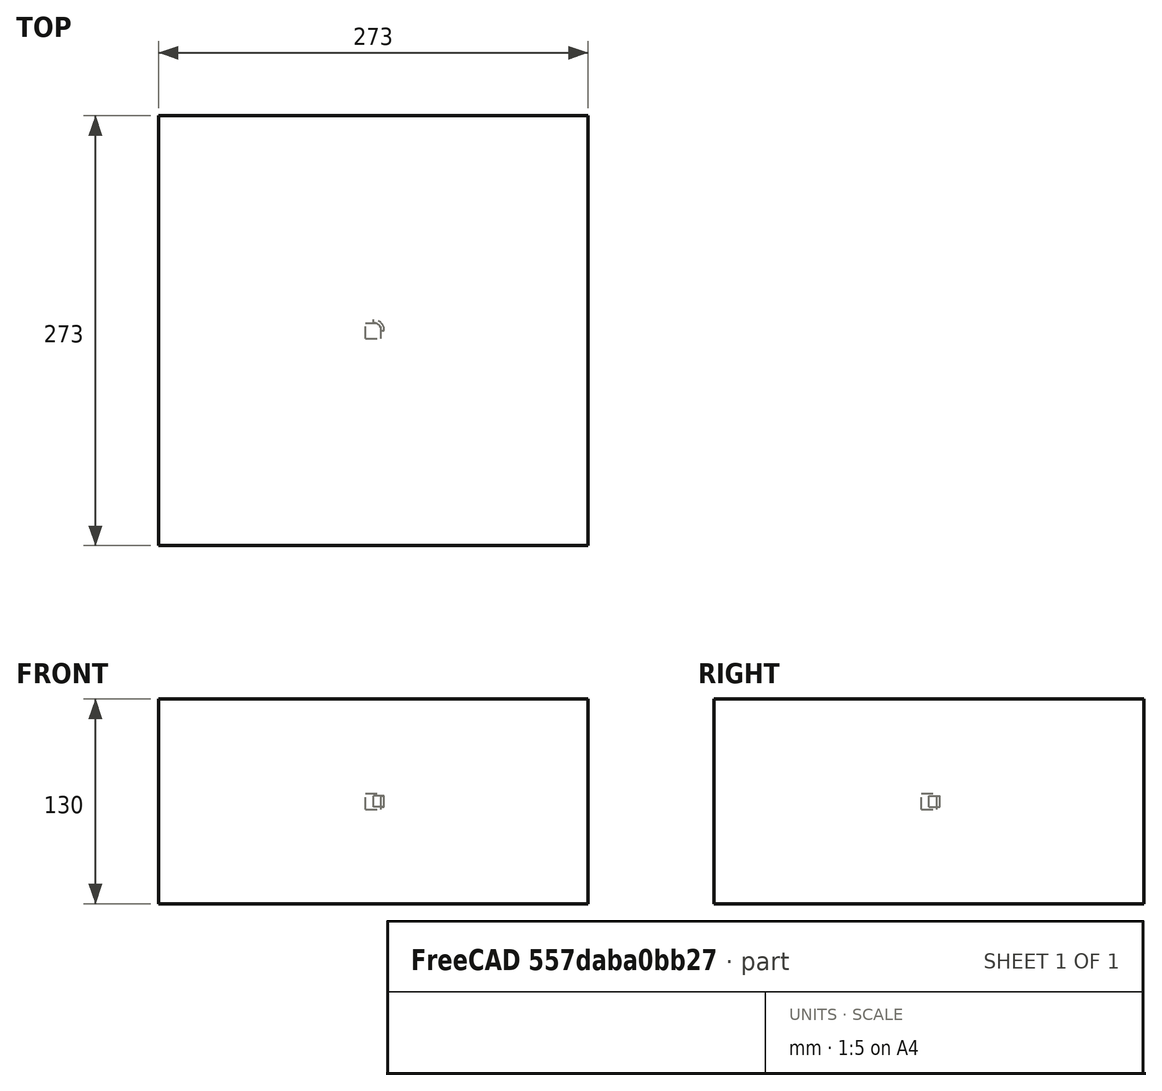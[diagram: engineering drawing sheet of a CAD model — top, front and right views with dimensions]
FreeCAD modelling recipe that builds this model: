
FCSTD DOCUMENT  (FreeCAD 0.20RUnknown)
Label: polarArray-container-b
License: All rights reserved
LicenseURL: http://en.wikipedia.org/wiki/All_rights_reserved
objects: App::DocumentObjectGroupPython×1251, Part::FeaturePython×4, App::Part×4
note: 3 computed .brp shape members not serialized (recipe doc carries the construction recipe); baked Part::Feature solids carry a one-line shape summary decoded from their .brp

FEATURE [App::DocumentObjectGroupPython] HALFPI  # scripted group (container) (typed FeaturePython)
  name = HALFPI
  value = pi/2.
FEATURE [App::DocumentObjectGroupPython] PI  # scripted group (container) (typed FeaturePython)
  name = PI
  value = 1.*pi
FEATURE [App::DocumentObjectGroupPython] TWOPI  # scripted group (container) (typed FeaturePython)
  name = TWOPI
  value = 2.*pi
FEATURE [App::DocumentObjectGroupPython] Constants  # scripted group (container) (typed FeaturePython)
  Group = -> [HALFPI,PI,TWOPI]
FEATURE [App::DocumentObjectGroupPython] Variables  # scripted group (container) (typed FeaturePython)
FEATURE [App::DocumentObjectGroupPython] Quantities  # scripted group (container) (typed FeaturePython)
FEATURE [App::DocumentObjectGroupPython] Isotopes  # scripted group (container) (typed FeaturePython)
FEATURE [App::DocumentObjectGroupPython] Elements  # scripted group (container) (typed FeaturePython)
FEATURE [App::DocumentObjectGroupPython] Matrix  # scripted group (container) (typed FeaturePython)
FEATURE [App::DocumentObjectGroupPython] Surfaces  # scripted group (container) (typed FeaturePython)
FEATURE [App::DocumentObjectGroupPython] Opticals  # scripted group (container) (typed FeaturePython)
  Group = -> [Matrix,Surfaces]
FEATURE [App::DocumentObjectGroupPython] G4Isotopes  # scripted group (container) (typed FeaturePython)
FEATURE [App::DocumentObjectGroupPython] H_element  # scripted group (container) (typed FeaturePython)
  Z = 1
  atom_value = 1.008
  formula = H
  name = H_element
FEATURE [App::DocumentObjectGroupPython] He_element  # scripted group (container) (typed FeaturePython)
  Z = 2
  atom_value = 4.0026
  formula = He
  name = He_element
FEATURE [App::DocumentObjectGroupPython] Li_element  # scripted group (container) (typed FeaturePython)
  Z = 3
  atom_value = 6.94
  formula = Li
  name = Li_element
FEATURE [App::DocumentObjectGroupPython] Be_element  # scripted group (container) (typed FeaturePython)
  Z = 4
  atom_value = 9.01218
  formula = Be
  name = Be_element
FEATURE [App::DocumentObjectGroupPython] B_element  # scripted group (container) (typed FeaturePython)
  Z = 5
  atom_value = 10.81
  formula = B
  name = B_element
FEATURE [App::DocumentObjectGroupPython] C_element  # scripted group (container) (typed FeaturePython)
  Z = 6
  atom_value = 12.011
  formula = C
  name = C_element
FEATURE [App::DocumentObjectGroupPython] N_element  # scripted group (container) (typed FeaturePython)
  Z = 7
  atom_value = 14.007
  formula = N
  name = N_element
FEATURE [App::DocumentObjectGroupPython] O_element  # scripted group (container) (typed FeaturePython)
  Z = 8
  atom_value = 15.999
  formula = O
  name = O_element
FEATURE [App::DocumentObjectGroupPython] F_element  # scripted group (container) (typed FeaturePython)
  Z = 9
  atom_value = 18.9984
  formula = F
  name = F_element
FEATURE [App::DocumentObjectGroupPython] Ne_element  # scripted group (container) (typed FeaturePython)
  Z = 10
  atom_value = 20.1797
  formula = Ne
  name = Ne_element
FEATURE [App::DocumentObjectGroupPython] Na_element  # scripted group (container) (typed FeaturePython)
  Z = 11
  atom_value = 22.9898
  formula = Na
  name = Na_element
FEATURE [App::DocumentObjectGroupPython] Mg_element  # scripted group (container) (typed FeaturePython)
  Z = 12
  atom_value = 24.305
  formula = Mg
  name = Mg_element
FEATURE [App::DocumentObjectGroupPython] Al_element  # scripted group (container) (typed FeaturePython)
  Z = 13
  atom_value = 26.9815
  formula = Al
  name = Al_element
FEATURE [App::DocumentObjectGroupPython] Si_element  # scripted group (container) (typed FeaturePython)
  Z = 14
  atom_value = 28.085
  formula = Si
  name = Si_element
FEATURE [App::DocumentObjectGroupPython] P_element  # scripted group (container) (typed FeaturePython)
  Z = 15
  atom_value = 30.9738
  formula = P
  name = P_element
FEATURE [App::DocumentObjectGroupPython] S_element  # scripted group (container) (typed FeaturePython)
  Z = 16
  atom_value = 32.06
  formula = S
  name = S_element
FEATURE [App::DocumentObjectGroupPython] Cl_element  # scripted group (container) (typed FeaturePython)
  Z = 17
  atom_value = 35.45
  formula = Cl
  name = Cl_element
FEATURE [App::DocumentObjectGroupPython] Ar_element  # scripted group (container) (typed FeaturePython)
  Z = 18
  atom_value = 39.95
  formula = Ar
  name = Ar_element
FEATURE [App::DocumentObjectGroupPython] K_element  # scripted group (container) (typed FeaturePython)
  Z = 19
  atom_value = 39.0983
  formula = K
  name = K_element
FEATURE [App::DocumentObjectGroupPython] Ca_element  # scripted group (container) (typed FeaturePython)
  Z = 20
  atom_value = 40.078
  formula = Ca
  name = Ca_element
FEATURE [App::DocumentObjectGroupPython] Sc_element  # scripted group (container) (typed FeaturePython)
  Z = 21
  atom_value = 44.9559
  formula = Sc
  name = Sc_element
FEATURE [App::DocumentObjectGroupPython] Ti_element  # scripted group (container) (typed FeaturePython)
  Z = 22
  atom_value = 47.867
  formula = Ti
  name = Ti_element
FEATURE [App::DocumentObjectGroupPython] V_element  # scripted group (container) (typed FeaturePython)
  Z = 23
  atom_value = 50.9415
  formula = V
  name = V_element
FEATURE [App::DocumentObjectGroupPython] Cr_element  # scripted group (container) (typed FeaturePython)
  Z = 24
  atom_value = 51.9961
  formula = Cr
  name = Cr_element
FEATURE [App::DocumentObjectGroupPython] Mn_element  # scripted group (container) (typed FeaturePython)
  Z = 25
  atom_value = 54.938
  formula = Mn
  name = Mn_element
FEATURE [App::DocumentObjectGroupPython] Fe_element  # scripted group (container) (typed FeaturePython)
  Z = 26
  atom_value = 55.845
  formula = Fe
  name = Fe_element
FEATURE [App::DocumentObjectGroupPython] Co_element  # scripted group (container) (typed FeaturePython)
  Z = 27
  atom_value = 58.9332
  formula = Co
  name = Co_element
FEATURE [App::DocumentObjectGroupPython] Ni_element  # scripted group (container) (typed FeaturePython)
  Z = 28
  atom_value = 58.6934
  formula = Ni
  name = Ni_element
FEATURE [App::DocumentObjectGroupPython] Cu_element  # scripted group (container) (typed FeaturePython)
  Z = 29
  atom_value = 63.546
  formula = Cu
  name = Cu_element
FEATURE [App::DocumentObjectGroupPython] Zn_element  # scripted group (container) (typed FeaturePython)
  Z = 30
  atom_value = 65.38
  formula = Zn
  name = Zn_element
FEATURE [App::DocumentObjectGroupPython] Ga_element  # scripted group (container) (typed FeaturePython)
  Z = 31
  atom_value = 69.723
  formula = Ga
  name = Ga_element
FEATURE [App::DocumentObjectGroupPython] Ge_element  # scripted group (container) (typed FeaturePython)
  Z = 32
  atom_value = 72.63
  formula = Ge
  name = Ge_element
FEATURE [App::DocumentObjectGroupPython] As_element  # scripted group (container) (typed FeaturePython)
  Z = 33
  atom_value = 74.9216
  formula = As
  name = As_element
FEATURE [App::DocumentObjectGroupPython] Se_element  # scripted group (container) (typed FeaturePython)
  Z = 34
  atom_value = 78.971
  formula = Se
  name = Se_element
FEATURE [App::DocumentObjectGroupPython] Br_element  # scripted group (container) (typed FeaturePython)
  Z = 35
  atom_value = 79.904
  formula = Br
  name = Br_element
FEATURE [App::DocumentObjectGroupPython] Kr_element  # scripted group (container) (typed FeaturePython)
  Z = 36
  atom_value = 83.798
  formula = Kr
  name = Kr_element
FEATURE [App::DocumentObjectGroupPython] Rb_element  # scripted group (container) (typed FeaturePython)
  Z = 37
  atom_value = 85.4678
  formula = Rb
  name = Rb_element
FEATURE [App::DocumentObjectGroupPython] Sr_element  # scripted group (container) (typed FeaturePython)
  Z = 38
  atom_value = 87.62
  formula = Sr
  name = Sr_element
FEATURE [App::DocumentObjectGroupPython] Y_element  # scripted group (container) (typed FeaturePython)
  Z = 39
  atom_value = 88.9058
  formula = Y
  name = Y_element
FEATURE [App::DocumentObjectGroupPython] Zr_element  # scripted group (container) (typed FeaturePython)
  Z = 40
  atom_value = 91.224
  formula = Zr
  name = Zr_element
FEATURE [App::DocumentObjectGroupPython] Nb_element  # scripted group (container) (typed FeaturePython)
  Z = 41
  atom_value = 92.9064
  formula = Nb
  name = Nb_element
FEATURE [App::DocumentObjectGroupPython] Mo_element  # scripted group (container) (typed FeaturePython)
  Z = 42
  atom_value = 95.95
  formula = Mo
  name = Mo_element
FEATURE [App::DocumentObjectGroupPython] Tc_element  # scripted group (container) (typed FeaturePython)
  Z = 43
  atom_value = 97
  formula = Tc
  name = Tc_element
FEATURE [App::DocumentObjectGroupPython] Ru_element  # scripted group (container) (typed FeaturePython)
  Z = 44
  atom_value = 101.07
  formula = Ru
  name = Ru_element
FEATURE [App::DocumentObjectGroupPython] Rh_element  # scripted group (container) (typed FeaturePython)
  Z = 45
  atom_value = 102.905
  formula = Rh
  name = Rh_element
FEATURE [App::DocumentObjectGroupPython] Pd_element  # scripted group (container) (typed FeaturePython)
  Z = 46
  atom_value = 106.42
  formula = Pd
  name = Pd_element
FEATURE [App::DocumentObjectGroupPython] Ag_element  # scripted group (container) (typed FeaturePython)
  Z = 47
  atom_value = 107.868
  formula = Ag
  name = Ag_element
FEATURE [App::DocumentObjectGroupPython] Cd_element  # scripted group (container) (typed FeaturePython)
  Z = 48
  atom_value = 112.414
  formula = Cd
  name = Cd_element
FEATURE [App::DocumentObjectGroupPython] In_element  # scripted group (container) (typed FeaturePython)
  Z = 49
  atom_value = 114.818
  formula = In
  name = In_element
FEATURE [App::DocumentObjectGroupPython] Sn_element  # scripted group (container) (typed FeaturePython)
  Z = 50
  atom_value = 118.71
  formula = Sn
  name = Sn_element
FEATURE [App::DocumentObjectGroupPython] Sb_element  # scripted group (container) (typed FeaturePython)
  Z = 51
  atom_value = 121.76
  formula = Sb
  name = Sb_element
FEATURE [App::DocumentObjectGroupPython] Te_element  # scripted group (container) (typed FeaturePython)
  Z = 52
  atom_value = 127.6
  formula = Te
  name = Te_element
FEATURE [App::DocumentObjectGroupPython] I_element  # scripted group (container) (typed FeaturePython)
  Z = 53
  atom_value = 126.904
  formula = I
  name = I_element
FEATURE [App::DocumentObjectGroupPython] Xe_element  # scripted group (container) (typed FeaturePython)
  Z = 54
  atom_value = 131.293
  formula = Xe
  name = Xe_element
FEATURE [App::DocumentObjectGroupPython] Cs_element  # scripted group (container) (typed FeaturePython)
  Z = 55
  atom_value = 132.905
  formula = Cs
  name = Cs_element
FEATURE [App::DocumentObjectGroupPython] Ba_element  # scripted group (container) (typed FeaturePython)
  Z = 56
  atom_value = 137.327
  formula = Ba
  name = Ba_element
FEATURE [App::DocumentObjectGroupPython] La_element  # scripted group (container) (typed FeaturePython)
  Z = 57
  atom_value = 138.905
  formula = La
  name = La_element
FEATURE [App::DocumentObjectGroupPython] Ce_element  # scripted group (container) (typed FeaturePython)
  Z = 58
  atom_value = 140.116
  formula = Ce
  name = Ce_element
FEATURE [App::DocumentObjectGroupPython] Pr_element  # scripted group (container) (typed FeaturePython)
  Z = 59
  atom_value = 140.908
  formula = Pr
  name = Pr_element
FEATURE [App::DocumentObjectGroupPython] Nd_element  # scripted group (container) (typed FeaturePython)
  Z = 60
  atom_value = 144.242
  formula = Nd
  name = Nd_element
FEATURE [App::DocumentObjectGroupPython] Pm_element  # scripted group (container) (typed FeaturePython)
  Z = 61
  atom_value = 145
  formula = Pm
  name = Pm_element
FEATURE [App::DocumentObjectGroupPython] Sm_element  # scripted group (container) (typed FeaturePython)
  Z = 62
  atom_value = 150.36
  formula = Sm
  name = Sm_element
FEATURE [App::DocumentObjectGroupPython] Eu_element  # scripted group (container) (typed FeaturePython)
  Z = 63
  atom_value = 151.964
  formula = Eu
  name = Eu_element
FEATURE [App::DocumentObjectGroupPython] Gd_element  # scripted group (container) (typed FeaturePython)
  Z = 64
  atom_value = 157.25
  formula = Gd
  name = Gd_element
FEATURE [App::DocumentObjectGroupPython] Tb_element  # scripted group (container) (typed FeaturePython)
  Z = 65
  atom_value = 158.925
  formula = Tb
  name = Tb_element
FEATURE [App::DocumentObjectGroupPython] Dy_element  # scripted group (container) (typed FeaturePython)
  Z = 66
  atom_value = 162.5
  formula = Dy
  name = Dy_element
FEATURE [App::DocumentObjectGroupPython] Ho_element  # scripted group (container) (typed FeaturePython)
  Z = 67
  atom_value = 164.93
  formula = Ho
  name = Ho_element
FEATURE [App::DocumentObjectGroupPython] Er_element  # scripted group (container) (typed FeaturePython)
  Z = 68
  atom_value = 167.259
  formula = Er
  name = Er_element
FEATURE [App::DocumentObjectGroupPython] Tm_element  # scripted group (container) (typed FeaturePython)
  Z = 69
  atom_value = 168.934
  formula = Tm
  name = Tm_element
FEATURE [App::DocumentObjectGroupPython] Yb_element  # scripted group (container) (typed FeaturePython)
  Z = 70
  atom_value = 173.045
  formula = Yb
  name = Yb_element
FEATURE [App::DocumentObjectGroupPython] Lu_element  # scripted group (container) (typed FeaturePython)
  Z = 71
  atom_value = 174.967
  formula = Lu
  name = Lu_element
FEATURE [App::DocumentObjectGroupPython] Hf_element  # scripted group (container) (typed FeaturePython)
  Z = 72
  atom_value = 178.49
  formula = Hf
  name = Hf_element
FEATURE [App::DocumentObjectGroupPython] Ta_element  # scripted group (container) (typed FeaturePython)
  Z = 73
  atom_value = 180.948
  formula = Ta
  name = Ta_element
FEATURE [App::DocumentObjectGroupPython] W_element  # scripted group (container) (typed FeaturePython)
  Z = 74
  atom_value = 183.84
  formula = W
  name = W_element
FEATURE [App::DocumentObjectGroupPython] Re_element  # scripted group (container) (typed FeaturePython)
  Z = 75
  atom_value = 186.207
  formula = Re
  name = Re_element
FEATURE [App::DocumentObjectGroupPython] Os_element  # scripted group (container) (typed FeaturePython)
  Z = 76
  atom_value = 190.23
  formula = Os
  name = Os_element
FEATURE [App::DocumentObjectGroupPython] Ir_element  # scripted group (container) (typed FeaturePython)
  Z = 77
  atom_value = 192.217
  formula = Ir
  name = Ir_element
FEATURE [App::DocumentObjectGroupPython] Pt_element  # scripted group (container) (typed FeaturePython)
  Z = 78
  atom_value = 195.084
  formula = Pt
  name = Pt_element
FEATURE [App::DocumentObjectGroupPython] Au_element  # scripted group (container) (typed FeaturePython)
  Z = 79
  atom_value = 196.967
  formula = Au
  name = Au_element
FEATURE [App::DocumentObjectGroupPython] Hg_element  # scripted group (container) (typed FeaturePython)
  Z = 80
  atom_value = 200.592
  formula = Hg
  name = Hg_element
FEATURE [App::DocumentObjectGroupPython] Tl_element  # scripted group (container) (typed FeaturePython)
  Z = 81
  atom_value = 204.38
  formula = Tl
  name = Tl_element
FEATURE [App::DocumentObjectGroupPython] Pb_element  # scripted group (container) (typed FeaturePython)
  Z = 82
  atom_value = 207.2
  formula = Pb
  name = Pb_element
FEATURE [App::DocumentObjectGroupPython] Bi_element  # scripted group (container) (typed FeaturePython)
  Z = 83
  atom_value = 208.98
  formula = Bi
  name = Bi_element
FEATURE [App::DocumentObjectGroupPython] Po_element  # scripted group (container) (typed FeaturePython)
  Z = 84
  atom_value = 209
  formula = Po
  name = Po_element
FEATURE [App::DocumentObjectGroupPython] At_element  # scripted group (container) (typed FeaturePython)
  Z = 85
  atom_value = 210
  formula = At
  name = At_element
FEATURE [App::DocumentObjectGroupPython] Rn_element  # scripted group (container) (typed FeaturePython)
  Z = 86
  atom_value = 222
  formula = Rn
  name = Rn_element
FEATURE [App::DocumentObjectGroupPython] Fr_element  # scripted group (container) (typed FeaturePython)
  Z = 87
  atom_value = 223
  formula = Fr
  name = Fr_element
FEATURE [App::DocumentObjectGroupPython] Ra_element  # scripted group (container) (typed FeaturePython)
  Z = 88
  atom_value = 226
  formula = Ra
  name = Ra_element
FEATURE [App::DocumentObjectGroupPython] Ac_element  # scripted group (container) (typed FeaturePython)
  Z = 89
  atom_value = 227
  formula = Ac
  name = Ac_element
FEATURE [App::DocumentObjectGroupPython] Th_element  # scripted group (container) (typed FeaturePython)
  Z = 90
  atom_value = 232.038
  formula = Th
  name = Th_element
FEATURE [App::DocumentObjectGroupPython] Pa_element  # scripted group (container) (typed FeaturePython)
  Z = 91
  atom_value = 231.036
  formula = Pa
  name = Pa_element
FEATURE [App::DocumentObjectGroupPython] U_element  # scripted group (container) (typed FeaturePython)
  Z = 92
  atom_value = 238.029
  formula = U
  name = U_element
FEATURE [App::DocumentObjectGroupPython] Np_element  # scripted group (container) (typed FeaturePython)
  Z = 93
  atom_value = 237
  formula = Np
  name = Np_element
FEATURE [App::DocumentObjectGroupPython] Pu_element  # scripted group (container) (typed FeaturePython)
  Z = 94
  atom_value = 244
  formula = Pu
  name = Pu_element
FEATURE [App::DocumentObjectGroupPython] Am_element  # scripted group (container) (typed FeaturePython)
  Z = 95
  atom_value = 243
  formula = Am
  name = Am_element
FEATURE [App::DocumentObjectGroupPython] Cm_element  # scripted group (container) (typed FeaturePython)
  Z = 96
  atom_value = 247
  formula = Cm
  name = Cm_element
FEATURE [App::DocumentObjectGroupPython] Bk_element  # scripted group (container) (typed FeaturePython)
  Z = 97
  atom_value = 247
  formula = Bk
  name = Bk_element
FEATURE [App::DocumentObjectGroupPython] Cf_element  # scripted group (container) (typed FeaturePython)
  Z = 98
  atom_value = 251
  formula = Cf
  name = Cf_element
FEATURE [App::DocumentObjectGroupPython] G4Elements  # scripted group (container) (typed FeaturePython)
  Group = -> [H_element,He_element,Li_element,Be_element,B_element,C_element,N_element,O_element,F_element,Ne_element,Na_element,Mg_element,Al_element,Si_element,P_element,S_element,Cl_element,Ar_element,K_element,Ca_element,Sc_element,Ti_element,V_element,Cr_element,Mn_element,Fe_element,Co_element,Ni_element,Cu_element,Zn_element,Ga_element,Ge_element,As_element,Se_element,Br_element,Kr_element,Rb_element,+61 more]
FEATURE [App::DocumentObjectGroupPython] H_element001  label="H_element : 0.101"  # scripted group (container) (typed FeaturePython)
  n = 0.101327
FEATURE [App::DocumentObjectGroupPython] C_element001  label="C_element : 0.775"  # scripted group (container) (typed FeaturePython)
  n = 0.7755
FEATURE [App::DocumentObjectGroupPython] N_element001  label="N_element : 0.035"  # scripted group (container) (typed FeaturePython)
  n = 0.035057
FEATURE [App::DocumentObjectGroupPython] O_element001  label="O_element : 0.052"  # scripted group (container) (typed FeaturePython)
  n = 0.0523159
FEATURE [App::DocumentObjectGroupPython] F_element001  label="F_element : 0.017"  # scripted group (container) (typed FeaturePython)
  n = 0.017422
FEATURE [App::DocumentObjectGroupPython] Ca_element001  label="Ca_element : 0.018"  # scripted group (container) (typed FeaturePython)
  n = 0.018378
FEATURE [App::DocumentObjectGroupPython] G4_A_150_TISSUE  label="G4_A-150_TISSUE"  # scripted group (container) (typed FeaturePython)
  Dunit = g/cm3
  Dvalue = 1.127
  Group = -> [H_element001,C_element001,N_element001,O_element001,F_element001,Ca_element001]
  conduct = 2
  density = 1
  expand = 3
  formula = G4_A-150_TISSUE
  name = G4_A-150_TISSUE
  specific = 4
FEATURE [App::DocumentObjectGroupPython] C_element002  label="C_element : 3"  # scripted group (container) (typed FeaturePython)
  n = 3
  ref = C_element
FEATURE [App::DocumentObjectGroupPython] H_element002  label="H_element : 6"  # scripted group (container) (typed FeaturePython)
  n = 6
  ref = H_element
FEATURE [App::DocumentObjectGroupPython] O_element002  label="O_element : 1"  # scripted group (container) (typed FeaturePython)
  n = 1
  ref = O_element
FEATURE [App::DocumentObjectGroupPython] G4_ACETONE  # scripted group (container) (typed FeaturePython)
  Dunit = g/cm3
  Dvalue = 0.7899
  Group = -> [C_element002,H_element002,O_element002]
  conduct = 2
  density = 1
  expand = 3
  formula = G4_ACETONE
  name = G4_ACETONE
  specific = 4
FEATURE [App::DocumentObjectGroupPython] C_element003  label="C_element : 2"  # scripted group (container) (typed FeaturePython)
  n = 2
  ref = C_element
FEATURE [App::DocumentObjectGroupPython] H_element003  label="H_element : 2"  # scripted group (container) (typed FeaturePython)
  n = 2
  ref = H_element
FEATURE [App::DocumentObjectGroupPython] G4_ACETYLENE  # scripted group (container) (typed FeaturePython)
  Dunit = g/cm3
  Dvalue = 0.0010967
  Group = -> [C_element003,H_element003]
  conduct = 2
  density = 1
  expand = 3
  formula = G4_ACETYLENE
  name = G4_ACETYLENE
  specific = 4
FEATURE [App::DocumentObjectGroupPython] C_element004  label="C_element : 5"  # scripted group (container) (typed FeaturePython)
  n = 5
  ref = C_element
FEATURE [App::DocumentObjectGroupPython] H_element004  label="H_element : 5"  # scripted group (container) (typed FeaturePython)
  n = 5
  ref = H_element
FEATURE [App::DocumentObjectGroupPython] N_element002  label="N_element : 5"  # scripted group (container) (typed FeaturePython)
  n = 5
  ref = N_element
FEATURE [App::DocumentObjectGroupPython] G4_ADENINE  # scripted group (container) (typed FeaturePython)
  Dunit = g/cm3
  Dvalue = 1.6
  Group = -> [C_element004,H_element004,N_element002]
  conduct = 2
  density = 1
  expand = 3
  formula = G4_ADENINE
  name = G4_ADENINE
  specific = 4
FEATURE [App::DocumentObjectGroupPython] H_element005  label="H_element : 0.114"  # scripted group (container) (typed FeaturePython)
  n = 0.114
FEATURE [App::DocumentObjectGroupPython] C_element005  label="C_element : 0.598"  # scripted group (container) (typed FeaturePython)
  n = 0.598
FEATURE [App::DocumentObjectGroupPython] N_element003  label="N_element : 0.007"  # scripted group (container) (typed FeaturePython)
  n = 0.007
FEATURE [App::DocumentObjectGroupPython] O_element003  label="O_element : 0.278"  # scripted group (container) (typed FeaturePython)
  n = 0.278
FEATURE [App::DocumentObjectGroupPython] Na_element001  label="Na_element : 0.001"  # scripted group (container) (typed FeaturePython)
  n = 0.001
FEATURE [App::DocumentObjectGroupPython] S_element001  label="S_element : 0.001"  # scripted group (container) (typed FeaturePython)
  n = 0.001
FEATURE [App::DocumentObjectGroupPython] Cl_element001  label="Cl_element : 0.001"  # scripted group (container) (typed FeaturePython)
  n = 0.001
FEATURE [App::DocumentObjectGroupPython] G4_ADIPOSE_TISSUE_ICRP  # scripted group (container) (typed FeaturePython)
  Dunit = g/cm3
  Dvalue = 0.95
  Group = -> [H_element005,C_element005,N_element003,O_element003,Na_element001,S_element001,Cl_element001]
  conduct = 2
  density = 1
  expand = 3
  formula = G4_ADIPOSE_TISSUE_ICRP
  name = G4_ADIPOSE_TISSUE_ICRP
  specific = 4
FEATURE [App::DocumentObjectGroupPython] C_element006  label="C_element : 0.000"  # scripted group (container) (typed FeaturePython)
  n = 0.000124
FEATURE [App::DocumentObjectGroupPython] N_element004  label="N_element : 0.755"  # scripted group (container) (typed FeaturePython)
  n = 0.755268
FEATURE [App::DocumentObjectGroupPython] O_element004  label="O_element : 0.232"  # scripted group (container) (typed FeaturePython)
  n = 0.231781
FEATURE [App::DocumentObjectGroupPython] Ar_element001  label="Ar_element : 0.013"  # scripted group (container) (typed FeaturePython)
  n = 0.012827
FEATURE [App::DocumentObjectGroupPython] G4_AIR  # scripted group (container) (typed FeaturePython)
  Dunit = g/cm3
  Dvalue = 0.00120479
  Group = -> [C_element006,N_element004,O_element004,Ar_element001]
  conduct = 2
  density = 1
  expand = 3
  formula = G4_AIR
  name = G4_AIR
  specific = 4
FEATURE [App::DocumentObjectGroupPython] C_element007  label="C_element : 006"  # scripted group (container) (typed FeaturePython)
  n = 3
  ref = C_element
FEATURE [App::DocumentObjectGroupPython] H_element006  label="H_element : 7"  # scripted group (container) (typed FeaturePython)
  n = 7
  ref = H_element
FEATURE [App::DocumentObjectGroupPython] N_element005  label="N_element : 1"  # scripted group (container) (typed FeaturePython)
  n = 1
  ref = N_element
FEATURE [App::DocumentObjectGroupPython] O_element005  label="O_element : 2"  # scripted group (container) (typed FeaturePython)
  n = 2
  ref = O_element
FEATURE [App::DocumentObjectGroupPython] G4_ALANINE  # scripted group (container) (typed FeaturePython)
  Dunit = g/cm3
  Dvalue = 1.42
  Group = -> [C_element007,H_element006,N_element005,O_element005]
  conduct = 2
  density = 1
  expand = 3
  formula = G4_ALANINE
  name = G4_ALANINE
  specific = 4
FEATURE [App::DocumentObjectGroupPython] Al_element001  label="Al_element : 2"  # scripted group (container) (typed FeaturePython)
  n = 2
  ref = Al_element
FEATURE [App::DocumentObjectGroupPython] O_element006  label="O_element : 3"  # scripted group (container) (typed FeaturePython)
  n = 3
  ref = O_element
FEATURE [App::DocumentObjectGroupPython] G4_ALUMINUM_OXIDE  # scripted group (container) (typed FeaturePython)
  Dunit = g/cm3
  Dvalue = 3.97
  Group = -> [Al_element001,O_element006]
  conduct = 2
  density = 1
  expand = 3
  formula = G4_ALUMINUM_OXIDE
  name = G4_ALUMINUM_OXIDE
  specific = 4
FEATURE [App::DocumentObjectGroupPython] H_element007  label="H_element : 0.106"  # scripted group (container) (typed FeaturePython)
  n = 0.10593
FEATURE [App::DocumentObjectGroupPython] C_element008  label="C_element : 0.789"  # scripted group (container) (typed FeaturePython)
  n = 0.788974
FEATURE [App::DocumentObjectGroupPython] O_element007  label="O_element : 0.105"  # scripted group (container) (typed FeaturePython)
  n = 0.105096
FEATURE [App::DocumentObjectGroupPython] G4_AMBER  # scripted group (container) (typed FeaturePython)
  Dunit = g/cm3
  Dvalue = 1.1
  Group = -> [H_element007,C_element008,O_element007]
  conduct = 2
  density = 1
  expand = 3
  formula = G4_AMBER
  name = G4_AMBER
  specific = 4
FEATURE [App::DocumentObjectGroupPython] N_element006  label="N_element : 006"  # scripted group (container) (typed FeaturePython)
  n = 1
  ref = N_element
FEATURE [App::DocumentObjectGroupPython] H_element008  label="H_element : 3"  # scripted group (container) (typed FeaturePython)
  n = 3
  ref = H_element
FEATURE [App::DocumentObjectGroupPython] G4_AMMONIA  # scripted group (container) (typed FeaturePython)
  Dunit = g/cm3
  Dvalue = 0.000826019
  Group = -> [N_element006,H_element008]
  conduct = 2
  density = 1
  expand = 3
  formula = G4_AMMONIA
  name = G4_AMMONIA
  specific = 4
FEATURE [App::DocumentObjectGroupPython] C_element009  label="C_element : 6"  # scripted group (container) (typed FeaturePython)
  n = 6
  ref = C_element
FEATURE [App::DocumentObjectGroupPython] H_element009  label="H_element : 008"  # scripted group (container) (typed FeaturePython)
  n = 7
  ref = H_element
FEATURE [App::DocumentObjectGroupPython] N_element007  label="N_element : 007"  # scripted group (container) (typed FeaturePython)
  n = 1
  ref = N_element
FEATURE [App::DocumentObjectGroupPython] G4_ANILINE  # scripted group (container) (typed FeaturePython)
  Dunit = g/cm3
  Dvalue = 1.0235
  Group = -> [C_element009,H_element009,N_element007]
  conduct = 2
  density = 1
  expand = 3
  formula = G4_ANILINE
  name = G4_ANILINE
  specific = 4
FEATURE [App::DocumentObjectGroupPython] C_element010  label="C_element : 14"  # scripted group (container) (typed FeaturePython)
  n = 14
  ref = C_element
FEATURE [App::DocumentObjectGroupPython] H_element010  label="H_element : 10"  # scripted group (container) (typed FeaturePython)
  n = 10
  ref = H_element
FEATURE [App::DocumentObjectGroupPython] G4_ANTHRACENE  # scripted group (container) (typed FeaturePython)
  Dunit = g/cm3
  Dvalue = 1.283
  Group = -> [C_element010,H_element010]
  conduct = 2
  density = 1
  expand = 3
  formula = G4_ANTHRACENE
  name = G4_ANTHRACENE
  specific = 4
FEATURE [App::DocumentObjectGroupPython] H_element011  label="H_element : 0.065"  # scripted group (container) (typed FeaturePython)
  n = 0.0654709
FEATURE [App::DocumentObjectGroupPython] C_element011  label="C_element : 0.537"  # scripted group (container) (typed FeaturePython)
  n = 0.536944
FEATURE [App::DocumentObjectGroupPython] N_element008  label="N_element : 0.021"  # scripted group (container) (typed FeaturePython)
  n = 0.0215
FEATURE [App::DocumentObjectGroupPython] O_element008  label="O_element : 0.032"  # scripted group (container) (typed FeaturePython)
  n = 0.032085
FEATURE [App::DocumentObjectGroupPython] F_element002  label="F_element : 0.167"  # scripted group (container) (typed FeaturePython)
  n = 0.167411
FEATURE [App::DocumentObjectGroupPython] Ca_element002  label="Ca_element : 0.177"  # scripted group (container) (typed FeaturePython)
  n = 0.176589
FEATURE [App::DocumentObjectGroupPython] G4_B_100_BONE  label="G4_B-100_BONE"  # scripted group (container) (typed FeaturePython)
  Dunit = g/cm3
  Dvalue = 1.45
  Group = -> [H_element011,C_element011,N_element008,O_element008,F_element002,Ca_element002]
  conduct = 2
  density = 1
  expand = 3
  formula = G4_B-100_BONE
  name = G4_B-100_BONE
  specific = 4
FEATURE [App::DocumentObjectGroupPython] H_element012  label="H_element : 0.057"  # scripted group (container) (typed FeaturePython)
  n = 0.057441
FEATURE [App::DocumentObjectGroupPython] C_element012  label="C_element : 0.790"  # scripted group (container) (typed FeaturePython)
  n = 0.774591
FEATURE [App::DocumentObjectGroupPython] O_element009  label="O_element : 0.168"  # scripted group (container) (typed FeaturePython)
  n = 0.167968
FEATURE [App::DocumentObjectGroupPython] G4_BAKELITE  # scripted group (container) (typed FeaturePython)
  Dunit = g/cm3
  Dvalue = 1.25
  Group = -> [H_element012,C_element012,O_element009]
  conduct = 2
  density = 1
  expand = 3
  formula = G4_BAKELITE
  name = G4_BAKELITE
  specific = 4
FEATURE [App::DocumentObjectGroupPython] Ba_element001  label="Ba_element : 1"  # scripted group (container) (typed FeaturePython)
  n = 1
  ref = Ba_element
FEATURE [App::DocumentObjectGroupPython] F_element003  label="F_element : 2"  # scripted group (container) (typed FeaturePython)
  n = 2
  ref = F_element
FEATURE [App::DocumentObjectGroupPython] G4_BARIUM_FLUORIDE  # scripted group (container) (typed FeaturePython)
  Dunit = g/cm3
  Dvalue = 4.89
  Group = -> [Ba_element001,F_element003]
  conduct = 2
  density = 1
  expand = 3
  formula = G4_BARIUM_FLUORIDE
  name = G4_BARIUM_FLUORIDE
  specific = 4
FEATURE [App::DocumentObjectGroupPython] Ba_element002  label="Ba_element : 002"  # scripted group (container) (typed FeaturePython)
  n = 1
  ref = Ba_element
FEATURE [App::DocumentObjectGroupPython] S_element002  label="S_element : 1"  # scripted group (container) (typed FeaturePython)
  n = 1
  ref = S_element
FEATURE [App::DocumentObjectGroupPython] O_element010  label="O_element : 4"  # scripted group (container) (typed FeaturePython)
  n = 4
  ref = O_element
FEATURE [App::DocumentObjectGroupPython] G4_BARIUM_SULFATE  # scripted group (container) (typed FeaturePython)
  Dunit = g/cm3
  Dvalue = 4.5
  Group = -> [Ba_element002,S_element002,O_element010]
  conduct = 2
  density = 1
  expand = 3
  formula = G4_BARIUM_SULFATE
  name = G4_BARIUM_SULFATE
  specific = 4
FEATURE [App::DocumentObjectGroupPython] C_element013  label="C_element : 007"  # scripted group (container) (typed FeaturePython)
  n = 6
  ref = C_element
FEATURE [App::DocumentObjectGroupPython] H_element013  label="H_element : 009"  # scripted group (container) (typed FeaturePython)
  n = 6
  ref = H_element
FEATURE [App::DocumentObjectGroupPython] G4_BENZENE  # scripted group (container) (typed FeaturePython)
  Dunit = g/cm3
  Dvalue = 0.87865
  Group = -> [C_element013,H_element013]
  conduct = 2
  density = 1
  expand = 3
  formula = G4_BENZENE
  name = G4_BENZENE
  specific = 4
FEATURE [App::DocumentObjectGroupPython] Be_element001  label="Be_element : 1"  # scripted group (container) (typed FeaturePython)
  n = 1
  ref = Be_element
FEATURE [App::DocumentObjectGroupPython] O_element011  label="O_element : 005"  # scripted group (container) (typed FeaturePython)
  n = 1
  ref = O_element
FEATURE [App::DocumentObjectGroupPython] G4_BERYLLIUM_OXIDE  # scripted group (container) (typed FeaturePython)
  Dunit = g/cm3
  Dvalue = 3.01
  Group = -> [Be_element001,O_element011]
  conduct = 2
  density = 1
  expand = 3
  formula = G4_BERYLLIUM_OXIDE
  name = G4_BERYLLIUM_OXIDE
  specific = 4
FEATURE [App::DocumentObjectGroupPython] Bi_element001  label="Bi_element : 4"  # scripted group (container) (typed FeaturePython)
  n = 4
  ref = Bi_element
FEATURE [App::DocumentObjectGroupPython] Ge_element001  label="Ge_element : 3"  # scripted group (container) (typed FeaturePython)
  n = 3
  ref = Ge_element
FEATURE [App::DocumentObjectGroupPython] O_element012  label="O_element : 12"  # scripted group (container) (typed FeaturePython)
  n = 12
  ref = O_element
FEATURE [App::DocumentObjectGroupPython] G4_BGO  # scripted group (container) (typed FeaturePython)
  Dunit = g/cm3
  Dvalue = 7.13
  Group = -> [Bi_element001,Ge_element001,O_element012]
  conduct = 2
  density = 1
  expand = 3
  formula = G4_BGO
  name = G4_BGO
  specific = 4
FEATURE [App::DocumentObjectGroupPython] H_element014  label="H_element : 0.102"  # scripted group (container) (typed FeaturePython)
  n = 0.102
FEATURE [App::DocumentObjectGroupPython] C_element014  label="C_element : 0.110"  # scripted group (container) (typed FeaturePython)
  n = 0.11
FEATURE [App::DocumentObjectGroupPython] N_element009  label="N_element : 0.033"  # scripted group (container) (typed FeaturePython)
  n = 0.033
FEATURE [App::DocumentObjectGroupPython] O_element013  label="O_element : 0.745"  # scripted group (container) (typed FeaturePython)
  n = 0.745
FEATURE [App::DocumentObjectGroupPython] Na_element002  label="Na_element : 0.002"  # scripted group (container) (typed FeaturePython)
  n = 0.001
FEATURE [App::DocumentObjectGroupPython] P_element001  label="P_element : 0.001"  # scripted group (container) (typed FeaturePython)
  n = 0.001
FEATURE [App::DocumentObjectGroupPython] S_element003  label="S_element : 0.002"  # scripted group (container) (typed FeaturePython)
  n = 0.002
FEATURE [App::DocumentObjectGroupPython] Cl_element002  label="Cl_element : 0.003"  # scripted group (container) (typed FeaturePython)
  n = 0.003
FEATURE [App::DocumentObjectGroupPython] K_element001  label="K_element : 0.002"  # scripted group (container) (typed FeaturePython)
  n = 0.002
FEATURE [App::DocumentObjectGroupPython] Fe_element001  label="Fe_element : 0.001"  # scripted group (container) (typed FeaturePython)
  n = 0.001
FEATURE [App::DocumentObjectGroupPython] G4_BLOOD_ICRP  # scripted group (container) (typed FeaturePython)
  Dunit = g/cm3
  Dvalue = 1.06
  Group = -> [H_element014,C_element014,N_element009,O_element013,Na_element002,P_element001,S_element003,Cl_element002,K_element001,Fe_element001]
  conduct = 2
  density = 1
  expand = 3
  formula = G4_BLOOD_ICRP
  name = G4_BLOOD_ICRP
  specific = 4
FEATURE [App::DocumentObjectGroupPython] H_element015  label="H_element : 0.064"  # scripted group (container) (typed FeaturePython)
  n = 0.064
FEATURE [App::DocumentObjectGroupPython] C_element015  label="C_element : 0.278"  # scripted group (container) (typed FeaturePython)
  n = 0.278
FEATURE [App::DocumentObjectGroupPython] N_element010  label="N_element : 0.027"  # scripted group (container) (typed FeaturePython)
  n = 0.027
FEATURE [App::DocumentObjectGroupPython] O_element014  label="O_element : 0.410"  # scripted group (container) (typed FeaturePython)
  n = 0.41
FEATURE [App::DocumentObjectGroupPython] Mg_element001  label="Mg_element : 0.002"  # scripted group (container) (typed FeaturePython)
  n = 0.002
FEATURE [App::DocumentObjectGroupPython] P_element002  label="P_element : 0.070"  # scripted group (container) (typed FeaturePython)
  n = 0.07
FEATURE [App::DocumentObjectGroupPython] S_element004  label="S_element : 0.003"  # scripted group (container) (typed FeaturePython)
  n = 0.002
FEATURE [App::DocumentObjectGroupPython] Ca_element003  label="Ca_element : 0.147"  # scripted group (container) (typed FeaturePython)
  n = 0.147
FEATURE [App::DocumentObjectGroupPython] G4_BONE_COMPACT_ICRU  # scripted group (container) (typed FeaturePython)
  Dunit = g/cm3
  Dvalue = 1.85
  Group = -> [H_element015,C_element015,N_element010,O_element014,Mg_element001,P_element002,S_element004,Ca_element003]
  conduct = 2
  density = 1
  expand = 3
  formula = G4_BONE_COMPACT_ICRU
  name = G4_BONE_COMPACT_ICRU
  specific = 4
FEATURE [App::DocumentObjectGroupPython] H_element016  label="H_element : 0.034"  # scripted group (container) (typed FeaturePython)
  n = 0.034
FEATURE [App::DocumentObjectGroupPython] C_element016  label="C_element : 0.155"  # scripted group (container) (typed FeaturePython)
  n = 0.155
FEATURE [App::DocumentObjectGroupPython] N_element011  label="N_element : 0.042"  # scripted group (container) (typed FeaturePython)
  n = 0.042
FEATURE [App::DocumentObjectGroupPython] O_element015  label="O_element : 0.435"  # scripted group (container) (typed FeaturePython)
  n = 0.435
FEATURE [App::DocumentObjectGroupPython] Na_element003  label="Na_element : 0.003"  # scripted group (container) (typed FeaturePython)
  n = 0.001
FEATURE [App::DocumentObjectGroupPython] Mg_element002  label="Mg_element : 0.003"  # scripted group (container) (typed FeaturePython)
  n = 0.002
FEATURE [App::DocumentObjectGroupPython] P_element003  label="P_element : 0.103"  # scripted group (container) (typed FeaturePython)
  n = 0.103
FEATURE [App::DocumentObjectGroupPython] S_element005  label="S_element : 0.004"  # scripted group (container) (typed FeaturePython)
  n = 0.003
FEATURE [App::DocumentObjectGroupPython] Ca_element004  label="Ca_element : 0.225"  # scripted group (container) (typed FeaturePython)
  n = 0.225
FEATURE [App::DocumentObjectGroupPython] G4_BONE_CORTICAL_ICRP  # scripted group (container) (typed FeaturePython)
  Dunit = g/cm3
  Dvalue = 1.92
  Group = -> [H_element016,C_element016,N_element011,O_element015,Na_element003,Mg_element002,P_element003,S_element005,Ca_element004]
  conduct = 2
  density = 1
  expand = 3
  formula = G4_BONE_CORTICAL_ICRP
  name = G4_BONE_CORTICAL_ICRP
  specific = 4
FEATURE [App::DocumentObjectGroupPython] B_element001  label="B_element : 4"  # scripted group (container) (typed FeaturePython)
  n = 4
  ref = B_element
FEATURE [App::DocumentObjectGroupPython] C_element017  label="C_element : 1"  # scripted group (container) (typed FeaturePython)
  n = 1
  ref = C_element
FEATURE [App::DocumentObjectGroupPython] G4_BORON_CARBIDE  # scripted group (container) (typed FeaturePython)
  Dunit = g/cm3
  Dvalue = 2.52
  Group = -> [B_element001,C_element017]
  conduct = 2
  density = 1
  expand = 3
  formula = G4_BORON_CARBIDE
  name = G4_BORON_CARBIDE
  specific = 4
FEATURE [App::DocumentObjectGroupPython] B_element002  label="B_element : 2"  # scripted group (container) (typed FeaturePython)
  n = 2
  ref = B_element
FEATURE [App::DocumentObjectGroupPython] O_element016  label="O_element : 006"  # scripted group (container) (typed FeaturePython)
  n = 3
  ref = O_element
FEATURE [App::DocumentObjectGroupPython] G4_BORON_OXIDE  # scripted group (container) (typed FeaturePython)
  Dunit = g/cm3
  Dvalue = 1.812
  Group = -> [B_element002,O_element016]
  conduct = 2
  density = 1
  expand = 3
  formula = G4_BORON_OXIDE
  name = G4_BORON_OXIDE
  specific = 4
FEATURE [App::DocumentObjectGroupPython] H_element017  label="H_element : 0.107"  # scripted group (container) (typed FeaturePython)
  n = 0.107
FEATURE [App::DocumentObjectGroupPython] C_element018  label="C_element : 0.145"  # scripted group (container) (typed FeaturePython)
  n = 0.145
FEATURE [App::DocumentObjectGroupPython] N_element012  label="N_element : 0.022"  # scripted group (container) (typed FeaturePython)
  n = 0.022
FEATURE [App::DocumentObjectGroupPython] O_element017  label="O_element : 0.712"  # scripted group (container) (typed FeaturePython)
  n = 0.712
FEATURE [App::DocumentObjectGroupPython] Na_element004  label="Na_element : 0.004"  # scripted group (container) (typed FeaturePython)
  n = 0.002
FEATURE [App::DocumentObjectGroupPython] P_element004  label="P_element : 0.004"  # scripted group (container) (typed FeaturePython)
  n = 0.004
FEATURE [App::DocumentObjectGroupPython] S_element006  label="S_element : 0.005"  # scripted group (container) (typed FeaturePython)
  n = 0.002
FEATURE [App::DocumentObjectGroupPython] Cl_element003  label="Cl_element : 0.004"  # scripted group (container) (typed FeaturePython)
  n = 0.003
FEATURE [App::DocumentObjectGroupPython] K_element002  label="K_element : 0.003"  # scripted group (container) (typed FeaturePython)
  n = 0.003
FEATURE [App::DocumentObjectGroupPython] G4_BRAIN_ICRP  # scripted group (container) (typed FeaturePython)
  Dunit = g/cm3
  Dvalue = 1.04
  Group = -> [H_element017,C_element018,N_element012,O_element017,Na_element004,P_element004,S_element006,Cl_element003,K_element002]
  conduct = 2
  density = 1
  expand = 3
  formula = G4_BRAIN_ICRP
  name = G4_BRAIN_ICRP
  specific = 4
FEATURE [App::DocumentObjectGroupPython] C_element019  label="C_element : 4"  # scripted group (container) (typed FeaturePython)
  n = 4
  ref = C_element
FEATURE [App::DocumentObjectGroupPython] H_element018  label="H_element : 010"  # scripted group (container) (typed FeaturePython)
  n = 10
  ref = H_element
FEATURE [App::DocumentObjectGroupPython] G4_BUTANE  # scripted group (container) (typed FeaturePython)
  Dunit = g/cm3
  Dvalue = 0.00249343
  Group = -> [C_element019,H_element018]
  conduct = 2
  density = 1
  expand = 3
  formula = G4_BUTANE
  name = G4_BUTANE
  specific = 4
FEATURE [App::DocumentObjectGroupPython] C_element020  label="C_element : 008"  # scripted group (container) (typed FeaturePython)
  n = 4
  ref = C_element
FEATURE [App::DocumentObjectGroupPython] H_element019  label="H_element : 011"  # scripted group (container) (typed FeaturePython)
  n = 10
  ref = H_element
FEATURE [App::DocumentObjectGroupPython] O_element018  label="O_element : 007"  # scripted group (container) (typed FeaturePython)
  n = 1
  ref = O_element
FEATURE [App::DocumentObjectGroupPython] G4_N_BUTYL_ALCOHOL  label="G4_N-BUTYL_ALCOHOL"  # scripted group (container) (typed FeaturePython)
  Dunit = g/cm3
  Dvalue = 0.8098
  Group = -> [C_element020,H_element019,O_element018]
  conduct = 2
  density = 1
  expand = 3
  formula = G4_N-BUTYL_ALCOHOL
  name = G4_N-BUTYL_ALCOHOL
  specific = 4
FEATURE [App::DocumentObjectGroupPython] H_element020  label="H_element : 0.025"  # scripted group (container) (typed FeaturePython)
  n = 0.02468
FEATURE [App::DocumentObjectGroupPython] C_element021  label="C_element : 0.502"  # scripted group (container) (typed FeaturePython)
  n = 0.501611
FEATURE [App::DocumentObjectGroupPython] O_element019  label="O_element : 0.005"  # scripted group (container) (typed FeaturePython)
  n = 0.004527
FEATURE [App::DocumentObjectGroupPython] F_element004  label="F_element : 0.465"  # scripted group (container) (typed FeaturePython)
  n = 0.465209
FEATURE [App::DocumentObjectGroupPython] Si_element001  label="Si_element : 0.004"  # scripted group (container) (typed FeaturePython)
  n = 0.003973
FEATURE [App::DocumentObjectGroupPython] G4_C_552  label="G4_C-552"  # scripted group (container) (typed FeaturePython)
  Dunit = g/cm3
  Dvalue = 1.76
  Group = -> [H_element020,C_element021,O_element019,F_element004,Si_element001]
  conduct = 2
  density = 1
  expand = 3
  formula = G4_C-552
  name = G4_C-552
  specific = 4
FEATURE [App::DocumentObjectGroupPython] Cd_element001  label="Cd_element : 1"  # scripted group (container) (typed FeaturePython)
  n = 1
  ref = Cd_element
FEATURE [App::DocumentObjectGroupPython] Te_element001  label="Te_element : 1"  # scripted group (container) (typed FeaturePython)
  n = 1
  ref = Te_element
FEATURE [App::DocumentObjectGroupPython] G4_CADMIUM_TELLURIDE  # scripted group (container) (typed FeaturePython)
  Dunit = g/cm3
  Dvalue = 6.2
  Group = -> [Cd_element001,Te_element001]
  conduct = 2
  density = 1
  expand = 3
  formula = G4_CADMIUM_TELLURIDE
  name = G4_CADMIUM_TELLURIDE
  specific = 4
FEATURE [App::DocumentObjectGroupPython] Cd_element002  label="Cd_element : 002"  # scripted group (container) (typed FeaturePython)
  n = 1
  ref = Cd_element
FEATURE [App::DocumentObjectGroupPython] W_element001  label="W_element : 1"  # scripted group (container) (typed FeaturePython)
  n = 1
  ref = W_element
FEATURE [App::DocumentObjectGroupPython] O_element020  label="O_element : 008"  # scripted group (container) (typed FeaturePython)
  n = 4
  ref = O_element
FEATURE [App::DocumentObjectGroupPython] G4_CADMIUM_TUNGSTATE  # scripted group (container) (typed FeaturePython)
  Dunit = g/cm3
  Dvalue = 7.9
  Group = -> [Cd_element002,W_element001,O_element020]
  conduct = 2
  density = 1
  expand = 3
  formula = G4_CADMIUM_TUNGSTATE
  name = G4_CADMIUM_TUNGSTATE
  specific = 4
FEATURE [App::DocumentObjectGroupPython] Ca_element005  label="Ca_element : 1"  # scripted group (container) (typed FeaturePython)
  n = 1
  ref = Ca_element
FEATURE [App::DocumentObjectGroupPython] C_element022  label="C_element : 009"  # scripted group (container) (typed FeaturePython)
  n = 1
  ref = C_element
FEATURE [App::DocumentObjectGroupPython] O_element021  label="O_element : 009"  # scripted group (container) (typed FeaturePython)
  n = 3
  ref = O_element
FEATURE [App::DocumentObjectGroupPython] G4_CALCIUM_CARBONATE  # scripted group (container) (typed FeaturePython)
  Dunit = g/cm3
  Dvalue = 2.8
  Group = -> [Ca_element005,C_element022,O_element021]
  conduct = 2
  density = 1
  expand = 3
  formula = G4_CALCIUM_CARBONATE
  name = G4_CALCIUM_CARBONATE
  specific = 4
FEATURE [App::DocumentObjectGroupPython] Ca_element006  label="Ca_element : 002"  # scripted group (container) (typed FeaturePython)
  n = 1
  ref = Ca_element
FEATURE [App::DocumentObjectGroupPython] F_element005  label="F_element : 003"  # scripted group (container) (typed FeaturePython)
  n = 2
  ref = F_element
FEATURE [App::DocumentObjectGroupPython] G4_CALCIUM_FLUORIDE  # scripted group (container) (typed FeaturePython)
  Dunit = g/cm3
  Dvalue = 3.18
  Group = -> [Ca_element006,F_element005]
  conduct = 2
  density = 1
  expand = 3
  formula = G4_CALCIUM_FLUORIDE
  name = G4_CALCIUM_FLUORIDE
  specific = 4
FEATURE [App::DocumentObjectGroupPython] Ca_element007  label="Ca_element : 003"  # scripted group (container) (typed FeaturePython)
  n = 1
  ref = Ca_element
FEATURE [App::DocumentObjectGroupPython] O_element022  label="O_element : 010"  # scripted group (container) (typed FeaturePython)
  n = 1
  ref = O_element
FEATURE [App::DocumentObjectGroupPython] G4_CALCIUM_OXIDE  # scripted group (container) (typed FeaturePython)
  Dunit = g/cm3
  Dvalue = 3.3
  Group = -> [Ca_element007,O_element022]
  conduct = 2
  density = 1
  expand = 3
  formula = G4_CALCIUM_OXIDE
  name = G4_CALCIUM_OXIDE
  specific = 4
FEATURE [App::DocumentObjectGroupPython] Ca_element008  label="Ca_element : 004"  # scripted group (container) (typed FeaturePython)
  n = 1
  ref = Ca_element
FEATURE [App::DocumentObjectGroupPython] S_element007  label="S_element : 002"  # scripted group (container) (typed FeaturePython)
  n = 1
  ref = S_element
FEATURE [App::DocumentObjectGroupPython] O_element023  label="O_element : 011"  # scripted group (container) (typed FeaturePython)
  n = 4
  ref = O_element
FEATURE [App::DocumentObjectGroupPython] G4_CALCIUM_SULFATE  # scripted group (container) (typed FeaturePython)
  Dunit = g/cm3
  Dvalue = 2.96
  Group = -> [Ca_element008,S_element007,O_element023]
  conduct = 2
  density = 1
  expand = 3
  formula = G4_CALCIUM_SULFATE
  name = G4_CALCIUM_SULFATE
  specific = 4
FEATURE [App::DocumentObjectGroupPython] Ca_element009  label="Ca_element : 005"  # scripted group (container) (typed FeaturePython)
  n = 1
  ref = Ca_element
FEATURE [App::DocumentObjectGroupPython] W_element002  label="W_element : 002"  # scripted group (container) (typed FeaturePython)
  n = 1
  ref = W_element
FEATURE [App::DocumentObjectGroupPython] O_element024  label="O_element : 012"  # scripted group (container) (typed FeaturePython)
  n = 4
  ref = O_element
FEATURE [App::DocumentObjectGroupPython] G4_CALCIUM_TUNGSTATE  # scripted group (container) (typed FeaturePython)
  Dunit = g/cm3
  Dvalue = 6.062
  Group = -> [Ca_element009,W_element002,O_element024]
  conduct = 2
  density = 1
  expand = 3
  formula = G4_CALCIUM_TUNGSTATE
  name = G4_CALCIUM_TUNGSTATE
  specific = 4
FEATURE [App::DocumentObjectGroupPython] C_element023  label="C_element : 010"  # scripted group (container) (typed FeaturePython)
  n = 1
  ref = C_element
FEATURE [App::DocumentObjectGroupPython] O_element025  label="O_element : 013"  # scripted group (container) (typed FeaturePython)
  n = 2
  ref = O_element
FEATURE [App::DocumentObjectGroupPython] G4_CARBON_DIOXIDE  # scripted group (container) (typed FeaturePython)
  Dunit = g/cm3
  Dvalue = 0.00184212
  Group = -> [C_element023,O_element025]
  conduct = 2
  density = 1
  expand = 3
  formula = G4_CARBON_DIOXIDE
  name = G4_CARBON_DIOXIDE
  specific = 4
FEATURE [App::DocumentObjectGroupPython] C_element024  label="C_element : 011"  # scripted group (container) (typed FeaturePython)
  n = 1
  ref = C_element
FEATURE [App::DocumentObjectGroupPython] Cl_element004  label="Cl_element : 4"  # scripted group (container) (typed FeaturePython)
  n = 4
  ref = Cl_element
FEATURE [App::DocumentObjectGroupPython] G4_CARBON_TETRACHLORIDE  # scripted group (container) (typed FeaturePython)
  Dunit = g/cm3
  Dvalue = 1.594
  Group = -> [C_element024,Cl_element004]
  conduct = 2
  density = 1
  expand = 3
  formula = G4_CARBON_TETRACHLORIDE
  name = G4_CARBON_TETRACHLORIDE
  specific = 4
FEATURE [App::DocumentObjectGroupPython] C_element025  label="C_element : 012"  # scripted group (container) (typed FeaturePython)
  n = 6
  ref = C_element
FEATURE [App::DocumentObjectGroupPython] H_element021  label="H_element : 012"  # scripted group (container) (typed FeaturePython)
  n = 10
  ref = H_element
FEATURE [App::DocumentObjectGroupPython] O_element026  label="O_element : 5"  # scripted group (container) (typed FeaturePython)
  n = 5
  ref = O_element
FEATURE [App::DocumentObjectGroupPython] G4_CELLULOSE_CELLOPHANE  # scripted group (container) (typed FeaturePython)
  Dunit = g/cm3
  Dvalue = 1.42
  Group = -> [C_element025,H_element021,O_element026]
  conduct = 2
  density = 1
  expand = 3
  formula = G4_CELLULOSE_CELLOPHANE
  name = G4_CELLULOSE_CELLOPHANE
  specific = 4
FEATURE [App::DocumentObjectGroupPython] H_element022  label="H_element : 0.067"  # scripted group (container) (typed FeaturePython)
  n = 0.067125
FEATURE [App::DocumentObjectGroupPython] C_element026  label="C_element : 0.545"  # scripted group (container) (typed FeaturePython)
  n = 0.545403
FEATURE [App::DocumentObjectGroupPython] O_element027  label="O_element : 0.387"  # scripted group (container) (typed FeaturePython)
  n = 0.387472
FEATURE [App::DocumentObjectGroupPython] G4_CELLULOSE_BUTYRATE  # scripted group (container) (typed FeaturePython)
  Dunit = g/cm3
  Dvalue = 1.2
  Group = -> [H_element022,C_element026,O_element027]
  conduct = 2
  density = 1
  expand = 3
  formula = G4_CELLULOSE_BUTYRATE
  name = G4_CELLULOSE_BUTYRATE
  specific = 4
FEATURE [App::DocumentObjectGroupPython] H_element023  label="H_element : 0.029"  # scripted group (container) (typed FeaturePython)
  n = 0.029216
FEATURE [App::DocumentObjectGroupPython] C_element027  label="C_element : 0.271"  # scripted group (container) (typed FeaturePython)
  n = 0.271296
FEATURE [App::DocumentObjectGroupPython] N_element013  label="N_element : 0.121"  # scripted group (container) (typed FeaturePython)
  n = 0.121276
FEATURE [App::DocumentObjectGroupPython] O_element028  label="O_element : 0.578"  # scripted group (container) (typed FeaturePython)
  n = 0.578212
FEATURE [App::DocumentObjectGroupPython] G4_CELLULOSE_NITRATE  # scripted group (container) (typed FeaturePython)
  Dunit = g/cm3
  Dvalue = 1.49
  Group = -> [H_element023,C_element027,N_element013,O_element028]
  conduct = 2
  density = 1
  expand = 3
  formula = G4_CELLULOSE_NITRATE
  name = G4_CELLULOSE_NITRATE
  specific = 4
FEATURE [App::DocumentObjectGroupPython] H_element024  label="H_element : 0.108"  # scripted group (container) (typed FeaturePython)
  n = 0.107596
FEATURE [App::DocumentObjectGroupPython] N_element014  label="N_element : 0.001"  # scripted group (container) (typed FeaturePython)
  n = 0.0008
FEATURE [App::DocumentObjectGroupPython] O_element029  label="O_element : 0.875"  # scripted group (container) (typed FeaturePython)
  n = 0.874976
FEATURE [App::DocumentObjectGroupPython] S_element008  label="S_element : 0.015"  # scripted group (container) (typed FeaturePython)
  n = 0.014627
FEATURE [App::DocumentObjectGroupPython] Ce_element001  label="Ce_element : 0.002"  # scripted group (container) (typed FeaturePython)
  n = 0.002001
FEATURE [App::DocumentObjectGroupPython] G4_CERIC_SULFATE  # scripted group (container) (typed FeaturePython)
  Dunit = g/cm3
  Dvalue = 1.03
  Group = -> [H_element024,N_element014,O_element029,S_element008,Ce_element001]
  conduct = 2
  density = 1
  expand = 3
  formula = G4_CERIC_SULFATE
  name = G4_CERIC_SULFATE
  specific = 4
FEATURE [App::DocumentObjectGroupPython] Cs_element001  label="Cs_element : 1"  # scripted group (container) (typed FeaturePython)
  n = 1
  ref = Cs_element
FEATURE [App::DocumentObjectGroupPython] F_element006  label="F_element : 1"  # scripted group (container) (typed FeaturePython)
  n = 1
  ref = F_element
FEATURE [App::DocumentObjectGroupPython] G4_CESIUM_FLUORIDE  # scripted group (container) (typed FeaturePython)
  Dunit = g/cm3
  Dvalue = 4.115
  Group = -> [Cs_element001,F_element006]
  conduct = 2
  density = 1
  expand = 3
  formula = G4_CESIUM_FLUORIDE
  name = G4_CESIUM_FLUORIDE
  specific = 4
FEATURE [App::DocumentObjectGroupPython] Cs_element002  label="Cs_element : 002"  # scripted group (container) (typed FeaturePython)
  n = 1
  ref = Cs_element
FEATURE [App::DocumentObjectGroupPython] I_element001  label="I_element : 1"  # scripted group (container) (typed FeaturePython)
  n = 1
  ref = I_element
FEATURE [App::DocumentObjectGroupPython] G4_CESIUM_IODIDE  # scripted group (container) (typed FeaturePython)
  Dunit = g/cm3
  Dvalue = 4.51
  Group = -> [Cs_element002,I_element001]
  conduct = 2
  density = 1
  expand = 3
  formula = G4_CESIUM_IODIDE
  name = G4_CESIUM_IODIDE
  specific = 4
FEATURE [App::DocumentObjectGroupPython] C_element028  label="C_element : 013"  # scripted group (container) (typed FeaturePython)
  n = 6
  ref = C_element
FEATURE [App::DocumentObjectGroupPython] H_element025  label="H_element : 013"  # scripted group (container) (typed FeaturePython)
  n = 5
  ref = H_element
FEATURE [App::DocumentObjectGroupPython] Cl_element005  label="Cl_element : 1"  # scripted group (container) (typed FeaturePython)
  n = 1
  ref = Cl_element
FEATURE [App::DocumentObjectGroupPython] G4_CHLOROBENZENE  # scripted group (container) (typed FeaturePython)
  Dunit = g/cm3
  Dvalue = 1.1058
  Group = -> [C_element028,H_element025,Cl_element005]
  conduct = 2
  density = 1
  expand = 3
  formula = G4_CHLOROBENZENE
  name = G4_CHLOROBENZENE
  specific = 4
FEATURE [App::DocumentObjectGroupPython] C_element029  label="C_element : 014"  # scripted group (container) (typed FeaturePython)
  n = 1
  ref = C_element
FEATURE [App::DocumentObjectGroupPython] H_element026  label="H_element : 1"  # scripted group (container) (typed FeaturePython)
  n = 1
  ref = H_element
FEATURE [App::DocumentObjectGroupPython] Cl_element006  label="Cl_element : 3"  # scripted group (container) (typed FeaturePython)
  n = 3
  ref = Cl_element
FEATURE [App::DocumentObjectGroupPython] G4_CHLOROFORM  # scripted group (container) (typed FeaturePython)
  Dunit = g/cm3
  Dvalue = 1.4832
  Group = -> [C_element029,H_element026,Cl_element006]
  conduct = 2
  density = 1
  expand = 3
  formula = G4_CHLOROFORM
  name = G4_CHLOROFORM
  specific = 4
FEATURE [App::DocumentObjectGroupPython] H_element027  label="H_element : 0.010"  # scripted group (container) (typed FeaturePython)
  n = 0.01
FEATURE [App::DocumentObjectGroupPython] C_element030  label="C_element : 0.001"  # scripted group (container) (typed FeaturePython)
  n = 0.001
FEATURE [App::DocumentObjectGroupPython] O_element030  label="O_element : 0.529"  # scripted group (container) (typed FeaturePython)
  n = 0.529107
FEATURE [App::DocumentObjectGroupPython] Na_element005  label="Na_element : 0.016"  # scripted group (container) (typed FeaturePython)
  n = 0.016
FEATURE [App::DocumentObjectGroupPython] Mg_element003  label="Mg_element : 0.004"  # scripted group (container) (typed FeaturePython)
  n = 0.002
FEATURE [App::DocumentObjectGroupPython] Al_element002  label="Al_element : 0.034"  # scripted group (container) (typed FeaturePython)
  n = 0.033872
FEATURE [App::DocumentObjectGroupPython] Si_element002  label="Si_element : 0.337"  # scripted group (container) (typed FeaturePython)
  n = 0.337021
FEATURE [App::DocumentObjectGroupPython] K_element003  label="K_element : 0.013"  # scripted group (container) (typed FeaturePython)
  n = 0.013
FEATURE [App::DocumentObjectGroupPython] Ca_element010  label="Ca_element : 0.044"  # scripted group (container) (typed FeaturePython)
  n = 0.044
FEATURE [App::DocumentObjectGroupPython] Fe_element002  label="Fe_element : 0.014"  # scripted group (container) (typed FeaturePython)
  n = 0.014
FEATURE [App::DocumentObjectGroupPython] G4_CONCRETE  # scripted group (container) (typed FeaturePython)
  Dunit = g/cm3
  Dvalue = 2.3
  Group = -> [H_element027,C_element030,O_element030,Na_element005,Mg_element003,Al_element002,Si_element002,K_element003,Ca_element010,Fe_element002]
  conduct = 2
  density = 1
  expand = 3
  formula = G4_CONCRETE
  name = G4_CONCRETE
  specific = 4
FEATURE [App::DocumentObjectGroupPython] C_element031  label="C_element : 015"  # scripted group (container) (typed FeaturePython)
  n = 6
  ref = C_element
FEATURE [App::DocumentObjectGroupPython] H_element028  label="H_element : 12"  # scripted group (container) (typed FeaturePython)
  n = 12
  ref = H_element
FEATURE [App::DocumentObjectGroupPython] G4_CYCLOHEXANE  # scripted group (container) (typed FeaturePython)
  Dunit = g/cm3
  Dvalue = 0.779
  Group = -> [C_element031,H_element028]
  conduct = 2
  density = 1
  expand = 3
  formula = G4_CYCLOHEXANE
  name = G4_CYCLOHEXANE
  specific = 4
FEATURE [App::DocumentObjectGroupPython] C_element032  label="C_element : 016"  # scripted group (container) (typed FeaturePython)
  n = 6
  ref = C_element
FEATURE [App::DocumentObjectGroupPython] H_element029  label="H_element : 4"  # scripted group (container) (typed FeaturePython)
  n = 4
  ref = H_element
FEATURE [App::DocumentObjectGroupPython] Cl_element007  label="Cl_element : 2"  # scripted group (container) (typed FeaturePython)
  n = 2
  ref = Cl_element
FEATURE [App::DocumentObjectGroupPython] G4_1_2_DICHLOROBENZENE  label="G4_1.2-DICHLOROBENZENE"  # scripted group (container) (typed FeaturePython)
  Dunit = g/cm3
  Dvalue = 1.3048
  Group = -> [C_element032,H_element029,Cl_element007]
  conduct = 2
  density = 1
  expand = 3
  formula = G4_1.2-DICHLOROBENZENE
  name = G4_1.2-DICHLOROBENZENE
  specific = 4
FEATURE [App::DocumentObjectGroupPython] C_element033  label="C_element : 017"  # scripted group (container) (typed FeaturePython)
  n = 4
  ref = C_element
FEATURE [App::DocumentObjectGroupPython] H_element030  label="H_element : 8"  # scripted group (container) (typed FeaturePython)
  n = 8
  ref = H_element
FEATURE [App::DocumentObjectGroupPython] O_element031  label="O_element : 014"  # scripted group (container) (typed FeaturePython)
  n = 1
  ref = O_element
FEATURE [App::DocumentObjectGroupPython] Cl_element008  label="Cl_element : 005"  # scripted group (container) (typed FeaturePython)
  n = 2
  ref = Cl_element
FEATURE [App::DocumentObjectGroupPython] G4_DICHLORODIETHYL_ETHER  # scripted group (container) (typed FeaturePython)
  Dunit = g/cm3
  Dvalue = 1.2199
  Group = -> [C_element033,H_element030,O_element031,Cl_element008]
  conduct = 2
  density = 1
  expand = 3
  formula = G4_DICHLORODIETHYL_ETHER
  name = G4_DICHLORODIETHYL_ETHER
  specific = 4
FEATURE [App::DocumentObjectGroupPython] C_element034  label="C_element : 018"  # scripted group (container) (typed FeaturePython)
  n = 2
  ref = C_element
FEATURE [App::DocumentObjectGroupPython] H_element031  label="H_element : 014"  # scripted group (container) (typed FeaturePython)
  n = 4
  ref = H_element
FEATURE [App::DocumentObjectGroupPython] Cl_element009  label="Cl_element : 006"  # scripted group (container) (typed FeaturePython)
  n = 2
  ref = Cl_element
FEATURE [App::DocumentObjectGroupPython] G4_1_2_DICHLOROETHANE  label="G4_1.2-DICHLOROETHANE"  # scripted group (container) (typed FeaturePython)
  Dunit = g/cm3
  Dvalue = 1.2351
  Group = -> [C_element034,H_element031,Cl_element009]
  conduct = 2
  density = 1
  expand = 3
  formula = G4_1.2-DICHLOROETHANE
  name = G4_1.2-DICHLOROETHANE
  specific = 4
FEATURE [App::DocumentObjectGroupPython] C_element035  label="C_element : 019"  # scripted group (container) (typed FeaturePython)
  n = 4
  ref = C_element
FEATURE [App::DocumentObjectGroupPython] H_element032  label="H_element : 015"  # scripted group (container) (typed FeaturePython)
  n = 10
  ref = H_element
FEATURE [App::DocumentObjectGroupPython] O_element032  label="O_element : 015"  # scripted group (container) (typed FeaturePython)
  n = 1
  ref = O_element
FEATURE [App::DocumentObjectGroupPython] G4_DIETHYL_ETHER  # scripted group (container) (typed FeaturePython)
  Dunit = g/cm3
  Dvalue = 0.71378
  Group = -> [C_element035,H_element032,O_element032]
  conduct = 2
  density = 1
  expand = 3
  formula = G4_DIETHYL_ETHER
  name = G4_DIETHYL_ETHER
  specific = 4
FEATURE [App::DocumentObjectGroupPython] C_element036  label="C_element : 020"  # scripted group (container) (typed FeaturePython)
  n = 3
  ref = C_element
FEATURE [App::DocumentObjectGroupPython] H_element033  label="H_element : 016"  # scripted group (container) (typed FeaturePython)
  n = 7
  ref = H_element
FEATURE [App::DocumentObjectGroupPython] N_element015  label="N_element : 008"  # scripted group (container) (typed FeaturePython)
  n = 1
  ref = N_element
FEATURE [App::DocumentObjectGroupPython] O_element033  label="O_element : 016"  # scripted group (container) (typed FeaturePython)
  n = 1
  ref = O_element
FEATURE [App::DocumentObjectGroupPython] G4_N_N_DIMETHYL_FORMAMIDE  label="G4_N.N-DIMETHYL_FORMAMIDE"  # scripted group (container) (typed FeaturePython)
  Dunit = g/cm3
  Dvalue = 0.9487
  Group = -> [C_element036,H_element033,N_element015,O_element033]
  conduct = 2
  density = 1
  expand = 3
  formula = G4_N.N-DIMETHYL_FORMAMIDE
  name = G4_N.N-DIMETHYL_FORMAMIDE
  specific = 4
FEATURE [App::DocumentObjectGroupPython] C_element037  label="C_element : 021"  # scripted group (container) (typed FeaturePython)
  n = 2
  ref = C_element
FEATURE [App::DocumentObjectGroupPython] H_element034  label="H_element : 017"  # scripted group (container) (typed FeaturePython)
  n = 6
  ref = H_element
FEATURE [App::DocumentObjectGroupPython] O_element034  label="O_element : 017"  # scripted group (container) (typed FeaturePython)
  n = 1
  ref = O_element
FEATURE [App::DocumentObjectGroupPython] S_element009  label="S_element : 003"  # scripted group (container) (typed FeaturePython)
  n = 1
  ref = S_element
FEATURE [App::DocumentObjectGroupPython] G4_DIMETHYL_SULFOXIDE  # scripted group (container) (typed FeaturePython)
  Dunit = g/cm3
  Dvalue = 1.1014
  Group = -> [C_element037,H_element034,O_element034,S_element009]
  conduct = 2
  density = 1
  expand = 3
  formula = G4_DIMETHYL_SULFOXIDE
  name = G4_DIMETHYL_SULFOXIDE
  specific = 4
FEATURE [App::DocumentObjectGroupPython] C_element038  label="C_element : 022"  # scripted group (container) (typed FeaturePython)
  n = 2
  ref = C_element
FEATURE [App::DocumentObjectGroupPython] H_element035  label="H_element : 018"  # scripted group (container) (typed FeaturePython)
  n = 6
  ref = H_element
FEATURE [App::DocumentObjectGroupPython] G4_ETHANE  # scripted group (container) (typed FeaturePython)
  Dunit = g/cm3
  Dvalue = 0.00125324
  Group = -> [C_element038,H_element035]
  conduct = 2
  density = 1
  expand = 3
  formula = G4_ETHANE
  name = G4_ETHANE
  specific = 4
FEATURE [App::DocumentObjectGroupPython] C_element039  label="C_element : 023"  # scripted group (container) (typed FeaturePython)
  n = 2
  ref = C_element
FEATURE [App::DocumentObjectGroupPython] H_element036  label="H_element : 019"  # scripted group (container) (typed FeaturePython)
  n = 6
  ref = H_element
FEATURE [App::DocumentObjectGroupPython] O_element035  label="O_element : 018"  # scripted group (container) (typed FeaturePython)
  n = 1
  ref = O_element
FEATURE [App::DocumentObjectGroupPython] G4_ETHYL_ALCOHOL  # scripted group (container) (typed FeaturePython)
  Dunit = g/cm3
  Dvalue = 0.7893
  Group = -> [C_element039,H_element036,O_element035]
  conduct = 2
  density = 1
  expand = 3
  formula = G4_ETHYL_ALCOHOL
  name = G4_ETHYL_ALCOHOL
  specific = 4
FEATURE [App::DocumentObjectGroupPython] H_element037  label="H_element : 0.090"  # scripted group (container) (typed FeaturePython)
  n = 0.090027
FEATURE [App::DocumentObjectGroupPython] C_element040  label="C_element : 0.585"  # scripted group (container) (typed FeaturePython)
  n = 0.585182
FEATURE [App::DocumentObjectGroupPython] O_element036  label="O_element : 0.325"  # scripted group (container) (typed FeaturePython)
  n = 0.324791
FEATURE [App::DocumentObjectGroupPython] G4_ETHYL_CELLULOSE  # scripted group (container) (typed FeaturePython)
  Dunit = g/cm3
  Dvalue = 1.13
  Group = -> [H_element037,C_element040,O_element036]
  conduct = 2
  density = 1
  expand = 3
  formula = G4_ETHYL_CELLULOSE
  name = G4_ETHYL_CELLULOSE
  specific = 4
FEATURE [App::DocumentObjectGroupPython] C_element041  label="C_element : 024"  # scripted group (container) (typed FeaturePython)
  n = 2
  ref = C_element
FEATURE [App::DocumentObjectGroupPython] H_element038  label="H_element : 020"  # scripted group (container) (typed FeaturePython)
  n = 4
  ref = H_element
FEATURE [App::DocumentObjectGroupPython] G4_ETHYLENE  # scripted group (container) (typed FeaturePython)
  Dunit = g/cm3
  Dvalue = 0.00117497
  Group = -> [C_element041,H_element038]
  conduct = 2
  density = 1
  expand = 3
  formula = G4_ETHYLENE
  name = G4_ETHYLENE
  specific = 4
FEATURE [App::DocumentObjectGroupPython] H_element039  label="H_element : 0.096"  # scripted group (container) (typed FeaturePython)
  n = 0.096
FEATURE [App::DocumentObjectGroupPython] C_element042  label="C_element : 0.195"  # scripted group (container) (typed FeaturePython)
  n = 0.195
FEATURE [App::DocumentObjectGroupPython] N_element016  label="N_element : 0.057"  # scripted group (container) (typed FeaturePython)
  n = 0.057
FEATURE [App::DocumentObjectGroupPython] O_element037  label="O_element : 0.646"  # scripted group (container) (typed FeaturePython)
  n = 0.646
FEATURE [App::DocumentObjectGroupPython] Na_element006  label="Na_element : 0.017"  # scripted group (container) (typed FeaturePython)
  n = 0.001
FEATURE [App::DocumentObjectGroupPython] P_element005  label="P_element : 0.104"  # scripted group (container) (typed FeaturePython)
  n = 0.001
FEATURE [App::DocumentObjectGroupPython] S_element010  label="S_element : 0.016"  # scripted group (container) (typed FeaturePython)
  n = 0.003
FEATURE [App::DocumentObjectGroupPython] Cl_element010  label="Cl_element : 0.005"  # scripted group (container) (typed FeaturePython)
  n = 0.001
FEATURE [App::DocumentObjectGroupPython] G4_EYE_LENS_ICRP  # scripted group (container) (typed FeaturePython)
  Dunit = g/cm3
  Dvalue = 1.07
  Group = -> [H_element039,C_element042,N_element016,O_element037,Na_element006,P_element005,S_element010,Cl_element010]
  conduct = 2
  density = 1
  expand = 3
  formula = G4_EYE_LENS_ICRP
  name = G4_EYE_LENS_ICRP
  specific = 4
FEATURE [App::DocumentObjectGroupPython] Fe_element003  label="Fe_element : 2"  # scripted group (container) (typed FeaturePython)
  n = 2
  ref = Fe_element
FEATURE [App::DocumentObjectGroupPython] O_element038  label="O_element : 019"  # scripted group (container) (typed FeaturePython)
  n = 3
  ref = O_element
FEATURE [App::DocumentObjectGroupPython] G4_FERRIC_OXIDE  # scripted group (container) (typed FeaturePython)
  Dunit = g/cm3
  Dvalue = 5.2
  Group = -> [Fe_element003,O_element038]
  conduct = 2
  density = 1
  expand = 3
  formula = G4_FERRIC_OXIDE
  name = G4_FERRIC_OXIDE
  specific = 4
FEATURE [App::DocumentObjectGroupPython] Fe_element004  label="Fe_element : 1"  # scripted group (container) (typed FeaturePython)
  n = 1
  ref = Fe_element
FEATURE [App::DocumentObjectGroupPython] B_element003  label="B_element : 1"  # scripted group (container) (typed FeaturePython)
  n = 1
  ref = B_element
FEATURE [App::DocumentObjectGroupPython] G4_FERROBORIDE  # scripted group (container) (typed FeaturePython)
  Dunit = g/cm3
  Dvalue = 7.15
  Group = -> [Fe_element004,B_element003]
  conduct = 2
  density = 1
  expand = 3
  formula = G4_FERROBORIDE
  name = G4_FERROBORIDE
  specific = 4
FEATURE [App::DocumentObjectGroupPython] Fe_element005  label="Fe_element : 003"  # scripted group (container) (typed FeaturePython)
  n = 1
  ref = Fe_element
FEATURE [App::DocumentObjectGroupPython] O_element039  label="O_element : 020"  # scripted group (container) (typed FeaturePython)
  n = 1
  ref = O_element
FEATURE [App::DocumentObjectGroupPython] G4_FERROUS_OXIDE  # scripted group (container) (typed FeaturePython)
  Dunit = g/cm3
  Dvalue = 5.7
  Group = -> [Fe_element005,O_element039]
  conduct = 2
  density = 1
  expand = 3
  formula = G4_FERROUS_OXIDE
  name = G4_FERROUS_OXIDE
  specific = 4
FEATURE [App::DocumentObjectGroupPython] H_element040  label="H_element : 0.115"  # scripted group (container) (typed FeaturePython)
  n = 0.108259
FEATURE [App::DocumentObjectGroupPython] N_element017  label="N_element : 0.000"  # scripted group (container) (typed FeaturePython)
  n = 2.7e-05
FEATURE [App::DocumentObjectGroupPython] O_element040  label="O_element : 0.879"  # scripted group (container) (typed FeaturePython)
  n = 0.878636
FEATURE [App::DocumentObjectGroupPython] Na_element007  label="Na_element : 0.000"  # scripted group (container) (typed FeaturePython)
  n = 2.2e-05
FEATURE [App::DocumentObjectGroupPython] S_element011  label="S_element : 0.013"  # scripted group (container) (typed FeaturePython)
  n = 0.012968
FEATURE [App::DocumentObjectGroupPython] Cl_element011  label="Cl_element : 0.000"  # scripted group (container) (typed FeaturePython)
  n = 3.4e-05
FEATURE [App::DocumentObjectGroupPython] Fe_element006  label="Fe_element : 0.000"  # scripted group (container) (typed FeaturePython)
  n = 5.4e-05
FEATURE [App::DocumentObjectGroupPython] G4_FERROUS_SULFATE  # scripted group (container) (typed FeaturePython)
  Dunit = g/cm3
  Dvalue = 1.024
  Group = -> [H_element040,N_element017,O_element040,Na_element007,S_element011,Cl_element011,Fe_element006]
  conduct = 2
  density = 1
  expand = 3
  formula = G4_FERROUS_SULFATE
  name = G4_FERROUS_SULFATE
  specific = 4
FEATURE [App::DocumentObjectGroupPython] C_element043  label="C_element : 0.099"  # scripted group (container) (typed FeaturePython)
  n = 0.099335
FEATURE [App::DocumentObjectGroupPython] F_element007  label="F_element : 0.314"  # scripted group (container) (typed FeaturePython)
  n = 0.314247
FEATURE [App::DocumentObjectGroupPython] Cl_element012  label="Cl_element : 0.586"  # scripted group (container) (typed FeaturePython)
  n = 0.586418
FEATURE [App::DocumentObjectGroupPython] G4_FREON_12  label="G4_FREON-12"  # scripted group (container) (typed FeaturePython)
  Dunit = g/cm3
  Dvalue = 1.12
  Group = -> [C_element043,F_element007,Cl_element012]
  conduct = 2
  density = 1
  expand = 3
  formula = G4_FREON-12
  name = G4_FREON-12
  specific = 4
FEATURE [App::DocumentObjectGroupPython] C_element044  label="C_element : 0.057"  # scripted group (container) (typed FeaturePython)
  n = 0.057245
FEATURE [App::DocumentObjectGroupPython] F_element008  label="F_element : 0.181"  # scripted group (container) (typed FeaturePython)
  n = 0.181096
FEATURE [App::DocumentObjectGroupPython] Br_element001  label="Br_element : 0.762"  # scripted group (container) (typed FeaturePython)
  n = 0.761659
FEATURE [App::DocumentObjectGroupPython] G4_FREON_12B2  label="G4_FREON-12B2"  # scripted group (container) (typed FeaturePython)
  Dunit = g/cm3
  Dvalue = 1.8
  Group = -> [C_element044,F_element008,Br_element001]
  conduct = 2
  density = 1
  expand = 3
  formula = G4_FREON-12B2
  name = G4_FREON-12B2
  specific = 4
FEATURE [App::DocumentObjectGroupPython] C_element045  label="C_element : 0.115"  # scripted group (container) (typed FeaturePython)
  n = 0.114983
FEATURE [App::DocumentObjectGroupPython] F_element009  label="F_element : 0.546"  # scripted group (container) (typed FeaturePython)
  n = 0.545621
FEATURE [App::DocumentObjectGroupPython] Cl_element013  label="Cl_element : 0.339"  # scripted group (container) (typed FeaturePython)
  n = 0.339396
FEATURE [App::DocumentObjectGroupPython] G4_FREON_13  label="G4_FREON-13"  # scripted group (container) (typed FeaturePython)
  Dunit = g/cm3
  Dvalue = 0.95
  Group = -> [C_element045,F_element009,Cl_element013]
  conduct = 2
  density = 1
  expand = 3
  formula = G4_FREON-13
  name = G4_FREON-13
  specific = 4
FEATURE [App::DocumentObjectGroupPython] C_element046  label="C_element : 025"  # scripted group (container) (typed FeaturePython)
  n = 1
  ref = C_element
FEATURE [App::DocumentObjectGroupPython] F_element010  label="F_element : 3"  # scripted group (container) (typed FeaturePython)
  n = 3
  ref = F_element
FEATURE [App::DocumentObjectGroupPython] Br_element002  label="Br_element : 1"  # scripted group (container) (typed FeaturePython)
  n = 1
  ref = Br_element
FEATURE [App::DocumentObjectGroupPython] G4_FREON_13B1  label="G4_FREON-13B1"  # scripted group (container) (typed FeaturePython)
  Dunit = g/cm3
  Dvalue = 1.5
  Group = -> [C_element046,F_element010,Br_element002]
  conduct = 2
  density = 1
  expand = 3
  formula = G4_FREON-13B1
  name = G4_FREON-13B1
  specific = 4
FEATURE [App::DocumentObjectGroupPython] C_element047  label="C_element : 0.061"  # scripted group (container) (typed FeaturePython)
  n = 0.061309
FEATURE [App::DocumentObjectGroupPython] F_element011  label="F_element : 0.291"  # scripted group (container) (typed FeaturePython)
  n = 0.290924
FEATURE [App::DocumentObjectGroupPython] I_element002  label="I_element : 0.648"  # scripted group (container) (typed FeaturePython)
  n = 0.647767
FEATURE [App::DocumentObjectGroupPython] G4_FREON_13I1  label="G4_FREON-13I1"  # scripted group (container) (typed FeaturePython)
  Dunit = g/cm3
  Dvalue = 1.8
  Group = -> [C_element047,F_element011,I_element002]
  conduct = 2
  density = 1
  expand = 3
  formula = G4_FREON-13I1
  name = G4_FREON-13I1
  specific = 4
FEATURE [App::DocumentObjectGroupPython] Gd_element001  label="Gd_element : 2"  # scripted group (container) (typed FeaturePython)
  n = 2
  ref = Gd_element
FEATURE [App::DocumentObjectGroupPython] O_element041  label="O_element : 021"  # scripted group (container) (typed FeaturePython)
  n = 2
  ref = O_element
FEATURE [App::DocumentObjectGroupPython] S_element012  label="S_element : 004"  # scripted group (container) (typed FeaturePython)
  n = 1
  ref = S_element
FEATURE [App::DocumentObjectGroupPython] G4_GADOLINIUM_OXYSULFIDE  # scripted group (container) (typed FeaturePython)
  Dunit = g/cm3
  Dvalue = 7.44
  Group = -> [Gd_element001,O_element041,S_element012]
  conduct = 2
  density = 1
  expand = 3
  formula = G4_GADOLINIUM_OXYSULFIDE
  name = G4_GADOLINIUM_OXYSULFIDE
  specific = 4
FEATURE [App::DocumentObjectGroupPython] Ga_element001  label="Ga_element : 1"  # scripted group (container) (typed FeaturePython)
  n = 1
  ref = Ga_element
FEATURE [App::DocumentObjectGroupPython] As_element001  label="As_element : 1"  # scripted group (container) (typed FeaturePython)
  n = 1
  ref = As_element
FEATURE [App::DocumentObjectGroupPython] G4_GALLIUM_ARSENIDE  # scripted group (container) (typed FeaturePython)
  Dunit = g/cm3
  Dvalue = 5.31
  Group = -> [Ga_element001,As_element001]
  conduct = 2
  density = 1
  expand = 3
  formula = G4_GALLIUM_ARSENIDE
  name = G4_GALLIUM_ARSENIDE
  specific = 4
FEATURE [App::DocumentObjectGroupPython] H_element041  label="H_element : 0.081"  # scripted group (container) (typed FeaturePython)
  n = 0.08118
FEATURE [App::DocumentObjectGroupPython] C_element048  label="C_element : 0.416"  # scripted group (container) (typed FeaturePython)
  n = 0.41606
FEATURE [App::DocumentObjectGroupPython] N_element018  label="N_element : 0.111"  # scripted group (container) (typed FeaturePython)
  n = 0.11124
FEATURE [App::DocumentObjectGroupPython] O_element042  label="O_element : 0.381"  # scripted group (container) (typed FeaturePython)
  n = 0.38064
FEATURE [App::DocumentObjectGroupPython] S_element013  label="S_element : 0.011"  # scripted group (container) (typed FeaturePython)
  n = 0.01088
FEATURE [App::DocumentObjectGroupPython] G4_GEL_PHOTO_EMULSION  # scripted group (container) (typed FeaturePython)
  Dunit = g/cm3
  Dvalue = 1.2914
  Group = -> [H_element041,C_element048,N_element018,O_element042,S_element013]
  conduct = 2
  density = 1
  expand = 3
  formula = G4_GEL_PHOTO_EMULSION
  name = G4_GEL_PHOTO_EMULSION
  specific = 4
FEATURE [App::DocumentObjectGroupPython] B_element004  label="B_element : 0.040"  # scripted group (container) (typed FeaturePython)
  n = 0.0400639
FEATURE [App::DocumentObjectGroupPython] O_element043  label="O_element : 0.540"  # scripted group (container) (typed FeaturePython)
  n = 0.539561
FEATURE [App::DocumentObjectGroupPython] Na_element008  label="Na_element : 0.028"  # scripted group (container) (typed FeaturePython)
  n = 0.0281909
FEATURE [App::DocumentObjectGroupPython] Al_element003  label="Al_element : 0.012"  # scripted group (container) (typed FeaturePython)
  n = 0.011644
FEATURE [App::DocumentObjectGroupPython] Si_element003  label="Si_element : 0.377"  # scripted group (container) (typed FeaturePython)
  n = 0.377219
FEATURE [App::DocumentObjectGroupPython] K_element004  label="K_element : 0.014"  # scripted group (container) (typed FeaturePython)
  n = 0.00332099
FEATURE [App::DocumentObjectGroupPython] G4_Pyrex_Glass  # scripted group (container) (typed FeaturePython)
  Dunit = g/cm3
  Dvalue = 2.23
  Group = -> [B_element004,O_element043,Na_element008,Al_element003,Si_element003,K_element004]
  conduct = 2
  density = 1
  expand = 3
  formula = G4_Pyrex_Glass
  name = G4_Pyrex_Glass
  specific = 4
FEATURE [App::DocumentObjectGroupPython] O_element044  label="O_element : 0.156"  # scripted group (container) (typed FeaturePython)
  n = 0.156453
FEATURE [App::DocumentObjectGroupPython] Si_element004  label="Si_element : 0.081"  # scripted group (container) (typed FeaturePython)
  n = 0.080866
FEATURE [App::DocumentObjectGroupPython] Ti_element001  label="Ti_element : 0.008"  # scripted group (container) (typed FeaturePython)
  n = 0.008092
FEATURE [App::DocumentObjectGroupPython] As_element002  label="As_element : 0.003"  # scripted group (container) (typed FeaturePython)
  n = 0.002651
FEATURE [App::DocumentObjectGroupPython] Pb_element001  label="Pb_element : 0.752"  # scripted group (container) (typed FeaturePython)
  n = 0.751938
FEATURE [App::DocumentObjectGroupPython] G4_GLASS_LEAD  # scripted group (container) (typed FeaturePython)
  Dunit = g/cm3
  Dvalue = 6.22
  Group = -> [O_element044,Si_element004,Ti_element001,As_element002,Pb_element001]
  conduct = 2
  density = 1
  expand = 3
  formula = G4_GLASS_LEAD
  name = G4_GLASS_LEAD
  specific = 4
FEATURE [App::DocumentObjectGroupPython] O_element045  label="O_element : 0.460"  # scripted group (container) (typed FeaturePython)
  n = 0.4598
FEATURE [App::DocumentObjectGroupPython] Na_element009  label="Na_element : 0.096"  # scripted group (container) (typed FeaturePython)
  n = 0.0964411
FEATURE [App::DocumentObjectGroupPython] Si_element005  label="Si_element : 0.378"  # scripted group (container) (typed FeaturePython)
  n = 0.336553
FEATURE [App::DocumentObjectGroupPython] Ca_element011  label="Ca_element : 0.107"  # scripted group (container) (typed FeaturePython)
  n = 0.107205
FEATURE [App::DocumentObjectGroupPython] G4_GLASS_PLATE  # scripted group (container) (typed FeaturePython)
  Dunit = g/cm3
  Dvalue = 2.4
  Group = -> [O_element045,Na_element009,Si_element005,Ca_element011]
  conduct = 2
  density = 1
  expand = 3
  formula = G4_GLASS_PLATE
  name = G4_GLASS_PLATE
  specific = 4
FEATURE [App::DocumentObjectGroupPython] C_element049  label="C_element : 026"  # scripted group (container) (typed FeaturePython)
  n = 5
  ref = C_element
FEATURE [App::DocumentObjectGroupPython] H_element042  label="H_element : 021"  # scripted group (container) (typed FeaturePython)
  n = 10
  ref = H_element
FEATURE [App::DocumentObjectGroupPython] N_element019  label="N_element : 2"  # scripted group (container) (typed FeaturePython)
  n = 2
  ref = N_element
FEATURE [App::DocumentObjectGroupPython] O_element046  label="O_element : 022"  # scripted group (container) (typed FeaturePython)
  n = 3
  ref = O_element
FEATURE [App::DocumentObjectGroupPython] G4_GLUTAMINE  # scripted group (container) (typed FeaturePython)
  Dunit = g/cm3
  Dvalue = 1.46
  Group = -> [C_element049,H_element042,N_element019,O_element046]
  conduct = 2
  density = 1
  expand = 3
  formula = G4_GLUTAMINE
  name = G4_GLUTAMINE
  specific = 4
FEATURE [App::DocumentObjectGroupPython] C_element050  label="C_element : 027"  # scripted group (container) (typed FeaturePython)
  n = 3
  ref = C_element
FEATURE [App::DocumentObjectGroupPython] H_element043  label="H_element : 022"  # scripted group (container) (typed FeaturePython)
  n = 8
  ref = H_element
FEATURE [App::DocumentObjectGroupPython] O_element047  label="O_element : 023"  # scripted group (container) (typed FeaturePython)
  n = 3
  ref = O_element
FEATURE [App::DocumentObjectGroupPython] G4_GLYCEROL  # scripted group (container) (typed FeaturePython)
  Dunit = g/cm3
  Dvalue = 1.2613
  Group = -> [C_element050,H_element043,O_element047]
  conduct = 2
  density = 1
  expand = 3
  formula = G4_GLYCEROL
  name = G4_GLYCEROL
  specific = 4
FEATURE [App::DocumentObjectGroupPython] C_element051  label="C_element : 028"  # scripted group (container) (typed FeaturePython)
  n = 5
  ref = C_element
FEATURE [App::DocumentObjectGroupPython] H_element044  label="H_element : 023"  # scripted group (container) (typed FeaturePython)
  n = 5
  ref = H_element
FEATURE [App::DocumentObjectGroupPython] N_element020  label="N_element : 009"  # scripted group (container) (typed FeaturePython)
  n = 5
  ref = N_element
FEATURE [App::DocumentObjectGroupPython] O_element048  label="O_element : 024"  # scripted group (container) (typed FeaturePython)
  n = 1
  ref = O_element
FEATURE [App::DocumentObjectGroupPython] G4_GUANINE  # scripted group (container) (typed FeaturePython)
  Dunit = g/cm3
  Dvalue = 2.2
  Group = -> [C_element051,H_element044,N_element020,O_element048]
  conduct = 2
  density = 1
  expand = 3
  formula = G4_GUANINE
  name = G4_GUANINE
  specific = 4
FEATURE [App::DocumentObjectGroupPython] Ca_element012  label="Ca_element : 006"  # scripted group (container) (typed FeaturePython)
  n = 1
  ref = Ca_element
FEATURE [App::DocumentObjectGroupPython] S_element014  label="S_element : 005"  # scripted group (container) (typed FeaturePython)
  n = 1
  ref = S_element
FEATURE [App::DocumentObjectGroupPython] O_element049  label="O_element : 6"  # scripted group (container) (typed FeaturePython)
  n = 6
  ref = O_element
FEATURE [App::DocumentObjectGroupPython] H_element045  label="H_element : 024"  # scripted group (container) (typed FeaturePython)
  n = 4
  ref = H_element
FEATURE [App::DocumentObjectGroupPython] G4_GYPSUM  # scripted group (container) (typed FeaturePython)
  Dunit = g/cm3
  Dvalue = 2.32
  Group = -> [Ca_element012,S_element014,O_element049,H_element045]
  conduct = 2
  density = 1
  expand = 3
  formula = G4_GYPSUM
  name = G4_GYPSUM
  specific = 4
FEATURE [App::DocumentObjectGroupPython] C_element052  label="C_element : 7"  # scripted group (container) (typed FeaturePython)
  n = 7
  ref = C_element
FEATURE [App::DocumentObjectGroupPython] H_element046  label="H_element : 16"  # scripted group (container) (typed FeaturePython)
  n = 16
  ref = H_element
FEATURE [App::DocumentObjectGroupPython] G4_N_HEPTANE  label="G4_N-HEPTANE"  # scripted group (container) (typed FeaturePython)
  Dunit = g/cm3
  Dvalue = 0.68376
  Group = -> [C_element052,H_element046]
  conduct = 2
  density = 1
  expand = 3
  formula = G4_N-HEPTANE
  name = G4_N-HEPTANE
  specific = 4
FEATURE [App::DocumentObjectGroupPython] C_element053  label="C_element : 029"  # scripted group (container) (typed FeaturePython)
  n = 6
  ref = C_element
FEATURE [App::DocumentObjectGroupPython] H_element047  label="H_element : 14"  # scripted group (container) (typed FeaturePython)
  n = 14
  ref = H_element
FEATURE [App::DocumentObjectGroupPython] G4_N_HEXANE  label="G4_N-HEXANE"  # scripted group (container) (typed FeaturePython)
  Dunit = g/cm3
  Dvalue = 0.6603
  Group = -> [C_element053,H_element047]
  conduct = 2
  density = 1
  expand = 3
  formula = G4_N-HEXANE
  name = G4_N-HEXANE
  specific = 4
FEATURE [App::DocumentObjectGroupPython] C_element054  label="C_element : 22"  # scripted group (container) (typed FeaturePython)
  n = 22
  ref = C_element
FEATURE [App::DocumentObjectGroupPython] H_element048  label="H_element : 025"  # scripted group (container) (typed FeaturePython)
  n = 10
  ref = H_element
FEATURE [App::DocumentObjectGroupPython] N_element021  label="N_element : 010"  # scripted group (container) (typed FeaturePython)
  n = 2
  ref = N_element
FEATURE [App::DocumentObjectGroupPython] O_element050  label="O_element : 025"  # scripted group (container) (typed FeaturePython)
  n = 5
  ref = O_element
FEATURE [App::DocumentObjectGroupPython] G4_KAPTON  # scripted group (container) (typed FeaturePython)
  Dunit = g/cm3
  Dvalue = 1.42
  Group = -> [C_element054,H_element048,N_element021,O_element050]
  conduct = 2
  density = 1
  expand = 3
  formula = G4_KAPTON
  name = G4_KAPTON
  specific = 4
FEATURE [App::DocumentObjectGroupPython] La_element001  label="La_element : 1"  # scripted group (container) (typed FeaturePython)
  n = 1
  ref = La_element
FEATURE [App::DocumentObjectGroupPython] Br_element003  label="Br_element : 002"  # scripted group (container) (typed FeaturePython)
  n = 1
  ref = Br_element
FEATURE [App::DocumentObjectGroupPython] O_element051  label="O_element : 026"  # scripted group (container) (typed FeaturePython)
  n = 1
  ref = O_element
FEATURE [App::DocumentObjectGroupPython] G4_LANTHANUM_OXYBROMIDE  # scripted group (container) (typed FeaturePython)
  Dunit = g/cm3
  Dvalue = 6.28
  Group = -> [La_element001,Br_element003,O_element051]
  conduct = 2
  density = 1
  expand = 3
  formula = G4_LANTHANUM_OXYBROMIDE
  name = G4_LANTHANUM_OXYBROMIDE
  specific = 4
FEATURE [App::DocumentObjectGroupPython] La_element002  label="La_element : 2"  # scripted group (container) (typed FeaturePython)
  n = 2
  ref = La_element
FEATURE [App::DocumentObjectGroupPython] O_element052  label="O_element : 027"  # scripted group (container) (typed FeaturePython)
  n = 2
  ref = O_element
FEATURE [App::DocumentObjectGroupPython] S_element015  label="S_element : 006"  # scripted group (container) (typed FeaturePython)
  n = 1
  ref = S_element
FEATURE [App::DocumentObjectGroupPython] G4_LANTHANUM_OXYSULFIDE  # scripted group (container) (typed FeaturePython)
  Dunit = g/cm3
  Dvalue = 5.86
  Group = -> [La_element002,O_element052,S_element015]
  conduct = 2
  density = 1
  expand = 3
  formula = G4_LANTHANUM_OXYSULFIDE
  name = G4_LANTHANUM_OXYSULFIDE
  specific = 4
FEATURE [App::DocumentObjectGroupPython] O_element053  label="O_element : 0.072"  # scripted group (container) (typed FeaturePython)
  n = 0.071682
FEATURE [App::DocumentObjectGroupPython] Pb_element002  label="Pb_element : 0.928"  # scripted group (container) (typed FeaturePython)
  n = 0.928318
FEATURE [App::DocumentObjectGroupPython] G4_LEAD_OXIDE  # scripted group (container) (typed FeaturePython)
  Dunit = g/cm3
  Dvalue = 9.53
  Group = -> [O_element053,Pb_element002]
  conduct = 2
  density = 1
  expand = 3
  formula = G4_LEAD_OXIDE
  name = G4_LEAD_OXIDE
  specific = 4
FEATURE [App::DocumentObjectGroupPython] Li_element001  label="Li_element : 1"  # scripted group (container) (typed FeaturePython)
  n = 1
  ref = Li_element
FEATURE [App::DocumentObjectGroupPython] N_element022  label="N_element : 011"  # scripted group (container) (typed FeaturePython)
  n = 1
  ref = N_element
FEATURE [App::DocumentObjectGroupPython] H_element049  label="H_element : 026"  # scripted group (container) (typed FeaturePython)
  n = 2
  ref = H_element
FEATURE [App::DocumentObjectGroupPython] G4_LITHIUM_AMIDE  # scripted group (container) (typed FeaturePython)
  Dunit = g/cm3
  Dvalue = 1.178
  Group = -> [Li_element001,N_element022,H_element049]
  conduct = 2
  density = 1
  expand = 3
  formula = G4_LITHIUM_AMIDE
  name = G4_LITHIUM_AMIDE
  specific = 4
FEATURE [App::DocumentObjectGroupPython] Li_element002  label="Li_element : 2"  # scripted group (container) (typed FeaturePython)
  n = 2
  ref = Li_element
FEATURE [App::DocumentObjectGroupPython] C_element055  label="C_element : 030"  # scripted group (container) (typed FeaturePython)
  n = 1
  ref = C_element
FEATURE [App::DocumentObjectGroupPython] O_element054  label="O_element : 028"  # scripted group (container) (typed FeaturePython)
  n = 3
  ref = O_element
FEATURE [App::DocumentObjectGroupPython] G4_LITHIUM_CARBONATE  # scripted group (container) (typed FeaturePython)
  Dunit = g/cm3
  Dvalue = 2.11
  Group = -> [Li_element002,C_element055,O_element054]
  conduct = 2
  density = 1
  expand = 3
  formula = G4_LITHIUM_CARBONATE
  name = G4_LITHIUM_CARBONATE
  specific = 4
FEATURE [App::DocumentObjectGroupPython] Li_element003  label="Li_element : 003"  # scripted group (container) (typed FeaturePython)
  n = 1
  ref = Li_element
FEATURE [App::DocumentObjectGroupPython] F_element012  label="F_element : 004"  # scripted group (container) (typed FeaturePython)
  n = 1
  ref = F_element
FEATURE [App::DocumentObjectGroupPython] G4_LITHIUM_FLUORIDE  # scripted group (container) (typed FeaturePython)
  Dunit = g/cm3
  Dvalue = 2.635
  Group = -> [Li_element003,F_element012]
  conduct = 2
  density = 1
  expand = 3
  formula = G4_LITHIUM_FLUORIDE
  name = G4_LITHIUM_FLUORIDE
  specific = 4
FEATURE [App::DocumentObjectGroupPython] Li_element004  label="Li_element : 004"  # scripted group (container) (typed FeaturePython)
  n = 1
  ref = Li_element
FEATURE [App::DocumentObjectGroupPython] H_element050  label="H_element : 027"  # scripted group (container) (typed FeaturePython)
  n = 1
  ref = H_element
FEATURE [App::DocumentObjectGroupPython] G4_LITHIUM_HYDRIDE  # scripted group (container) (typed FeaturePython)
  Dunit = g/cm3
  Dvalue = 0.82
  Group = -> [Li_element004,H_element050]
  conduct = 2
  density = 1
  expand = 3
  formula = G4_LITHIUM_HYDRIDE
  name = G4_LITHIUM_HYDRIDE
  specific = 4
FEATURE [App::DocumentObjectGroupPython] Li_element005  label="Li_element : 005"  # scripted group (container) (typed FeaturePython)
  n = 1
  ref = Li_element
FEATURE [App::DocumentObjectGroupPython] I_element003  label="I_element : 002"  # scripted group (container) (typed FeaturePython)
  n = 1
  ref = I_element
FEATURE [App::DocumentObjectGroupPython] G4_LITHIUM_IODIDE  # scripted group (container) (typed FeaturePython)
  Dunit = g/cm3
  Dvalue = 3.494
  Group = -> [Li_element005,I_element003]
  conduct = 2
  density = 1
  expand = 3
  formula = G4_LITHIUM_IODIDE
  name = G4_LITHIUM_IODIDE
  specific = 4
FEATURE [App::DocumentObjectGroupPython] Li_element006  label="Li_element : 006"  # scripted group (container) (typed FeaturePython)
  n = 2
  ref = Li_element
FEATURE [App::DocumentObjectGroupPython] O_element055  label="O_element : 029"  # scripted group (container) (typed FeaturePython)
  n = 1
  ref = O_element
FEATURE [App::DocumentObjectGroupPython] G4_LITHIUM_OXIDE  # scripted group (container) (typed FeaturePython)
  Dunit = g/cm3
  Dvalue = 2.013
  Group = -> [Li_element006,O_element055]
  conduct = 2
  density = 1
  expand = 3
  formula = G4_LITHIUM_OXIDE
  name = G4_LITHIUM_OXIDE
  specific = 4
FEATURE [App::DocumentObjectGroupPython] Li_element007  label="Li_element : 007"  # scripted group (container) (typed FeaturePython)
  n = 2
  ref = Li_element
FEATURE [App::DocumentObjectGroupPython] B_element005  label="B_element : 005"  # scripted group (container) (typed FeaturePython)
  n = 4
  ref = B_element
FEATURE [App::DocumentObjectGroupPython] O_element056  label="O_element : 7"  # scripted group (container) (typed FeaturePython)
  n = 7
  ref = O_element
FEATURE [App::DocumentObjectGroupPython] G4_LITHIUM_TETRABORATE  # scripted group (container) (typed FeaturePython)
  Dunit = g/cm3
  Dvalue = 2.44
  Group = -> [Li_element007,B_element005,O_element056]
  conduct = 2
  density = 1
  expand = 3
  formula = G4_LITHIUM_TETRABORATE
  name = G4_LITHIUM_TETRABORATE
  specific = 4
FEATURE [App::DocumentObjectGroupPython] H_element051  label="H_element : 0.105"  # scripted group (container) (typed FeaturePython)
  n = 0.105
FEATURE [App::DocumentObjectGroupPython] C_element056  label="C_element : 0.083"  # scripted group (container) (typed FeaturePython)
  n = 0.083
FEATURE [App::DocumentObjectGroupPython] N_element023  label="N_element : 0.023"  # scripted group (container) (typed FeaturePython)
  n = 0.023
FEATURE [App::DocumentObjectGroupPython] O_element057  label="O_element : 0.779"  # scripted group (container) (typed FeaturePython)
  n = 0.779
FEATURE [App::DocumentObjectGroupPython] Na_element010  label="Na_element : 0.097"  # scripted group (container) (typed FeaturePython)
  n = 0.002
FEATURE [App::DocumentObjectGroupPython] P_element006  label="P_element : 0.105"  # scripted group (container) (typed FeaturePython)
  n = 0.001
FEATURE [App::DocumentObjectGroupPython] S_element016  label="S_element : 0.017"  # scripted group (container) (typed FeaturePython)
  n = 0.002
FEATURE [App::DocumentObjectGroupPython] Cl_element014  label="Cl_element : 0.587"  # scripted group (container) (typed FeaturePython)
  n = 0.003
FEATURE [App::DocumentObjectGroupPython] K_element005  label="K_element : 0.015"  # scripted group (container) (typed FeaturePython)
  n = 0.002
FEATURE [App::DocumentObjectGroupPython] G4_LUNG_ICRP  # scripted group (container) (typed FeaturePython)
  Dunit = g/cm3
  Dvalue = 1.04
  Group = -> [H_element051,C_element056,N_element023,O_element057,Na_element010,P_element006,S_element016,Cl_element014,K_element005]
  conduct = 2
  density = 1
  expand = 3
  formula = G4_LUNG_ICRP
  name = G4_LUNG_ICRP
  specific = 4
FEATURE [App::DocumentObjectGroupPython] H_element052  label="H_element : 0.116"  # scripted group (container) (typed FeaturePython)
  n = 0.114318
FEATURE [App::DocumentObjectGroupPython] C_element057  label="C_element : 0.656"  # scripted group (container) (typed FeaturePython)
  n = 0.655824
FEATURE [App::DocumentObjectGroupPython] O_element058  label="O_element : 0.092"  # scripted group (container) (typed FeaturePython)
  n = 0.0921831
FEATURE [App::DocumentObjectGroupPython] Mg_element004  label="Mg_element : 0.135"  # scripted group (container) (typed FeaturePython)
  n = 0.134792
FEATURE [App::DocumentObjectGroupPython] Ca_element013  label="Ca_element : 0.003"  # scripted group (container) (typed FeaturePython)
  n = 0.002883
FEATURE [App::DocumentObjectGroupPython] G4_M3_WAX  # scripted group (container) (typed FeaturePython)
  Dunit = g/cm3
  Dvalue = 1.05
  Group = -> [H_element052,C_element057,O_element058,Mg_element004,Ca_element013]
  conduct = 2
  density = 1
  expand = 3
  formula = G4_M3_WAX
  name = G4_M3_WAX
  specific = 4
FEATURE [App::DocumentObjectGroupPython] Mg_element005  label="Mg_element : 1"  # scripted group (container) (typed FeaturePython)
  n = 1
  ref = Mg_element
FEATURE [App::DocumentObjectGroupPython] C_element058  label="C_element : 031"  # scripted group (container) (typed FeaturePython)
  n = 1
  ref = C_element
FEATURE [App::DocumentObjectGroupPython] O_element059  label="O_element : 030"  # scripted group (container) (typed FeaturePython)
  n = 3
  ref = O_element
FEATURE [App::DocumentObjectGroupPython] G4_MAGNESIUM_CARBONATE  # scripted group (container) (typed FeaturePython)
  Dunit = g/cm3
  Dvalue = 2.958
  Group = -> [Mg_element005,C_element058,O_element059]
  conduct = 2
  density = 1
  expand = 3
  formula = G4_MAGNESIUM_CARBONATE
  name = G4_MAGNESIUM_CARBONATE
  specific = 4
FEATURE [App::DocumentObjectGroupPython] Mg_element006  label="Mg_element : 002"  # scripted group (container) (typed FeaturePython)
  n = 1
  ref = Mg_element
FEATURE [App::DocumentObjectGroupPython] F_element013  label="F_element : 005"  # scripted group (container) (typed FeaturePython)
  n = 2
  ref = F_element
FEATURE [App::DocumentObjectGroupPython] G4_MAGNESIUM_FLUORIDE  # scripted group (container) (typed FeaturePython)
  Dunit = g/cm3
  Dvalue = 3
  Group = -> [Mg_element006,F_element013]
  conduct = 2
  density = 1
  expand = 3
  formula = G4_MAGNESIUM_FLUORIDE
  name = G4_MAGNESIUM_FLUORIDE
  specific = 4
FEATURE [App::DocumentObjectGroupPython] Mg_element007  label="Mg_element : 003"  # scripted group (container) (typed FeaturePython)
  n = 1
  ref = Mg_element
FEATURE [App::DocumentObjectGroupPython] O_element060  label="O_element : 031"  # scripted group (container) (typed FeaturePython)
  n = 1
  ref = O_element
FEATURE [App::DocumentObjectGroupPython] G4_MAGNESIUM_OXIDE  # scripted group (container) (typed FeaturePython)
  Dunit = g/cm3
  Dvalue = 3.58
  Group = -> [Mg_element007,O_element060]
  conduct = 2
  density = 1
  expand = 3
  formula = G4_MAGNESIUM_OXIDE
  name = G4_MAGNESIUM_OXIDE
  specific = 4
FEATURE [App::DocumentObjectGroupPython] Mg_element008  label="Mg_element : 004"  # scripted group (container) (typed FeaturePython)
  n = 1
  ref = Mg_element
FEATURE [App::DocumentObjectGroupPython] B_element006  label="B_element : 006"  # scripted group (container) (typed FeaturePython)
  n = 4
  ref = B_element
FEATURE [App::DocumentObjectGroupPython] O_element061  label="O_element : 032"  # scripted group (container) (typed FeaturePython)
  n = 7
  ref = O_element
FEATURE [App::DocumentObjectGroupPython] G4_MAGNESIUM_TETRABORATE  # scripted group (container) (typed FeaturePython)
  Dunit = g/cm3
  Dvalue = 2.53
  Group = -> [Mg_element008,B_element006,O_element061]
  conduct = 2
  density = 1
  expand = 3
  formula = G4_MAGNESIUM_TETRABORATE
  name = G4_MAGNESIUM_TETRABORATE
  specific = 4
FEATURE [App::DocumentObjectGroupPython] Hg_element001  label="Hg_element : 1"  # scripted group (container) (typed FeaturePython)
  n = 1
  ref = Hg_element
FEATURE [App::DocumentObjectGroupPython] I_element004  label="I_element : 2"  # scripted group (container) (typed FeaturePython)
  n = 2
  ref = I_element
FEATURE [App::DocumentObjectGroupPython] G4_MERCURIC_IODIDE  # scripted group (container) (typed FeaturePython)
  Dunit = g/cm3
  Dvalue = 6.36
  Group = -> [Hg_element001,I_element004]
  conduct = 2
  density = 1
  expand = 3
  formula = G4_MERCURIC_IODIDE
  name = G4_MERCURIC_IODIDE
  specific = 4
FEATURE [App::DocumentObjectGroupPython] C_element059  label="C_element : 032"  # scripted group (container) (typed FeaturePython)
  n = 1
  ref = C_element
FEATURE [App::DocumentObjectGroupPython] H_element053  label="H_element : 028"  # scripted group (container) (typed FeaturePython)
  n = 4
  ref = H_element
FEATURE [App::DocumentObjectGroupPython] G4_METHANE  # scripted group (container) (typed FeaturePython)
  Dunit = g/cm3
  Dvalue = 0.000667151
  Group = -> [C_element059,H_element053]
  conduct = 2
  density = 1
  expand = 3
  formula = G4_METHANE
  name = G4_METHANE
  specific = 4
FEATURE [App::DocumentObjectGroupPython] C_element060  label="C_element : 033"  # scripted group (container) (typed FeaturePython)
  n = 1
  ref = C_element
FEATURE [App::DocumentObjectGroupPython] H_element054  label="H_element : 029"  # scripted group (container) (typed FeaturePython)
  n = 4
  ref = H_element
FEATURE [App::DocumentObjectGroupPython] O_element062  label="O_element : 033"  # scripted group (container) (typed FeaturePython)
  n = 1
  ref = O_element
FEATURE [App::DocumentObjectGroupPython] G4_METHANOL  # scripted group (container) (typed FeaturePython)
  Dunit = g/cm3
  Dvalue = 0.7914
  Group = -> [C_element060,H_element054,O_element062]
  conduct = 2
  density = 1
  expand = 3
  formula = G4_METHANOL
  name = G4_METHANOL
  specific = 4
FEATURE [App::DocumentObjectGroupPython] H_element055  label="H_element : 0.134"  # scripted group (container) (typed FeaturePython)
  n = 0.13404
FEATURE [App::DocumentObjectGroupPython] C_element061  label="C_element : 0.778"  # scripted group (container) (typed FeaturePython)
  n = 0.77796
FEATURE [App::DocumentObjectGroupPython] O_element063  label="O_element : 0.035"  # scripted group (container) (typed FeaturePython)
  n = 0.03502
FEATURE [App::DocumentObjectGroupPython] Mg_element009  label="Mg_element : 0.039"  # scripted group (container) (typed FeaturePython)
  n = 0.038594
FEATURE [App::DocumentObjectGroupPython] Ti_element002  label="Ti_element : 0.014"  # scripted group (container) (typed FeaturePython)
  n = 0.014386
FEATURE [App::DocumentObjectGroupPython] G4_MIX_D_WAX  # scripted group (container) (typed FeaturePython)
  Dunit = g/cm3
  Dvalue = 0.99
  Group = -> [H_element055,C_element061,O_element063,Mg_element009,Ti_element002]
  conduct = 2
  density = 1
  expand = 3
  formula = G4_MIX_D_WAX
  name = G4_MIX_D_WAX
  specific = 4
FEATURE [App::DocumentObjectGroupPython] H_element056  label="H_element : 0.135"  # scripted group (container) (typed FeaturePython)
  n = 0.081192
FEATURE [App::DocumentObjectGroupPython] C_element062  label="C_element : 0.583"  # scripted group (container) (typed FeaturePython)
  n = 0.583442
FEATURE [App::DocumentObjectGroupPython] N_element024  label="N_element : 0.018"  # scripted group (container) (typed FeaturePython)
  n = 0.017798
FEATURE [App::DocumentObjectGroupPython] O_element064  label="O_element : 0.186"  # scripted group (container) (typed FeaturePython)
  n = 0.186381
FEATURE [App::DocumentObjectGroupPython] Mg_element010  label="Mg_element : 0.130"  # scripted group (container) (typed FeaturePython)
  n = 0.130287
FEATURE [App::DocumentObjectGroupPython] Cl_element015  label="Cl_element : 0.588"  # scripted group (container) (typed FeaturePython)
  n = 0.0009
FEATURE [App::DocumentObjectGroupPython] G4_MS20_TISSUE  # scripted group (container) (typed FeaturePython)
  Dunit = g/cm3
  Dvalue = 1
  Group = -> [H_element056,C_element062,N_element024,O_element064,Mg_element010,Cl_element015]
  conduct = 2
  density = 1
  expand = 3
  formula = G4_MS20_TISSUE
  name = G4_MS20_TISSUE
  specific = 4
FEATURE [App::DocumentObjectGroupPython] H_element057  label="H_element : 0.136"  # scripted group (container) (typed FeaturePython)
  n = 0.102
FEATURE [App::DocumentObjectGroupPython] C_element063  label="C_element : 0.143"  # scripted group (container) (typed FeaturePython)
  n = 0.143
FEATURE [App::DocumentObjectGroupPython] N_element025  label="N_element : 0.034"  # scripted group (container) (typed FeaturePython)
  n = 0.034
FEATURE [App::DocumentObjectGroupPython] O_element065  label="O_element : 0.710"  # scripted group (container) (typed FeaturePython)
  n = 0.71
FEATURE [App::DocumentObjectGroupPython] Na_element011  label="Na_element : 0.098"  # scripted group (container) (typed FeaturePython)
  n = 0.001
FEATURE [App::DocumentObjectGroupPython] P_element007  label="P_element : 0.002"  # scripted group (container) (typed FeaturePython)
  n = 0.002
FEATURE [App::DocumentObjectGroupPython] S_element017  label="S_element : 0.018"  # scripted group (container) (typed FeaturePython)
  n = 0.003
FEATURE [App::DocumentObjectGroupPython] Cl_element016  label="Cl_element : 0.589"  # scripted group (container) (typed FeaturePython)
  n = 0.001
FEATURE [App::DocumentObjectGroupPython] K_element006  label="K_element : 0.004"  # scripted group (container) (typed FeaturePython)
  n = 0.004
FEATURE [App::DocumentObjectGroupPython] G4_MUSCLE_SKELETAL_ICRP  # scripted group (container) (typed FeaturePython)
  Dunit = g/cm3
  Dvalue = 1.05
  Group = -> [H_element057,C_element063,N_element025,O_element065,Na_element011,P_element007,S_element017,Cl_element016,K_element006]
  conduct = 2
  density = 1
  expand = 3
  formula = G4_MUSCLE_SKELETAL_ICRP
  name = G4_MUSCLE_SKELETAL_ICRP
  specific = 4
FEATURE [App::DocumentObjectGroupPython] H_element058  label="H_element : 0.137"  # scripted group (container) (typed FeaturePython)
  n = 0.102102
FEATURE [App::DocumentObjectGroupPython] C_element064  label="C_element : 0.123"  # scripted group (container) (typed FeaturePython)
  n = 0.123123
FEATURE [App::DocumentObjectGroupPython] N_element026  label="N_element : 0.756"  # scripted group (container) (typed FeaturePython)
  n = 0.035035
FEATURE [App::DocumentObjectGroupPython] O_element066  label="O_element : 0.730"  # scripted group (container) (typed FeaturePython)
  n = 0.72973
FEATURE [App::DocumentObjectGroupPython] Na_element012  label="Na_element : 0.099"  # scripted group (container) (typed FeaturePython)
  n = 0.001001
FEATURE [App::DocumentObjectGroupPython] P_element008  label="P_element : 0.106"  # scripted group (container) (typed FeaturePython)
  n = 0.002002
FEATURE [App::DocumentObjectGroupPython] S_element018  label="S_element : 0.019"  # scripted group (container) (typed FeaturePython)
  n = 0.004004
FEATURE [App::DocumentObjectGroupPython] K_element007  label="K_element : 0.016"  # scripted group (container) (typed FeaturePython)
  n = 0.003003
FEATURE [App::DocumentObjectGroupPython] G4_MUSCLE_STRIATED_ICRU  # scripted group (container) (typed FeaturePython)
  Dunit = g/cm3
  Dvalue = 1.04
  Group = -> [H_element058,C_element064,N_element026,O_element066,Na_element012,P_element008,S_element018,K_element007]
  conduct = 2
  density = 1
  expand = 3
  formula = G4_MUSCLE_STRIATED_ICRU
  name = G4_MUSCLE_STRIATED_ICRU
  specific = 4
FEATURE [App::DocumentObjectGroupPython] H_element059  label="H_element : 0.098"  # scripted group (container) (typed FeaturePython)
  n = 0.0982341
FEATURE [App::DocumentObjectGroupPython] C_element065  label="C_element : 0.156"  # scripted group (container) (typed FeaturePython)
  n = 0.156214
FEATURE [App::DocumentObjectGroupPython] N_element027  label="N_element : 0.757"  # scripted group (container) (typed FeaturePython)
  n = 0.035451
FEATURE [App::DocumentObjectGroupPython] O_element067  label="O_element : 0.880"  # scripted group (container) (typed FeaturePython)
  n = 0.710101
FEATURE [App::DocumentObjectGroupPython] G4_MUSCLE_WITH_SUCROSE  # scripted group (container) (typed FeaturePython)
  Dunit = g/cm3
  Dvalue = 1.11
  Group = -> [H_element059,C_element065,N_element027,O_element067]
  conduct = 2
  density = 1
  expand = 3
  formula = G4_MUSCLE_WITH_SUCROSE
  name = G4_MUSCLE_WITH_SUCROSE
  specific = 4
FEATURE [App::DocumentObjectGroupPython] H_element060  label="H_element : 0.138"  # scripted group (container) (typed FeaturePython)
  n = 0.101969
FEATURE [App::DocumentObjectGroupPython] C_element066  label="C_element : 0.120"  # scripted group (container) (typed FeaturePython)
  n = 0.120058
FEATURE [App::DocumentObjectGroupPython] N_element028  label="N_element : 0.758"  # scripted group (container) (typed FeaturePython)
  n = 0.035451
FEATURE [App::DocumentObjectGroupPython] O_element068  label="O_element : 0.743"  # scripted group (container) (typed FeaturePython)
  n = 0.742522
FEATURE [App::DocumentObjectGroupPython] G4_MUSCLE_WITHOUT_SUCROSE  # scripted group (container) (typed FeaturePython)
  Dunit = g/cm3
  Dvalue = 1.07
  Group = -> [H_element060,C_element066,N_element028,O_element068]
  conduct = 2
  density = 1
  expand = 3
  formula = G4_MUSCLE_WITHOUT_SUCROSE
  name = G4_MUSCLE_WITHOUT_SUCROSE
  specific = 4
FEATURE [App::DocumentObjectGroupPython] C_element067  label="C_element : 10"  # scripted group (container) (typed FeaturePython)
  n = 10
  ref = C_element
FEATURE [App::DocumentObjectGroupPython] H_element061  label="H_element : 030"  # scripted group (container) (typed FeaturePython)
  n = 8
  ref = H_element
FEATURE [App::DocumentObjectGroupPython] G4_NAPHTHALENE  # scripted group (container) (typed FeaturePython)
  Dunit = g/cm3
  Dvalue = 1.145
  Group = -> [C_element067,H_element061]
  conduct = 2
  density = 1
  expand = 3
  formula = G4_NAPHTHALENE
  name = G4_NAPHTHALENE
  specific = 4
FEATURE [App::DocumentObjectGroupPython] C_element068  label="C_element : 034"  # scripted group (container) (typed FeaturePython)
  n = 6
  ref = C_element
FEATURE [App::DocumentObjectGroupPython] H_element062  label="H_element : 031"  # scripted group (container) (typed FeaturePython)
  n = 5
  ref = H_element
FEATURE [App::DocumentObjectGroupPython] N_element029  label="N_element : 012"  # scripted group (container) (typed FeaturePython)
  n = 1
  ref = N_element
FEATURE [App::DocumentObjectGroupPython] O_element069  label="O_element : 034"  # scripted group (container) (typed FeaturePython)
  n = 2
  ref = O_element
FEATURE [App::DocumentObjectGroupPython] G4_NITROBENZENE  # scripted group (container) (typed FeaturePython)
  Dunit = g/cm3
  Dvalue = 1.19867
  Group = -> [C_element068,H_element062,N_element029,O_element069]
  conduct = 2
  density = 1
  expand = 3
  formula = G4_NITROBENZENE
  name = G4_NITROBENZENE
  specific = 4
FEATURE [App::DocumentObjectGroupPython] N_element030  label="N_element : 013"  # scripted group (container) (typed FeaturePython)
  n = 2
  ref = N_element
FEATURE [App::DocumentObjectGroupPython] O_element070  label="O_element : 035"  # scripted group (container) (typed FeaturePython)
  n = 1
  ref = O_element
FEATURE [App::DocumentObjectGroupPython] G4_NITROUS_OXIDE  # scripted group (container) (typed FeaturePython)
  Dunit = g/cm3
  Dvalue = 0.00183094
  Group = -> [N_element030,O_element070]
  conduct = 2
  density = 1
  expand = 3
  formula = G4_NITROUS_OXIDE
  name = G4_NITROUS_OXIDE
  specific = 4
FEATURE [App::DocumentObjectGroupPython] H_element063  label="H_element : 0.104"  # scripted group (container) (typed FeaturePython)
  n = 0.103509
FEATURE [App::DocumentObjectGroupPython] C_element069  label="C_element : 0.648"  # scripted group (container) (typed FeaturePython)
  n = 0.648416
FEATURE [App::DocumentObjectGroupPython] N_element031  label="N_element : 0.100"  # scripted group (container) (typed FeaturePython)
  n = 0.0995361
FEATURE [App::DocumentObjectGroupPython] O_element071  label="O_element : 0.149"  # scripted group (container) (typed FeaturePython)
  n = 0.148539
FEATURE [App::DocumentObjectGroupPython] G4_NYLON_8062  label="G4_NYLON-8062"  # scripted group (container) (typed FeaturePython)
  Dunit = g/cm3
  Dvalue = 1.08
  Group = -> [H_element063,C_element069,N_element031,O_element071]
  conduct = 2
  density = 1
  expand = 3
  formula = G4_NYLON-8062
  name = G4_NYLON-8062
  specific = 4
FEATURE [App::DocumentObjectGroupPython] C_element070  label="C_element : 035"  # scripted group (container) (typed FeaturePython)
  n = 6
  ref = C_element
FEATURE [App::DocumentObjectGroupPython] H_element064  label="H_element : 11"  # scripted group (container) (typed FeaturePython)
  n = 11
  ref = H_element
FEATURE [App::DocumentObjectGroupPython] N_element032  label="N_element : 014"  # scripted group (container) (typed FeaturePython)
  n = 1
  ref = N_element
FEATURE [App::DocumentObjectGroupPython] O_element072  label="O_element : 036"  # scripted group (container) (typed FeaturePython)
  n = 1
  ref = O_element
FEATURE [App::DocumentObjectGroupPython] G4_NYLON_6_6  label="G4_NYLON-6-6"  # scripted group (container) (typed FeaturePython)
  Dunit = g/cm3
  Dvalue = 1.14
  Group = -> [C_element070,H_element064,N_element032,O_element072]
  conduct = 2
  density = 1
  expand = 3
  formula = G4_NYLON-6-6
  name = G4_NYLON-6-6
  specific = 4
FEATURE [App::DocumentObjectGroupPython] H_element065  label="H_element : 0.139"  # scripted group (container) (typed FeaturePython)
  n = 0.107062
FEATURE [App::DocumentObjectGroupPython] C_element071  label="C_element : 0.680"  # scripted group (container) (typed FeaturePython)
  n = 0.680449
FEATURE [App::DocumentObjectGroupPython] N_element033  label="N_element : 0.099"  # scripted group (container) (typed FeaturePython)
  n = 0.099189
FEATURE [App::DocumentObjectGroupPython] O_element073  label="O_element : 0.113"  # scripted group (container) (typed FeaturePython)
  n = 0.1133
FEATURE [App::DocumentObjectGroupPython] G4_NYLON_6_10  label="G4_NYLON-6-10"  # scripted group (container) (typed FeaturePython)
  Dunit = g/cm3
  Dvalue = 1.14
  Group = -> [H_element065,C_element071,N_element033,O_element073]
  conduct = 2
  density = 1
  expand = 3
  formula = G4_NYLON-6-10
  name = G4_NYLON-6-10
  specific = 4
FEATURE [App::DocumentObjectGroupPython] H_element066  label="H_element : 0.140"  # scripted group (container) (typed FeaturePython)
  n = 0.115476
FEATURE [App::DocumentObjectGroupPython] C_element072  label="C_element : 0.721"  # scripted group (container) (typed FeaturePython)
  n = 0.720818
FEATURE [App::DocumentObjectGroupPython] N_element034  label="N_element : 0.076"  # scripted group (container) (typed FeaturePython)
  n = 0.0764169
FEATURE [App::DocumentObjectGroupPython] O_element074  label="O_element : 0.087"  # scripted group (container) (typed FeaturePython)
  n = 0.0872889
FEATURE [App::DocumentObjectGroupPython] G4_NYLON_11_RILSAN  label="G4_NYLON-11_RILSAN"  # scripted group (container) (typed FeaturePython)
  Dunit = g/cm3
  Dvalue = 1.425
  Group = -> [H_element066,C_element072,N_element034,O_element074]
  conduct = 2
  density = 1
  expand = 3
  formula = G4_NYLON-11_RILSAN
  name = G4_NYLON-11_RILSAN
  specific = 4
FEATURE [App::DocumentObjectGroupPython] C_element073  label="C_element : 8"  # scripted group (container) (typed FeaturePython)
  n = 8
  ref = C_element
FEATURE [App::DocumentObjectGroupPython] H_element067  label="H_element : 18"  # scripted group (container) (typed FeaturePython)
  n = 18
  ref = H_element
FEATURE [App::DocumentObjectGroupPython] G4_OCTANE  # scripted group (container) (typed FeaturePython)
  Dunit = g/cm3
  Dvalue = 0.7026
  Group = -> [C_element073,H_element067]
  conduct = 2
  density = 1
  expand = 3
  formula = G4_OCTANE
  name = G4_OCTANE
  specific = 4
FEATURE [App::DocumentObjectGroupPython] C_element074  label="C_element : 25"  # scripted group (container) (typed FeaturePython)
  n = 25
  ref = C_element
FEATURE [App::DocumentObjectGroupPython] H_element068  label="H_element : 52"  # scripted group (container) (typed FeaturePython)
  n = 52
  ref = H_element
FEATURE [App::DocumentObjectGroupPython] G4_PARAFFIN  # scripted group (container) (typed FeaturePython)
  Dunit = g/cm3
  Dvalue = 0.93
  Group = -> [C_element074,H_element068]
  conduct = 2
  density = 1
  expand = 3
  formula = G4_PARAFFIN
  name = G4_PARAFFIN
  specific = 4
FEATURE [App::DocumentObjectGroupPython] C_element075  label="C_element : 036"  # scripted group (container) (typed FeaturePython)
  n = 5
  ref = C_element
FEATURE [App::DocumentObjectGroupPython] H_element069  label="H_element : 032"  # scripted group (container) (typed FeaturePython)
  n = 12
  ref = H_element
FEATURE [App::DocumentObjectGroupPython] G4_N_PENTANE  label="G4_N-PENTANE"  # scripted group (container) (typed FeaturePython)
  Dunit = g/cm3
  Dvalue = 0.6262
  Group = -> [C_element075,H_element069]
  conduct = 2
  density = 1
  expand = 3
  formula = G4_N-PENTANE
  name = G4_N-PENTANE
  specific = 4
FEATURE [App::DocumentObjectGroupPython] H_element070  label="H_element : 0.014"  # scripted group (container) (typed FeaturePython)
  n = 0.0141
FEATURE [App::DocumentObjectGroupPython] C_element076  label="C_element : 0.072"  # scripted group (container) (typed FeaturePython)
  n = 0.072261
FEATURE [App::DocumentObjectGroupPython] N_element035  label="N_element : 0.019"  # scripted group (container) (typed FeaturePython)
  n = 0.01932
FEATURE [App::DocumentObjectGroupPython] O_element075  label="O_element : 0.066"  # scripted group (container) (typed FeaturePython)
  n = 0.066101
FEATURE [App::DocumentObjectGroupPython] S_element019  label="S_element : 0.020"  # scripted group (container) (typed FeaturePython)
  n = 0.00189
FEATURE [App::DocumentObjectGroupPython] Br_element004  label="Br_element : 0.349"  # scripted group (container) (typed FeaturePython)
  n = 0.349103
FEATURE [App::DocumentObjectGroupPython] Ag_element001  label="Ag_element : 0.474"  # scripted group (container) (typed FeaturePython)
  n = 0.474105
FEATURE [App::DocumentObjectGroupPython] I_element005  label="I_element : 0.003"  # scripted group (container) (typed FeaturePython)
  n = 0.00312
FEATURE [App::DocumentObjectGroupPython] G4_PHOTO_EMULSION  # scripted group (container) (typed FeaturePython)
  Dunit = g/cm3
  Dvalue = 3.815
  Group = -> [H_element070,C_element076,N_element035,O_element075,S_element019,Br_element004,Ag_element001,I_element005]
  conduct = 2
  density = 1
  expand = 3
  formula = G4_PHOTO_EMULSION
  name = G4_PHOTO_EMULSION
  specific = 4
FEATURE [App::DocumentObjectGroupPython] C_element077  label="C_element : 9"  # scripted group (container) (typed FeaturePython)
  n = 9
  ref = C_element
FEATURE [App::DocumentObjectGroupPython] H_element071  label="H_element : 033"  # scripted group (container) (typed FeaturePython)
  n = 10
  ref = H_element
FEATURE [App::DocumentObjectGroupPython] G4_PLASTIC_SC_VINYLTOLUENE  # scripted group (container) (typed FeaturePython)
  Dunit = g/cm3
  Dvalue = 1.032
  Group = -> [C_element077,H_element071]
  conduct = 2
  density = 1
  expand = 3
  formula = G4_PLASTIC_SC_VINYLTOLUENE
  name = G4_PLASTIC_SC_VINYLTOLUENE
  specific = 4
FEATURE [App::DocumentObjectGroupPython] Pu_element001  label="Pu_element : 1"  # scripted group (container) (typed FeaturePython)
  n = 1
  ref = Pu_element
FEATURE [App::DocumentObjectGroupPython] O_element076  label="O_element : 037"  # scripted group (container) (typed FeaturePython)
  n = 2
  ref = O_element
FEATURE [App::DocumentObjectGroupPython] G4_PLUTONIUM_DIOXIDE  # scripted group (container) (typed FeaturePython)
  Dunit = g/cm3
  Dvalue = 11.46
  Group = -> [Pu_element001,O_element076]
  conduct = 2
  density = 1
  expand = 3
  formula = G4_PLUTONIUM_DIOXIDE
  name = G4_PLUTONIUM_DIOXIDE
  specific = 4
FEATURE [App::DocumentObjectGroupPython] C_element078  label="C_element : 037"  # scripted group (container) (typed FeaturePython)
  n = 3
  ref = C_element
FEATURE [App::DocumentObjectGroupPython] H_element072  label="H_element : 034"  # scripted group (container) (typed FeaturePython)
  n = 3
  ref = H_element
FEATURE [App::DocumentObjectGroupPython] N_element036  label="N_element : 015"  # scripted group (container) (typed FeaturePython)
  n = 1
  ref = N_element
FEATURE [App::DocumentObjectGroupPython] G4_POLYACRYLONITRILE  # scripted group (container) (typed FeaturePython)
  Dunit = g/cm3
  Dvalue = 1.17
  Group = -> [C_element078,H_element072,N_element036]
  conduct = 2
  density = 1
  expand = 3
  formula = G4_POLYACRYLONITRILE
  name = G4_POLYACRYLONITRILE
  specific = 4
FEATURE [App::DocumentObjectGroupPython] C_element079  label="C_element : 16"  # scripted group (container) (typed FeaturePython)
  n = 16
  ref = C_element
FEATURE [App::DocumentObjectGroupPython] H_element073  label="H_element : 035"  # scripted group (container) (typed FeaturePython)
  n = 14
  ref = H_element
FEATURE [App::DocumentObjectGroupPython] O_element077  label="O_element : 038"  # scripted group (container) (typed FeaturePython)
  n = 3
  ref = O_element
FEATURE [App::DocumentObjectGroupPython] G4_POLYCARBONATE  # scripted group (container) (typed FeaturePython)
  Dunit = g/cm3
  Dvalue = 1.2
  Group = -> [C_element079,H_element073,O_element077]
  conduct = 2
  density = 1
  expand = 3
  formula = G4_POLYCARBONATE
  name = G4_POLYCARBONATE
  specific = 4
FEATURE [App::DocumentObjectGroupPython] C_element080  label="C_element : 038"  # scripted group (container) (typed FeaturePython)
  n = 8
  ref = C_element
FEATURE [App::DocumentObjectGroupPython] H_element074  label="H_element : 036"  # scripted group (container) (typed FeaturePython)
  n = 7
  ref = H_element
FEATURE [App::DocumentObjectGroupPython] Cl_element017  label="Cl_element : 007"  # scripted group (container) (typed FeaturePython)
  n = 1
  ref = Cl_element
FEATURE [App::DocumentObjectGroupPython] G4_POLYCHLOROSTYRENE  # scripted group (container) (typed FeaturePython)
  Dunit = g/cm3
  Dvalue = 1.3
  Group = -> [C_element080,H_element074,Cl_element017]
  conduct = 2
  density = 1
  expand = 3
  formula = G4_POLYCHLOROSTYRENE
  name = G4_POLYCHLOROSTYRENE
  specific = 4
FEATURE [App::DocumentObjectGroupPython] C_element081  label="C_element : 039"  # scripted group (container) (typed FeaturePython)
  n = 1
  ref = C_element
FEATURE [App::DocumentObjectGroupPython] H_element075  label="H_element : 037"  # scripted group (container) (typed FeaturePython)
  n = 2
  ref = H_element
FEATURE [App::DocumentObjectGroupPython] G4_POLYETHYLENE  # scripted group (container) (typed FeaturePython)
  Dunit = g/cm3
  Dvalue = 0.94
  Group = -> [C_element081,H_element075]
  conduct = 2
  density = 1
  expand = 3
  formula = G4_POLYETHYLENE
  name = G4_POLYETHYLENE
  specific = 4
FEATURE [App::DocumentObjectGroupPython] C_element082  label="C_element : 040"  # scripted group (container) (typed FeaturePython)
  n = 10
  ref = C_element
FEATURE [App::DocumentObjectGroupPython] H_element076  label="H_element : 038"  # scripted group (container) (typed FeaturePython)
  n = 8
  ref = H_element
FEATURE [App::DocumentObjectGroupPython] O_element078  label="O_element : 039"  # scripted group (container) (typed FeaturePython)
  n = 4
  ref = O_element
FEATURE [App::DocumentObjectGroupPython] G4_MYLAR  # scripted group (container) (typed FeaturePython)
  Dunit = g/cm3
  Dvalue = 1.4
  Group = -> [C_element082,H_element076,O_element078]
  conduct = 2
  density = 1
  expand = 3
  formula = G4_MYLAR
  name = G4_MYLAR
  specific = 4
FEATURE [App::DocumentObjectGroupPython] C_element083  label="C_element : 041"  # scripted group (container) (typed FeaturePython)
  n = 5
  ref = C_element
FEATURE [App::DocumentObjectGroupPython] H_element077  label="H_element : 039"  # scripted group (container) (typed FeaturePython)
  n = 8
  ref = H_element
FEATURE [App::DocumentObjectGroupPython] O_element079  label="O_element : 040"  # scripted group (container) (typed FeaturePython)
  n = 2
  ref = O_element
FEATURE [App::DocumentObjectGroupPython] G4_PLEXIGLASS  # scripted group (container) (typed FeaturePython)
  Dunit = g/cm3
  Dvalue = 1.19
  Group = -> [C_element083,H_element077,O_element079]
  conduct = 2
  density = 1
  expand = 3
  formula = G4_PLEXIGLASS
  name = G4_PLEXIGLASS
  specific = 4
FEATURE [App::DocumentObjectGroupPython] C_element084  label="C_element : 042"  # scripted group (container) (typed FeaturePython)
  n = 1
  ref = C_element
FEATURE [App::DocumentObjectGroupPython] H_element078  label="H_element : 040"  # scripted group (container) (typed FeaturePython)
  n = 2
  ref = H_element
FEATURE [App::DocumentObjectGroupPython] O_element080  label="O_element : 041"  # scripted group (container) (typed FeaturePython)
  n = 1
  ref = O_element
FEATURE [App::DocumentObjectGroupPython] G4_POLYOXYMETHYLENE  # scripted group (container) (typed FeaturePython)
  Dunit = g/cm3
  Dvalue = 1.425
  Group = -> [C_element084,H_element078,O_element080]
  conduct = 2
  density = 1
  expand = 3
  formula = G4_POLYOXYMETHYLENE
  name = G4_POLYOXYMETHYLENE
  specific = 4
FEATURE [App::DocumentObjectGroupPython] C_element085  label="C_element : 043"  # scripted group (container) (typed FeaturePython)
  n = 2
  ref = C_element
FEATURE [App::DocumentObjectGroupPython] H_element079  label="H_element : 041"  # scripted group (container) (typed FeaturePython)
  n = 4
  ref = H_element
FEATURE [App::DocumentObjectGroupPython] G4_POLYPROPYLENE  # scripted group (container) (typed FeaturePython)
  Dunit = g/cm3
  Dvalue = 0.9
  Group = -> [C_element085,H_element079]
  conduct = 2
  density = 1
  expand = 3
  formula = G4_POLYPROPYLENE
  name = G4_POLYPROPYLENE
  specific = 4
FEATURE [App::DocumentObjectGroupPython] C_element086  label="C_element : 044"  # scripted group (container) (typed FeaturePython)
  n = 8
  ref = C_element
FEATURE [App::DocumentObjectGroupPython] H_element080  label="H_element : 042"  # scripted group (container) (typed FeaturePython)
  n = 8
  ref = H_element
FEATURE [App::DocumentObjectGroupPython] G4_POLYSTYRENE  # scripted group (container) (typed FeaturePython)
  Dunit = g/cm3
  Dvalue = 1.06
  Group = -> [C_element086,H_element080]
  conduct = 2
  density = 1
  expand = 3
  formula = G4_POLYSTYRENE
  name = G4_POLYSTYRENE
  specific = 4
FEATURE [App::DocumentObjectGroupPython] C_element087  label="C_element : 045"  # scripted group (container) (typed FeaturePython)
  n = 2
  ref = C_element
FEATURE [App::DocumentObjectGroupPython] F_element014  label="F_element : 4"  # scripted group (container) (typed FeaturePython)
  n = 4
  ref = F_element
FEATURE [App::DocumentObjectGroupPython] G4_TEFLON  # scripted group (container) (typed FeaturePython)
  Dunit = g/cm3
  Dvalue = 2.2
  Group = -> [C_element087,F_element014]
  conduct = 2
  density = 1
  expand = 3
  formula = G4_TEFLON
  name = G4_TEFLON
  specific = 4
FEATURE [App::DocumentObjectGroupPython] C_element088  label="C_element : 046"  # scripted group (container) (typed FeaturePython)
  n = 2
  ref = C_element
FEATURE [App::DocumentObjectGroupPython] F_element015  label="F_element : 006"  # scripted group (container) (typed FeaturePython)
  n = 3
  ref = F_element
FEATURE [App::DocumentObjectGroupPython] Cl_element018  label="Cl_element : 008"  # scripted group (container) (typed FeaturePython)
  n = 1
  ref = Cl_element
FEATURE [App::DocumentObjectGroupPython] G4_POLYTRIFLUOROCHLOROETHYLENE  # scripted group (container) (typed FeaturePython)
  Dunit = g/cm3
  Dvalue = 2.1
  Group = -> [C_element088,F_element015,Cl_element018]
  conduct = 2
  density = 1
  expand = 3
  formula = G4_POLYTRIFLUOROCHLOROETHYLENE
  name = G4_POLYTRIFLUOROCHLOROETHYLENE
  specific = 4
FEATURE [App::DocumentObjectGroupPython] C_element089  label="C_element : 047"  # scripted group (container) (typed FeaturePython)
  n = 4
  ref = C_element
FEATURE [App::DocumentObjectGroupPython] H_element081  label="H_element : 043"  # scripted group (container) (typed FeaturePython)
  n = 6
  ref = H_element
FEATURE [App::DocumentObjectGroupPython] O_element081  label="O_element : 042"  # scripted group (container) (typed FeaturePython)
  n = 2
  ref = O_element
FEATURE [App::DocumentObjectGroupPython] G4_POLYVINYL_ACETATE  # scripted group (container) (typed FeaturePython)
  Dunit = g/cm3
  Dvalue = 1.19
  Group = -> [C_element089,H_element081,O_element081]
  conduct = 2
  density = 1
  expand = 3
  formula = G4_POLYVINYL_ACETATE
  name = G4_POLYVINYL_ACETATE
  specific = 4
FEATURE [App::DocumentObjectGroupPython] C_element090  label="C_element : 048"  # scripted group (container) (typed FeaturePython)
  n = 2
  ref = C_element
FEATURE [App::DocumentObjectGroupPython] H_element082  label="H_element : 044"  # scripted group (container) (typed FeaturePython)
  n = 4
  ref = H_element
FEATURE [App::DocumentObjectGroupPython] O_element082  label="O_element : 043"  # scripted group (container) (typed FeaturePython)
  n = 1
  ref = O_element
FEATURE [App::DocumentObjectGroupPython] G4_POLYVINYL_ALCOHOL  # scripted group (container) (typed FeaturePython)
  Dunit = g/cm3
  Dvalue = 1.3
  Group = -> [C_element090,H_element082,O_element082]
  conduct = 2
  density = 1
  expand = 3
  formula = G4_POLYVINYL_ALCOHOL
  name = G4_POLYVINYL_ALCOHOL
  specific = 4
FEATURE [App::DocumentObjectGroupPython] C_element091  label="C_element : 049"  # scripted group (container) (typed FeaturePython)
  n = 8
  ref = C_element
FEATURE [App::DocumentObjectGroupPython] H_element083  label="H_element : 045"  # scripted group (container) (typed FeaturePython)
  n = 14
  ref = H_element
FEATURE [App::DocumentObjectGroupPython] O_element083  label="O_element : 044"  # scripted group (container) (typed FeaturePython)
  n = 2
  ref = O_element
FEATURE [App::DocumentObjectGroupPython] G4_POLYVINYL_BUTYRAL  # scripted group (container) (typed FeaturePython)
  Dunit = g/cm3
  Dvalue = 1.12
  Group = -> [C_element091,H_element083,O_element083]
  conduct = 2
  density = 1
  expand = 3
  formula = G4_POLYVINYL_BUTYRAL
  name = G4_POLYVINYL_BUTYRAL
  specific = 4
FEATURE [App::DocumentObjectGroupPython] C_element092  label="C_element : 050"  # scripted group (container) (typed FeaturePython)
  n = 2
  ref = C_element
FEATURE [App::DocumentObjectGroupPython] H_element084  label="H_element : 046"  # scripted group (container) (typed FeaturePython)
  n = 3
  ref = H_element
FEATURE [App::DocumentObjectGroupPython] Cl_element019  label="Cl_element : 009"  # scripted group (container) (typed FeaturePython)
  n = 1
  ref = Cl_element
FEATURE [App::DocumentObjectGroupPython] G4_POLYVINYL_CHLORIDE  # scripted group (container) (typed FeaturePython)
  Dunit = g/cm3
  Dvalue = 1.3
  Group = -> [C_element092,H_element084,Cl_element019]
  conduct = 2
  density = 1
  expand = 3
  formula = G4_POLYVINYL_CHLORIDE
  name = G4_POLYVINYL_CHLORIDE
  specific = 4
FEATURE [App::DocumentObjectGroupPython] C_element093  label="C_element : 051"  # scripted group (container) (typed FeaturePython)
  n = 2
  ref = C_element
FEATURE [App::DocumentObjectGroupPython] H_element085  label="H_element : 047"  # scripted group (container) (typed FeaturePython)
  n = 2
  ref = H_element
FEATURE [App::DocumentObjectGroupPython] Cl_element020  label="Cl_element : 010"  # scripted group (container) (typed FeaturePython)
  n = 2
  ref = Cl_element
FEATURE [App::DocumentObjectGroupPython] G4_POLYVINYLIDENE_CHLORIDE  # scripted group (container) (typed FeaturePython)
  Dunit = g/cm3
  Dvalue = 1.7
  Group = -> [C_element093,H_element085,Cl_element020]
  conduct = 2
  density = 1
  expand = 3
  formula = G4_POLYVINYLIDENE_CHLORIDE
  name = G4_POLYVINYLIDENE_CHLORIDE
  specific = 4
FEATURE [App::DocumentObjectGroupPython] C_element094  label="C_element : 052"  # scripted group (container) (typed FeaturePython)
  n = 2
  ref = C_element
FEATURE [App::DocumentObjectGroupPython] H_element086  label="H_element : 048"  # scripted group (container) (typed FeaturePython)
  n = 2
  ref = H_element
FEATURE [App::DocumentObjectGroupPython] F_element016  label="F_element : 007"  # scripted group (container) (typed FeaturePython)
  n = 2
  ref = F_element
FEATURE [App::DocumentObjectGroupPython] G4_POLYVINYLIDENE_FLUORIDE  # scripted group (container) (typed FeaturePython)
  Dunit = g/cm3
  Dvalue = 1.76
  Group = -> [C_element094,H_element086,F_element016]
  conduct = 2
  density = 1
  expand = 3
  formula = G4_POLYVINYLIDENE_FLUORIDE
  name = G4_POLYVINYLIDENE_FLUORIDE
  specific = 4
FEATURE [App::DocumentObjectGroupPython] C_element095  label="C_element : 053"  # scripted group (container) (typed FeaturePython)
  n = 6
  ref = C_element
FEATURE [App::DocumentObjectGroupPython] H_element087  label="H_element : 9"  # scripted group (container) (typed FeaturePython)
  n = 9
  ref = H_element
FEATURE [App::DocumentObjectGroupPython] N_element037  label="N_element : 016"  # scripted group (container) (typed FeaturePython)
  n = 1
  ref = N_element
FEATURE [App::DocumentObjectGroupPython] O_element084  label="O_element : 045"  # scripted group (container) (typed FeaturePython)
  n = 1
  ref = O_element
FEATURE [App::DocumentObjectGroupPython] G4_POLYVINYL_PYRROLIDONE  # scripted group (container) (typed FeaturePython)
  Dunit = g/cm3
  Dvalue = 1.25
  Group = -> [C_element095,H_element087,N_element037,O_element084]
  conduct = 2
  density = 1
  expand = 3
  formula = G4_POLYVINYL_PYRROLIDONE
  name = G4_POLYVINYL_PYRROLIDONE
  specific = 4
FEATURE [App::DocumentObjectGroupPython] K_element008  label="K_element : 1"  # scripted group (container) (typed FeaturePython)
  n = 1
  ref = K_element
FEATURE [App::DocumentObjectGroupPython] I_element006  label="I_element : 003"  # scripted group (container) (typed FeaturePython)
  n = 1
  ref = I_element
FEATURE [App::DocumentObjectGroupPython] G4_POTASSIUM_IODIDE  # scripted group (container) (typed FeaturePython)
  Dunit = g/cm3
  Dvalue = 3.13
  Group = -> [K_element008,I_element006]
  conduct = 2
  density = 1
  expand = 3
  formula = G4_POTASSIUM_IODIDE
  name = G4_POTASSIUM_IODIDE
  specific = 4
FEATURE [App::DocumentObjectGroupPython] K_element009  label="K_element : 2"  # scripted group (container) (typed FeaturePython)
  n = 2
  ref = K_element
FEATURE [App::DocumentObjectGroupPython] O_element085  label="O_element : 046"  # scripted group (container) (typed FeaturePython)
  n = 1
  ref = O_element
FEATURE [App::DocumentObjectGroupPython] G4_POTASSIUM_OXIDE  # scripted group (container) (typed FeaturePython)
  Dunit = g/cm3
  Dvalue = 2.32
  Group = -> [K_element009,O_element085]
  conduct = 2
  density = 1
  expand = 3
  formula = G4_POTASSIUM_OXIDE
  name = G4_POTASSIUM_OXIDE
  specific = 4
FEATURE [App::DocumentObjectGroupPython] C_element096  label="C_element : 054"  # scripted group (container) (typed FeaturePython)
  n = 3
  ref = C_element
FEATURE [App::DocumentObjectGroupPython] H_element088  label="H_element : 049"  # scripted group (container) (typed FeaturePython)
  n = 8
  ref = H_element
FEATURE [App::DocumentObjectGroupPython] G4_PROPANE  # scripted group (container) (typed FeaturePython)
  Dunit = g/cm3
  Dvalue = 0.00187939
  Group = -> [C_element096,H_element088]
  conduct = 2
  density = 1
  expand = 3
  formula = G4_PROPANE
  name = G4_PROPANE
  specific = 4
FEATURE [App::DocumentObjectGroupPython] C_element097  label="C_element : 055"  # scripted group (container) (typed FeaturePython)
  n = 3
  ref = C_element
FEATURE [App::DocumentObjectGroupPython] H_element089  label="H_element : 050"  # scripted group (container) (typed FeaturePython)
  n = 8
  ref = H_element
FEATURE [App::DocumentObjectGroupPython] G4_lPROPANE  # scripted group (container) (typed FeaturePython)
  Dunit = g/cm3
  Dvalue = 0.43
  Group = -> [C_element097,H_element089]
  conduct = 2
  density = 1
  expand = 3
  formula = G4_lPROPANE
  name = G4_lPROPANE
  specific = 4
FEATURE [App::DocumentObjectGroupPython] C_element098  label="C_element : 056"  # scripted group (container) (typed FeaturePython)
  n = 3
  ref = C_element
FEATURE [App::DocumentObjectGroupPython] H_element090  label="H_element : 051"  # scripted group (container) (typed FeaturePython)
  n = 8
  ref = H_element
FEATURE [App::DocumentObjectGroupPython] O_element086  label="O_element : 047"  # scripted group (container) (typed FeaturePython)
  n = 1
  ref = O_element
FEATURE [App::DocumentObjectGroupPython] G4_N_PROPYL_ALCOHOL  label="G4_N-PROPYL_ALCOHOL"  # scripted group (container) (typed FeaturePython)
  Dunit = g/cm3
  Dvalue = 0.8035
  Group = -> [C_element098,H_element090,O_element086]
  conduct = 2
  density = 1
  expand = 3
  formula = G4_N-PROPYL_ALCOHOL
  name = G4_N-PROPYL_ALCOHOL
  specific = 4
FEATURE [App::DocumentObjectGroupPython] C_element099  label="C_element : 057"  # scripted group (container) (typed FeaturePython)
  n = 5
  ref = C_element
FEATURE [App::DocumentObjectGroupPython] H_element091  label="H_element : 052"  # scripted group (container) (typed FeaturePython)
  n = 5
  ref = H_element
FEATURE [App::DocumentObjectGroupPython] N_element038  label="N_element : 017"  # scripted group (container) (typed FeaturePython)
  n = 1
  ref = N_element
FEATURE [App::DocumentObjectGroupPython] G4_PYRIDINE  # scripted group (container) (typed FeaturePython)
  Dunit = g/cm3
  Dvalue = 0.9819
  Group = -> [C_element099,H_element091,N_element038]
  conduct = 2
  density = 1
  expand = 3
  formula = G4_PYRIDINE
  name = G4_PYRIDINE
  specific = 4
FEATURE [App::DocumentObjectGroupPython] H_element092  label="H_element : 0.144"  # scripted group (container) (typed FeaturePython)
  n = 0.143711
FEATURE [App::DocumentObjectGroupPython] C_element100  label="C_element : 0.856"  # scripted group (container) (typed FeaturePython)
  n = 0.856289
FEATURE [App::DocumentObjectGroupPython] G4_RUBBER_BUTYL  # scripted group (container) (typed FeaturePython)
  Dunit = g/cm3
  Dvalue = 0.92
  Group = -> [H_element092,C_element100]
  conduct = 2
  density = 1
  expand = 3
  formula = G4_RUBBER_BUTYL
  name = G4_RUBBER_BUTYL
  specific = 4
FEATURE [App::DocumentObjectGroupPython] H_element093  label="H_element : 0.118"  # scripted group (container) (typed FeaturePython)
  n = 0.118371
FEATURE [App::DocumentObjectGroupPython] C_element101  label="C_element : 0.882"  # scripted group (container) (typed FeaturePython)
  n = 0.881629
FEATURE [App::DocumentObjectGroupPython] G4_RUBBER_NATURAL  # scripted group (container) (typed FeaturePython)
  Dunit = g/cm3
  Dvalue = 0.92
  Group = -> [H_element093,C_element101]
  conduct = 2
  density = 1
  expand = 3
  formula = G4_RUBBER_NATURAL
  name = G4_RUBBER_NATURAL
  specific = 4
FEATURE [App::DocumentObjectGroupPython] H_element094  label="H_element : 0.145"  # scripted group (container) (typed FeaturePython)
  n = 0.05692
FEATURE [App::DocumentObjectGroupPython] C_element102  label="C_element : 0.543"  # scripted group (container) (typed FeaturePython)
  n = 0.542646
FEATURE [App::DocumentObjectGroupPython] Cl_element021  label="Cl_element : 0.400"  # scripted group (container) (typed FeaturePython)
  n = 0.400434
FEATURE [App::DocumentObjectGroupPython] G4_RUBBER_NEOPRENE  # scripted group (container) (typed FeaturePython)
  Dunit = g/cm3
  Dvalue = 1.23
  Group = -> [H_element094,C_element102,Cl_element021]
  conduct = 2
  density = 1
  expand = 3
  formula = G4_RUBBER_NEOPRENE
  name = G4_RUBBER_NEOPRENE
  specific = 4
FEATURE [App::DocumentObjectGroupPython] Si_element006  label="Si_element : 1"  # scripted group (container) (typed FeaturePython)
  n = 1
  ref = Si_element
FEATURE [App::DocumentObjectGroupPython] O_element087  label="O_element : 048"  # scripted group (container) (typed FeaturePython)
  n = 2
  ref = O_element
FEATURE [App::DocumentObjectGroupPython] G4_SILICON_DIOXIDE  # scripted group (container) (typed FeaturePython)
  Dunit = g/cm3
  Dvalue = 2.32
  Group = -> [Si_element006,O_element087]
  conduct = 2
  density = 1
  expand = 3
  formula = G4_SILICON_DIOXIDE
  name = G4_SILICON_DIOXIDE
  specific = 4
FEATURE [App::DocumentObjectGroupPython] Ag_element002  label="Ag_element : 1"  # scripted group (container) (typed FeaturePython)
  n = 1
  ref = Ag_element
FEATURE [App::DocumentObjectGroupPython] Br_element005  label="Br_element : 003"  # scripted group (container) (typed FeaturePython)
  n = 1
  ref = Br_element
FEATURE [App::DocumentObjectGroupPython] G4_SILVER_BROMIDE  # scripted group (container) (typed FeaturePython)
  Dunit = g/cm3
  Dvalue = 6.473
  Group = -> [Ag_element002,Br_element005]
  conduct = 2
  density = 1
  expand = 3
  formula = G4_SILVER_BROMIDE
  name = G4_SILVER_BROMIDE
  specific = 4
FEATURE [App::DocumentObjectGroupPython] Ag_element003  label="Ag_element : 002"  # scripted group (container) (typed FeaturePython)
  n = 1
  ref = Ag_element
FEATURE [App::DocumentObjectGroupPython] Cl_element022  label="Cl_element : 011"  # scripted group (container) (typed FeaturePython)
  n = 1
  ref = Cl_element
FEATURE [App::DocumentObjectGroupPython] G4_SILVER_CHLORIDE  # scripted group (container) (typed FeaturePython)
  Dunit = g/cm3
  Dvalue = 5.56
  Group = -> [Ag_element003,Cl_element022]
  conduct = 2
  density = 1
  expand = 3
  formula = G4_SILVER_CHLORIDE
  name = G4_SILVER_CHLORIDE
  specific = 4
FEATURE [App::DocumentObjectGroupPython] Br_element006  label="Br_element : 0.423"  # scripted group (container) (typed FeaturePython)
  n = 0.422895
FEATURE [App::DocumentObjectGroupPython] Ag_element004  label="Ag_element : 0.574"  # scripted group (container) (typed FeaturePython)
  n = 0.573748
FEATURE [App::DocumentObjectGroupPython] I_element007  label="I_element : 0.649"  # scripted group (container) (typed FeaturePython)
  n = 0.003357
FEATURE [App::DocumentObjectGroupPython] G4_SILVER_HALIDES  # scripted group (container) (typed FeaturePython)
  Dunit = g/cm3
  Dvalue = 6.47
  Group = -> [Br_element006,Ag_element004,I_element007]
  conduct = 2
  density = 1
  expand = 3
  formula = G4_SILVER_HALIDES
  name = G4_SILVER_HALIDES
  specific = 4
FEATURE [App::DocumentObjectGroupPython] Ag_element005  label="Ag_element : 003"  # scripted group (container) (typed FeaturePython)
  n = 1
  ref = Ag_element
FEATURE [App::DocumentObjectGroupPython] I_element008  label="I_element : 004"  # scripted group (container) (typed FeaturePython)
  n = 1
  ref = I_element
FEATURE [App::DocumentObjectGroupPython] G4_SILVER_IODIDE  # scripted group (container) (typed FeaturePython)
  Dunit = g/cm3
  Dvalue = 6.01
  Group = -> [Ag_element005,I_element008]
  conduct = 2
  density = 1
  expand = 3
  formula = G4_SILVER_IODIDE
  name = G4_SILVER_IODIDE
  specific = 4
FEATURE [App::DocumentObjectGroupPython] H_element095  label="H_element : 0.100"  # scripted group (container) (typed FeaturePython)
  n = 0.1
FEATURE [App::DocumentObjectGroupPython] C_element103  label="C_element : 0.204"  # scripted group (container) (typed FeaturePython)
  n = 0.204
FEATURE [App::DocumentObjectGroupPython] N_element039  label="N_element : 0.759"  # scripted group (container) (typed FeaturePython)
  n = 0.042
FEATURE [App::DocumentObjectGroupPython] O_element088  label="O_element : 0.645"  # scripted group (container) (typed FeaturePython)
  n = 0.645
FEATURE [App::DocumentObjectGroupPython] Na_element013  label="Na_element : 0.100"  # scripted group (container) (typed FeaturePython)
  n = 0.002
FEATURE [App::DocumentObjectGroupPython] P_element009  label="P_element : 0.107"  # scripted group (container) (typed FeaturePython)
  n = 0.001
FEATURE [App::DocumentObjectGroupPython] S_element020  label="S_element : 0.021"  # scripted group (container) (typed FeaturePython)
  n = 0.002
FEATURE [App::DocumentObjectGroupPython] Cl_element023  label="Cl_element : 0.590"  # scripted group (container) (typed FeaturePython)
  n = 0.003
FEATURE [App::DocumentObjectGroupPython] K_element010  label="K_element : 0.001"  # scripted group (container) (typed FeaturePython)
  n = 0.001
FEATURE [App::DocumentObjectGroupPython] G4_SKIN_ICRP  # scripted group (container) (typed FeaturePython)
  Dunit = g/cm3
  Dvalue = 1.09
  Group = -> [H_element095,C_element103,N_element039,O_element088,Na_element013,P_element009,S_element020,Cl_element023,K_element010]
  conduct = 2
  density = 1
  expand = 3
  formula = G4_SKIN_ICRP
  name = G4_SKIN_ICRP
  specific = 4
FEATURE [App::DocumentObjectGroupPython] Na_element014  label="Na_element : 2"  # scripted group (container) (typed FeaturePython)
  n = 2
  ref = Na_element
FEATURE [App::DocumentObjectGroupPython] C_element104  label="C_element : 058"  # scripted group (container) (typed FeaturePython)
  n = 1
  ref = C_element
FEATURE [App::DocumentObjectGroupPython] O_element089  label="O_element : 049"  # scripted group (container) (typed FeaturePython)
  n = 3
  ref = O_element
FEATURE [App::DocumentObjectGroupPython] G4_SODIUM_CARBONATE  # scripted group (container) (typed FeaturePython)
  Dunit = g/cm3
  Dvalue = 2.532
  Group = -> [Na_element014,C_element104,O_element089]
  conduct = 2
  density = 1
  expand = 3
  formula = G4_SODIUM_CARBONATE
  name = G4_SODIUM_CARBONATE
  specific = 4
FEATURE [App::DocumentObjectGroupPython] Na_element015  label="Na_element : 1"  # scripted group (container) (typed FeaturePython)
  n = 1
  ref = Na_element
FEATURE [App::DocumentObjectGroupPython] I_element009  label="I_element : 005"  # scripted group (container) (typed FeaturePython)
  n = 1
  ref = I_element
FEATURE [App::DocumentObjectGroupPython] G4_SODIUM_IODIDE  # scripted group (container) (typed FeaturePython)
  Dunit = g/cm3
  Dvalue = 3.667
  Group = -> [Na_element015,I_element009]
  conduct = 2
  density = 1
  expand = 3
  formula = G4_SODIUM_IODIDE
  name = G4_SODIUM_IODIDE
  specific = 4
FEATURE [App::DocumentObjectGroupPython] Na_element016  label="Na_element : 003"  # scripted group (container) (typed FeaturePython)
  n = 2
  ref = Na_element
FEATURE [App::DocumentObjectGroupPython] O_element090  label="O_element : 050"  # scripted group (container) (typed FeaturePython)
  n = 1
  ref = O_element
FEATURE [App::DocumentObjectGroupPython] G4_SODIUM_MONOXIDE  # scripted group (container) (typed FeaturePython)
  Dunit = g/cm3
  Dvalue = 2.27
  Group = -> [Na_element016,O_element090]
  conduct = 2
  density = 1
  expand = 3
  formula = G4_SODIUM_MONOXIDE
  name = G4_SODIUM_MONOXIDE
  specific = 4
FEATURE [App::DocumentObjectGroupPython] Na_element017  label="Na_element : 004"  # scripted group (container) (typed FeaturePython)
  n = 1
  ref = Na_element
FEATURE [App::DocumentObjectGroupPython] N_element040  label="N_element : 018"  # scripted group (container) (typed FeaturePython)
  n = 1
  ref = N_element
FEATURE [App::DocumentObjectGroupPython] O_element091  label="O_element : 051"  # scripted group (container) (typed FeaturePython)
  n = 3
  ref = O_element
FEATURE [App::DocumentObjectGroupPython] G4_SODIUM_NITRATE  # scripted group (container) (typed FeaturePython)
  Dunit = g/cm3
  Dvalue = 2.261
  Group = -> [Na_element017,N_element040,O_element091]
  conduct = 2
  density = 1
  expand = 3
  formula = G4_SODIUM_NITRATE
  name = G4_SODIUM_NITRATE
  specific = 4
FEATURE [App::DocumentObjectGroupPython] C_element105  label="C_element : 059"  # scripted group (container) (typed FeaturePython)
  n = 14
  ref = C_element
FEATURE [App::DocumentObjectGroupPython] H_element096  label="H_element : 053"  # scripted group (container) (typed FeaturePython)
  n = 12
  ref = H_element
FEATURE [App::DocumentObjectGroupPython] G4_STILBENE  # scripted group (container) (typed FeaturePython)
  Dunit = g/cm3
  Dvalue = 0.9707
  Group = -> [C_element105,H_element096]
  conduct = 2
  density = 1
  expand = 3
  formula = G4_STILBENE
  name = G4_STILBENE
  specific = 4
FEATURE [App::DocumentObjectGroupPython] C_element106  label="C_element : 12"  # scripted group (container) (typed FeaturePython)
  n = 12
  ref = C_element
FEATURE [App::DocumentObjectGroupPython] H_element097  label="H_element : 22"  # scripted group (container) (typed FeaturePython)
  n = 22
  ref = H_element
FEATURE [App::DocumentObjectGroupPython] O_element092  label="O_element : 11"  # scripted group (container) (typed FeaturePython)
  n = 11
  ref = O_element
FEATURE [App::DocumentObjectGroupPython] G4_SUCROSE  # scripted group (container) (typed FeaturePython)
  Dunit = g/cm3
  Dvalue = 1.5805
  Group = -> [C_element106,H_element097,O_element092]
  conduct = 2
  density = 1
  expand = 3
  formula = G4_SUCROSE
  name = G4_SUCROSE
  specific = 4
FEATURE [App::DocumentObjectGroupPython] C_element107  label="C_element : 18"  # scripted group (container) (typed FeaturePython)
  n = 18
  ref = C_element
FEATURE [App::DocumentObjectGroupPython] H_element098  label="H_element : 054"  # scripted group (container) (typed FeaturePython)
  n = 14
  ref = H_element
FEATURE [App::DocumentObjectGroupPython] G4_TERPHENYL  # scripted group (container) (typed FeaturePython)
  Dunit = g/cm3
  Dvalue = 1.24
  Group = -> [C_element107,H_element098]
  conduct = 2
  density = 1
  expand = 3
  formula = G4_TERPHENYL
  name = G4_TERPHENYL
  specific = 4
FEATURE [App::DocumentObjectGroupPython] H_element099  label="H_element : 0.146"  # scripted group (container) (typed FeaturePython)
  n = 0.106
FEATURE [App::DocumentObjectGroupPython] C_element108  label="C_element : 0.883"  # scripted group (container) (typed FeaturePython)
  n = 0.099
FEATURE [App::DocumentObjectGroupPython] N_element041  label="N_element : 0.020"  # scripted group (container) (typed FeaturePython)
  n = 0.02
FEATURE [App::DocumentObjectGroupPython] O_element093  label="O_element : 0.766"  # scripted group (container) (typed FeaturePython)
  n = 0.766
FEATURE [App::DocumentObjectGroupPython] Na_element018  label="Na_element : 0.101"  # scripted group (container) (typed FeaturePython)
  n = 0.002
FEATURE [App::DocumentObjectGroupPython] P_element010  label="P_element : 0.108"  # scripted group (container) (typed FeaturePython)
  n = 0.001
FEATURE [App::DocumentObjectGroupPython] S_element021  label="S_element : 0.022"  # scripted group (container) (typed FeaturePython)
  n = 0.002
FEATURE [App::DocumentObjectGroupPython] Cl_element024  label="Cl_element : 0.002"  # scripted group (container) (typed FeaturePython)
  n = 0.002
FEATURE [App::DocumentObjectGroupPython] K_element011  label="K_element : 0.017"  # scripted group (container) (typed FeaturePython)
  n = 0.002
FEATURE [App::DocumentObjectGroupPython] G4_TESTIS_ICRP  # scripted group (container) (typed FeaturePython)
  Dunit = g/cm3
  Dvalue = 1.04
  Group = -> [H_element099,C_element108,N_element041,O_element093,Na_element018,P_element010,S_element021,Cl_element024,K_element011]
  conduct = 2
  density = 1
  expand = 3
  formula = G4_TESTIS_ICRP
  name = G4_TESTIS_ICRP
  specific = 4
FEATURE [App::DocumentObjectGroupPython] C_element109  label="C_element : 060"  # scripted group (container) (typed FeaturePython)
  n = 2
  ref = C_element
FEATURE [App::DocumentObjectGroupPython] Cl_element025  label="Cl_element : 012"  # scripted group (container) (typed FeaturePython)
  n = 4
  ref = Cl_element
FEATURE [App::DocumentObjectGroupPython] G4_TETRACHLOROETHYLENE  # scripted group (container) (typed FeaturePython)
  Dunit = g/cm3
  Dvalue = 1.625
  Group = -> [C_element109,Cl_element025]
  conduct = 2
  density = 1
  expand = 3
  formula = G4_TETRACHLOROETHYLENE
  name = G4_TETRACHLOROETHYLENE
  specific = 4
FEATURE [App::DocumentObjectGroupPython] Tl_element001  label="Tl_element : 1"  # scripted group (container) (typed FeaturePython)
  n = 1
  ref = Tl_element
FEATURE [App::DocumentObjectGroupPython] Cl_element026  label="Cl_element : 013"  # scripted group (container) (typed FeaturePython)
  n = 1
  ref = Cl_element
FEATURE [App::DocumentObjectGroupPython] G4_THALLIUM_CHLORIDE  # scripted group (container) (typed FeaturePython)
  Dunit = g/cm3
  Dvalue = 7.004
  Group = -> [Tl_element001,Cl_element026]
  conduct = 2
  density = 1
  expand = 3
  formula = G4_THALLIUM_CHLORIDE
  name = G4_THALLIUM_CHLORIDE
  specific = 4
FEATURE [App::DocumentObjectGroupPython] H_element100  label="H_element : 0.147"  # scripted group (container) (typed FeaturePython)
  n = 0.105
FEATURE [App::DocumentObjectGroupPython] C_element110  label="C_element : 0.256"  # scripted group (container) (typed FeaturePython)
  n = 0.256
FEATURE [App::DocumentObjectGroupPython] N_element042  label="N_element : 0.760"  # scripted group (container) (typed FeaturePython)
  n = 0.027
FEATURE [App::DocumentObjectGroupPython] O_element094  label="O_element : 0.602"  # scripted group (container) (typed FeaturePython)
  n = 0.602
FEATURE [App::DocumentObjectGroupPython] Na_element019  label="Na_element : 0.102"  # scripted group (container) (typed FeaturePython)
  n = 0.001
FEATURE [App::DocumentObjectGroupPython] P_element011  label="P_element : 0.109"  # scripted group (container) (typed FeaturePython)
  n = 0.002
FEATURE [App::DocumentObjectGroupPython] S_element022  label="S_element : 0.023"  # scripted group (container) (typed FeaturePython)
  n = 0.003
FEATURE [App::DocumentObjectGroupPython] Cl_element027  label="Cl_element : 0.591"  # scripted group (container) (typed FeaturePython)
  n = 0.002
FEATURE [App::DocumentObjectGroupPython] K_element012  label="K_element : 0.018"  # scripted group (container) (typed FeaturePython)
  n = 0.002
FEATURE [App::DocumentObjectGroupPython] G4_TISSUE_SOFT_ICRP  # scripted group (container) (typed FeaturePython)
  Dunit = g/cm3
  Dvalue = 1.03
  Group = -> [H_element100,C_element110,N_element042,O_element094,Na_element019,P_element011,S_element022,Cl_element027,K_element012]
  conduct = 2
  density = 1
  expand = 3
  formula = G4_TISSUE_SOFT_ICRP
  name = G4_TISSUE_SOFT_ICRP
  specific = 4
FEATURE [App::DocumentObjectGroupPython] H_element101  label="H_element : 0.148"  # scripted group (container) (typed FeaturePython)
  n = 0.101
FEATURE [App::DocumentObjectGroupPython] C_element111  label="C_element : 0.111"  # scripted group (container) (typed FeaturePython)
  n = 0.111
FEATURE [App::DocumentObjectGroupPython] N_element043  label="N_element : 0.026"  # scripted group (container) (typed FeaturePython)
  n = 0.026
FEATURE [App::DocumentObjectGroupPython] O_element095  label="O_element : 0.762"  # scripted group (container) (typed FeaturePython)
  n = 0.762
FEATURE [App::DocumentObjectGroupPython] G4_TISSUE_SOFT_ICRU_4  label="G4_TISSUE_SOFT_ICRU-4"  # scripted group (container) (typed FeaturePython)
  Dunit = g/cm3
  Dvalue = 1
  Group = -> [H_element101,C_element111,N_element043,O_element095]
  conduct = 2
  density = 1
  expand = 3
  formula = G4_TISSUE_SOFT_ICRU-4
  name = G4_TISSUE_SOFT_ICRU-4
  specific = 4
FEATURE [App::DocumentObjectGroupPython] H_element102  label="H_element : 0.149"  # scripted group (container) (typed FeaturePython)
  n = 0.101869
FEATURE [App::DocumentObjectGroupPython] C_element112  label="C_element : 0.456"  # scripted group (container) (typed FeaturePython)
  n = 0.456179
FEATURE [App::DocumentObjectGroupPython] N_element044  label="N_element : 0.761"  # scripted group (container) (typed FeaturePython)
  n = 0.035172
FEATURE [App::DocumentObjectGroupPython] O_element096  label="O_element : 0.407"  # scripted group (container) (typed FeaturePython)
  n = 0.40678
FEATURE [App::DocumentObjectGroupPython] G4_TISSUE_METHANE  label="G4_TISSUE-METHANE"  # scripted group (container) (typed FeaturePython)
  Dunit = g/cm3
  Dvalue = 0.00106409
  Group = -> [H_element102,C_element112,N_element044,O_element096]
  conduct = 2
  density = 1
  expand = 3
  formula = G4_TISSUE-METHANE
  name = G4_TISSUE-METHANE
  specific = 4
FEATURE [App::DocumentObjectGroupPython] H_element103  label="H_element : 0.103"  # scripted group (container) (typed FeaturePython)
  n = 0.102672
FEATURE [App::DocumentObjectGroupPython] C_element113  label="C_element : 0.569"  # scripted group (container) (typed FeaturePython)
  n = 0.56894
FEATURE [App::DocumentObjectGroupPython] N_element045  label="N_element : 0.762"  # scripted group (container) (typed FeaturePython)
  n = 0.035022
FEATURE [App::DocumentObjectGroupPython] O_element097  label="O_element : 0.293"  # scripted group (container) (typed FeaturePython)
  n = 0.293366
FEATURE [App::DocumentObjectGroupPython] G4_TISSUE_PROPANE  label="G4_TISSUE-PROPANE"  # scripted group (container) (typed FeaturePython)
  Dunit = g/cm3
  Dvalue = 0.00182628
  Group = -> [H_element103,C_element113,N_element045,O_element097]
  conduct = 2
  density = 1
  expand = 3
  formula = G4_TISSUE-PROPANE
  name = G4_TISSUE-PROPANE
  specific = 4
FEATURE [App::DocumentObjectGroupPython] Ti_element003  label="Ti_element : 1"  # scripted group (container) (typed FeaturePython)
  n = 1
  ref = Ti_element
FEATURE [App::DocumentObjectGroupPython] O_element098  label="O_element : 052"  # scripted group (container) (typed FeaturePython)
  n = 2
  ref = O_element
FEATURE [App::DocumentObjectGroupPython] G4_TITANIUM_DIOXIDE  # scripted group (container) (typed FeaturePython)
  Dunit = g/cm3
  Dvalue = 4.26
  Group = -> [Ti_element003,O_element098]
  conduct = 2
  density = 1
  expand = 3
  formula = G4_TITANIUM_DIOXIDE
  name = G4_TITANIUM_DIOXIDE
  specific = 4
FEATURE [App::DocumentObjectGroupPython] C_element114  label="C_element : 061"  # scripted group (container) (typed FeaturePython)
  n = 7
  ref = C_element
FEATURE [App::DocumentObjectGroupPython] H_element104  label="H_element : 055"  # scripted group (container) (typed FeaturePython)
  n = 8
  ref = H_element
FEATURE [App::DocumentObjectGroupPython] G4_TOLUENE  # scripted group (container) (typed FeaturePython)
  Dunit = g/cm3
  Dvalue = 0.8669
  Group = -> [C_element114,H_element104]
  conduct = 2
  density = 1
  expand = 3
  formula = G4_TOLUENE
  name = G4_TOLUENE
  specific = 4
FEATURE [App::DocumentObjectGroupPython] C_element115  label="C_element : 062"  # scripted group (container) (typed FeaturePython)
  n = 2
  ref = C_element
FEATURE [App::DocumentObjectGroupPython] H_element105  label="H_element : 056"  # scripted group (container) (typed FeaturePython)
  n = 1
  ref = H_element
FEATURE [App::DocumentObjectGroupPython] Cl_element028  label="Cl_element : 014"  # scripted group (container) (typed FeaturePython)
  n = 3
  ref = Cl_element
FEATURE [App::DocumentObjectGroupPython] G4_TRICHLOROETHYLENE  # scripted group (container) (typed FeaturePython)
  Dunit = g/cm3
  Dvalue = 1.46
  Group = -> [C_element115,H_element105,Cl_element028]
  conduct = 2
  density = 1
  expand = 3
  formula = G4_TRICHLOROETHYLENE
  name = G4_TRICHLOROETHYLENE
  specific = 4
FEATURE [App::DocumentObjectGroupPython] C_element116  label="C_element : 063"  # scripted group (container) (typed FeaturePython)
  n = 6
  ref = C_element
FEATURE [App::DocumentObjectGroupPython] H_element106  label="H_element : 15"  # scripted group (container) (typed FeaturePython)
  n = 15
  ref = H_element
FEATURE [App::DocumentObjectGroupPython] O_element099  label="O_element : 053"  # scripted group (container) (typed FeaturePython)
  n = 4
  ref = O_element
FEATURE [App::DocumentObjectGroupPython] P_element012  label="P_element : 1"  # scripted group (container) (typed FeaturePython)
  n = 1
  ref = P_element
FEATURE [App::DocumentObjectGroupPython] G4_TRIETHYL_PHOSPHATE  # scripted group (container) (typed FeaturePython)
  Dunit = g/cm3
  Dvalue = 1.07
  Group = -> [C_element116,H_element106,O_element099,P_element012]
  conduct = 2
  density = 1
  expand = 3
  formula = G4_TRIETHYL_PHOSPHATE
  name = G4_TRIETHYL_PHOSPHATE
  specific = 4
FEATURE [App::DocumentObjectGroupPython] W_element003  label="W_element : 003"  # scripted group (container) (typed FeaturePython)
  n = 1
  ref = W_element
FEATURE [App::DocumentObjectGroupPython] F_element017  label="F_element : 6"  # scripted group (container) (typed FeaturePython)
  n = 6
  ref = F_element
FEATURE [App::DocumentObjectGroupPython] G4_TUNGSTEN_HEXAFLUORIDE  # scripted group (container) (typed FeaturePython)
  Dunit = g/cm3
  Dvalue = 2.4
  Group = -> [W_element003,F_element017]
  conduct = 2
  density = 1
  expand = 3
  formula = G4_TUNGSTEN_HEXAFLUORIDE
  name = G4_TUNGSTEN_HEXAFLUORIDE
  specific = 4
FEATURE [App::DocumentObjectGroupPython] U_element001  label="U_element : 1"  # scripted group (container) (typed FeaturePython)
  n = 1
  ref = U_element
FEATURE [App::DocumentObjectGroupPython] C_element117  label="C_element : 064"  # scripted group (container) (typed FeaturePython)
  n = 2
  ref = C_element
FEATURE [App::DocumentObjectGroupPython] G4_URANIUM_DICARBIDE  # scripted group (container) (typed FeaturePython)
  Dunit = g/cm3
  Dvalue = 11.28
  Group = -> [U_element001,C_element117]
  conduct = 2
  density = 1
  expand = 3
  formula = G4_URANIUM_DICARBIDE
  name = G4_URANIUM_DICARBIDE
  specific = 4
FEATURE [App::DocumentObjectGroupPython] U_element002  label="U_element : 002"  # scripted group (container) (typed FeaturePython)
  n = 1
  ref = U_element
FEATURE [App::DocumentObjectGroupPython] C_element118  label="C_element : 065"  # scripted group (container) (typed FeaturePython)
  n = 1
  ref = C_element
FEATURE [App::DocumentObjectGroupPython] G4_URANIUM_MONOCARBIDE  # scripted group (container) (typed FeaturePython)
  Dunit = g/cm3
  Dvalue = 13.63
  Group = -> [U_element002,C_element118]
  conduct = 2
  density = 1
  expand = 3
  formula = G4_URANIUM_MONOCARBIDE
  name = G4_URANIUM_MONOCARBIDE
  specific = 4
FEATURE [App::DocumentObjectGroupPython] U_element003  label="U_element : 003"  # scripted group (container) (typed FeaturePython)
  n = 1
  ref = U_element
FEATURE [App::DocumentObjectGroupPython] O_element100  label="O_element : 054"  # scripted group (container) (typed FeaturePython)
  n = 2
  ref = O_element
FEATURE [App::DocumentObjectGroupPython] G4_URANIUM_OXIDE  # scripted group (container) (typed FeaturePython)
  Dunit = g/cm3
  Dvalue = 10.96
  Group = -> [U_element003,O_element100]
  conduct = 2
  density = 1
  expand = 3
  formula = G4_URANIUM_OXIDE
  name = G4_URANIUM_OXIDE
  specific = 4
FEATURE [App::DocumentObjectGroupPython] C_element119  label="C_element : 066"  # scripted group (container) (typed FeaturePython)
  n = 1
  ref = C_element
FEATURE [App::DocumentObjectGroupPython] H_element107  label="H_element : 057"  # scripted group (container) (typed FeaturePython)
  n = 4
  ref = H_element
FEATURE [App::DocumentObjectGroupPython] N_element046  label="N_element : 019"  # scripted group (container) (typed FeaturePython)
  n = 2
  ref = N_element
FEATURE [App::DocumentObjectGroupPython] O_element101  label="O_element : 055"  # scripted group (container) (typed FeaturePython)
  n = 1
  ref = O_element
FEATURE [App::DocumentObjectGroupPython] G4_UREA  # scripted group (container) (typed FeaturePython)
  Dunit = g/cm3
  Dvalue = 1.323
  Group = -> [C_element119,H_element107,N_element046,O_element101]
  conduct = 2
  density = 1
  expand = 3
  formula = G4_UREA
  name = G4_UREA
  specific = 4
FEATURE [App::DocumentObjectGroupPython] C_element120  label="C_element : 067"  # scripted group (container) (typed FeaturePython)
  n = 5
  ref = C_element
FEATURE [App::DocumentObjectGroupPython] H_element108  label="H_element : 058"  # scripted group (container) (typed FeaturePython)
  n = 11
  ref = H_element
FEATURE [App::DocumentObjectGroupPython] N_element047  label="N_element : 020"  # scripted group (container) (typed FeaturePython)
  n = 1
  ref = N_element
FEATURE [App::DocumentObjectGroupPython] O_element102  label="O_element : 056"  # scripted group (container) (typed FeaturePython)
  n = 2
  ref = O_element
FEATURE [App::DocumentObjectGroupPython] G4_VALINE  # scripted group (container) (typed FeaturePython)
  Dunit = g/cm3
  Dvalue = 1.23
  Group = -> [C_element120,H_element108,N_element047,O_element102]
  conduct = 2
  density = 1
  expand = 3
  formula = G4_VALINE
  name = G4_VALINE
  specific = 4
FEATURE [App::DocumentObjectGroupPython] H_element109  label="H_element : 0.009"  # scripted group (container) (typed FeaturePython)
  n = 0.009417
FEATURE [App::DocumentObjectGroupPython] C_element121  label="C_element : 0.281"  # scripted group (container) (typed FeaturePython)
  n = 0.280555
FEATURE [App::DocumentObjectGroupPython] F_element018  label="F_element : 0.710"  # scripted group (container) (typed FeaturePython)
  n = 0.710028
FEATURE [App::DocumentObjectGroupPython] G4_VITON  # scripted group (container) (typed FeaturePython)
  Dunit = g/cm3
  Dvalue = 1.8
  Group = -> [H_element109,C_element121,F_element018]
  conduct = 2
  density = 1
  expand = 3
  formula = G4_VITON
  name = G4_VITON
  specific = 4
FEATURE [App::DocumentObjectGroupPython] H_element110  label="H_element : 059"  # scripted group (container) (typed FeaturePython)
  n = 2
  ref = H_element
FEATURE [App::DocumentObjectGroupPython] O_element103  label="O_element : 057"  # scripted group (container) (typed FeaturePython)
  n = 1
  ref = O_element
FEATURE [App::DocumentObjectGroupPython] G4_WATER  # scripted group (container) (typed FeaturePython)
  Dunit = g/cm3
  Dvalue = 1
  Group = -> [H_element110,O_element103]
  conduct = 2
  density = 1
  expand = 3
  formula = G4_WATER
  name = G4_WATER
  specific = 4
FEATURE [App::DocumentObjectGroupPython] H_element111  label="H_element : 060"  # scripted group (container) (typed FeaturePython)
  n = 2
  ref = H_element
FEATURE [App::DocumentObjectGroupPython] O_element104  label="O_element : 058"  # scripted group (container) (typed FeaturePython)
  n = 1
  ref = O_element
FEATURE [App::DocumentObjectGroupPython] G4_WATER_VAPOR  # scripted group (container) (typed FeaturePython)
  Dunit = g/cm3
  Dvalue = 0.000756182
  Group = -> [H_element111,O_element104]
  conduct = 2
  density = 1
  expand = 3
  formula = G4_WATER_VAPOR
  name = G4_WATER_VAPOR
  specific = 4
FEATURE [App::DocumentObjectGroupPython] C_element122  label="C_element : 068"  # scripted group (container) (typed FeaturePython)
  n = 8
  ref = C_element
FEATURE [App::DocumentObjectGroupPython] H_element112  label="H_element : 061"  # scripted group (container) (typed FeaturePython)
  n = 10
  ref = H_element
FEATURE [App::DocumentObjectGroupPython] G4_XYLENE  # scripted group (container) (typed FeaturePython)
  Dunit = g/cm3
  Dvalue = 0.87
  Group = -> [C_element122,H_element112]
  conduct = 2
  density = 1
  expand = 3
  formula = G4_XYLENE
  name = G4_XYLENE
  specific = 4
FEATURE [App::DocumentObjectGroupPython] C_element123  label="C_element : 069"  # scripted group (container) (typed FeaturePython)
  n = 1
  ref = C_element
FEATURE [App::DocumentObjectGroupPython] G4_GRAPHITE  # scripted group (container) (typed FeaturePython)
  Dunit = g/cm3
  Dvalue = 2.21
  Group = -> [C_element123]
  conduct = 2
  density = 1
  expand = 3
  formula = G4_GRAPHITE
  name = G4_GRAPHITE
  specific = 4
FEATURE [App::DocumentObjectGroupPython] NIST  # scripted group (container) (typed FeaturePython)
  Group = -> [G4_A_150_TISSUE,G4_ACETONE,G4_ACETYLENE,G4_ADENINE,G4_ADIPOSE_TISSUE_ICRP,G4_AIR,G4_ALANINE,G4_ALUMINUM_OXIDE,G4_AMBER,G4_AMMONIA,G4_ANILINE,G4_ANTHRACENE,G4_B_100_BONE,G4_BAKELITE,G4_BARIUM_FLUORIDE,G4_BARIUM_SULFATE,G4_BENZENE,G4_BERYLLIUM_OXIDE,G4_BGO,G4_BLOOD_ICRP,G4_BONE_COMPACT_ICRU,G4_BONE_CORTICAL_ICRP,G4_BORON_CARBIDE,G4_BORON_OXIDE,G4_BRAIN_ICRP,G4_BUTANE,G4_N_BUTYL_ALCOHOL,G4_C_552,+152 more]
FEATURE [App::DocumentObjectGroupPython] H_element113  label="H_element : 062"  # scripted group (container) (typed FeaturePython)
  n = 1
  ref = H_element
FEATURE [App::DocumentObjectGroupPython] G4_H  # scripted group (container) (typed FeaturePython)
  Dunit = g/cm3
  Dvalue = 8.3748e-05
  Group = -> [H_element113]
  conduct = 2
  density = 1
  expand = 3
  formula = H
  name = G4_H
  specific = 4
FEATURE [App::DocumentObjectGroupPython] He_element001  label="He_element : 1"  # scripted group (container) (typed FeaturePython)
  n = 1
  ref = He_element
FEATURE [App::DocumentObjectGroupPython] G4_He  # scripted group (container) (typed FeaturePython)
  Dunit = g/cm3
  Dvalue = 0.000166322
  Group = -> [He_element001]
  conduct = 2
  density = 1
  expand = 3
  formula = He
  name = G4_He
  specific = 4
FEATURE [App::DocumentObjectGroupPython] Li_element008  label="Li_element : 008"  # scripted group (container) (typed FeaturePython)
  n = 1
  ref = Li_element
FEATURE [App::DocumentObjectGroupPython] G4_Li  # scripted group (container) (typed FeaturePython)
  Dunit = g/cm3
  Dvalue = 0.534
  Group = -> [Li_element008]
  conduct = 2
  density = 1
  expand = 3
  formula = Li
  name = G4_Li
  specific = 4
FEATURE [App::DocumentObjectGroupPython] Be_element002  label="Be_element : 002"  # scripted group (container) (typed FeaturePython)
  n = 1
  ref = Be_element
FEATURE [App::DocumentObjectGroupPython] G4_Be  # scripted group (container) (typed FeaturePython)
  Dunit = g/cm3
  Dvalue = 1.848
  Group = -> [Be_element002]
  conduct = 2
  density = 1
  expand = 3
  formula = Be
  name = G4_Be
  specific = 4
FEATURE [App::DocumentObjectGroupPython] B_element007  label="B_element : 007"  # scripted group (container) (typed FeaturePython)
  n = 1
  ref = B_element
FEATURE [App::DocumentObjectGroupPython] G4_B  # scripted group (container) (typed FeaturePython)
  Dunit = g/cm3
  Dvalue = 2.37
  Group = -> [B_element007]
  conduct = 2
  density = 1
  expand = 3
  formula = B
  name = G4_B
  specific = 4
FEATURE [App::DocumentObjectGroupPython] C_element124  label="C_element : 070"  # scripted group (container) (typed FeaturePython)
  n = 1
  ref = C_element
FEATURE [App::DocumentObjectGroupPython] G4_C  # scripted group (container) (typed FeaturePython)
  Dunit = g/cm3
  Dvalue = 2
  Group = -> [C_element124]
  conduct = 2
  density = 1
  expand = 3
  formula = C
  name = G4_C
  specific = 4
FEATURE [App::DocumentObjectGroupPython] N_element048  label="N_element : 021"  # scripted group (container) (typed FeaturePython)
  n = 1
  ref = N_element
FEATURE [App::DocumentObjectGroupPython] G4_N  # scripted group (container) (typed FeaturePython)
  Dunit = g/cm3
  Dvalue = 0.0011652
  Group = -> [N_element048]
  conduct = 2
  density = 1
  expand = 3
  formula = N
  name = G4_N
  specific = 4
FEATURE [App::DocumentObjectGroupPython] O_element105  label="O_element : 059"  # scripted group (container) (typed FeaturePython)
  n = 1
  ref = O_element
FEATURE [App::DocumentObjectGroupPython] G4_O  # scripted group (container) (typed FeaturePython)
  Dunit = g/cm3
  Dvalue = 0.00133151
  Group = -> [O_element105]
  conduct = 2
  density = 1
  expand = 3
  formula = O
  name = G4_O
  specific = 4
FEATURE [App::DocumentObjectGroupPython] F_element019  label="F_element : 008"  # scripted group (container) (typed FeaturePython)
  n = 1
  ref = F_element
FEATURE [App::DocumentObjectGroupPython] G4_F  # scripted group (container) (typed FeaturePython)
  Dunit = g/cm3
  Dvalue = 0.00158029
  Group = -> [F_element019]
  conduct = 2
  density = 1
  expand = 3
  formula = F
  name = G4_F
  specific = 4
FEATURE [App::DocumentObjectGroupPython] Ne_element001  label="Ne_element : 1"  # scripted group (container) (typed FeaturePython)
  n = 1
  ref = Ne_element
FEATURE [App::DocumentObjectGroupPython] G4_Ne  # scripted group (container) (typed FeaturePython)
  Dunit = g/cm3
  Dvalue = 0.000838505
  Group = -> [Ne_element001]
  conduct = 2
  density = 1
  expand = 3
  formula = Ne
  name = G4_Ne
  specific = 4
FEATURE [App::DocumentObjectGroupPython] Na_element020  label="Na_element : 005"  # scripted group (container) (typed FeaturePython)
  n = 1
  ref = Na_element
FEATURE [App::DocumentObjectGroupPython] G4_Na  # scripted group (container) (typed FeaturePython)
  Dunit = g/cm3
  Dvalue = 0.971
  Group = -> [Na_element020]
  conduct = 2
  density = 1
  expand = 3
  formula = Na
  name = G4_Na
  specific = 4
FEATURE [App::DocumentObjectGroupPython] Mg_element011  label="Mg_element : 005"  # scripted group (container) (typed FeaturePython)
  n = 1
  ref = Mg_element
FEATURE [App::DocumentObjectGroupPython] G4_Mg  # scripted group (container) (typed FeaturePython)
  Dunit = g/cm3
  Dvalue = 1.74
  Group = -> [Mg_element011]
  conduct = 2
  density = 1
  expand = 3
  formula = Mg
  name = G4_Mg
  specific = 4
FEATURE [App::DocumentObjectGroupPython] Al_element004  label="Al_element : 1"  # scripted group (container) (typed FeaturePython)
  n = 1
  ref = Al_element
FEATURE [App::DocumentObjectGroupPython] G4_Al  # scripted group (container) (typed FeaturePython)
  Dunit = g/cm3
  Dvalue = 2.699
  Group = -> [Al_element004]
  conduct = 2
  density = 1
  expand = 3
  formula = Al
  name = G4_Al
  specific = 4
FEATURE [App::DocumentObjectGroupPython] Si_element007  label="Si_element : 002"  # scripted group (container) (typed FeaturePython)
  n = 1
  ref = Si_element
FEATURE [App::DocumentObjectGroupPython] G4_Si  # scripted group (container) (typed FeaturePython)
  Dunit = g/cm3
  Dvalue = 2.33
  Group = -> [Si_element007]
  conduct = 2
  density = 1
  expand = 3
  formula = Si
  name = G4_Si
  specific = 4
FEATURE [App::DocumentObjectGroupPython] P_element013  label="P_element : 002"  # scripted group (container) (typed FeaturePython)
  n = 1
  ref = P_element
FEATURE [App::DocumentObjectGroupPython] G4_P  # scripted group (container) (typed FeaturePython)
  Dunit = g/cm3
  Dvalue = 2.2
  Group = -> [P_element013]
  conduct = 2
  density = 1
  expand = 3
  formula = P
  name = G4_P
  specific = 4
FEATURE [App::DocumentObjectGroupPython] S_element023  label="S_element : 007"  # scripted group (container) (typed FeaturePython)
  n = 1
  ref = S_element
FEATURE [App::DocumentObjectGroupPython] G4_S  # scripted group (container) (typed FeaturePython)
  Dunit = g/cm3
  Dvalue = 2
  Group = -> [S_element023]
  conduct = 2
  density = 1
  expand = 3
  formula = S
  name = G4_S
  specific = 4
FEATURE [App::DocumentObjectGroupPython] Cl_element029  label="Cl_element : 015"  # scripted group (container) (typed FeaturePython)
  n = 1
  ref = Cl_element
FEATURE [App::DocumentObjectGroupPython] G4_Cl  # scripted group (container) (typed FeaturePython)
  Dunit = g/cm3
  Dvalue = 0.00299473
  Group = -> [Cl_element029]
  conduct = 2
  density = 1
  expand = 3
  formula = Cl
  name = G4_Cl
  specific = 4
FEATURE [App::DocumentObjectGroupPython] Ar_element002  label="Ar_element : 1"  # scripted group (container) (typed FeaturePython)
  n = 1
  ref = Ar_element
FEATURE [App::DocumentObjectGroupPython] G4_Ar  # scripted group (container) (typed FeaturePython)
  Dunit = g/cm3
  Dvalue = 0.00166201
  Group = -> [Ar_element002]
  conduct = 2
  density = 1
  expand = 3
  formula = Ar
  name = G4_Ar
  specific = 4
FEATURE [App::DocumentObjectGroupPython] K_element013  label="K_element : 003"  # scripted group (container) (typed FeaturePython)
  n = 1
  ref = K_element
FEATURE [App::DocumentObjectGroupPython] G4_K  # scripted group (container) (typed FeaturePython)
  Dunit = g/cm3
  Dvalue = 0.862
  Group = -> [K_element013]
  conduct = 2
  density = 1
  expand = 3
  formula = K
  name = G4_K
  specific = 4
FEATURE [App::DocumentObjectGroupPython] Ca_element014  label="Ca_element : 007"  # scripted group (container) (typed FeaturePython)
  n = 1
  ref = Ca_element
FEATURE [App::DocumentObjectGroupPython] G4_Ca  # scripted group (container) (typed FeaturePython)
  Dunit = g/cm3
  Dvalue = 1.55
  Group = -> [Ca_element014]
  conduct = 2
  density = 1
  expand = 3
  formula = Ca
  name = G4_Ca
  specific = 4
FEATURE [App::DocumentObjectGroupPython] Sc_element001  label="Sc_element : 1"  # scripted group (container) (typed FeaturePython)
  n = 1
  ref = Sc_element
FEATURE [App::DocumentObjectGroupPython] G4_Sc  # scripted group (container) (typed FeaturePython)
  Dunit = g/cm3
  Dvalue = 2.989
  Group = -> [Sc_element001]
  conduct = 2
  density = 1
  expand = 3
  formula = Sc
  name = G4_Sc
  specific = 4
FEATURE [App::DocumentObjectGroupPython] Ti_element004  label="Ti_element : 002"  # scripted group (container) (typed FeaturePython)
  n = 1
  ref = Ti_element
FEATURE [App::DocumentObjectGroupPython] G4_Ti  # scripted group (container) (typed FeaturePython)
  Dunit = g/cm3
  Dvalue = 4.54
  Group = -> [Ti_element004]
  conduct = 2
  density = 1
  expand = 3
  formula = Ti
  name = G4_Ti
  specific = 4
FEATURE [App::DocumentObjectGroupPython] V_element001  label="V_element : 1"  # scripted group (container) (typed FeaturePython)
  n = 1
  ref = V_element
FEATURE [App::DocumentObjectGroupPython] G4_V  # scripted group (container) (typed FeaturePython)
  Dunit = g/cm3
  Dvalue = 6.11
  Group = -> [V_element001]
  conduct = 2
  density = 1
  expand = 3
  formula = V
  name = G4_V
  specific = 4
FEATURE [App::DocumentObjectGroupPython] Cr_element001  label="Cr_element : 1"  # scripted group (container) (typed FeaturePython)
  n = 1
  ref = Cr_element
FEATURE [App::DocumentObjectGroupPython] G4_Cr  # scripted group (container) (typed FeaturePython)
  Dunit = g/cm3
  Dvalue = 7.18
  Group = -> [Cr_element001]
  conduct = 2
  density = 1
  expand = 3
  formula = Cr
  name = G4_Cr
  specific = 4
FEATURE [App::DocumentObjectGroupPython] Mn_element001  label="Mn_element : 1"  # scripted group (container) (typed FeaturePython)
  n = 1
  ref = Mn_element
FEATURE [App::DocumentObjectGroupPython] G4_Mn  # scripted group (container) (typed FeaturePython)
  Dunit = g/cm3
  Dvalue = 7.44
  Group = -> [Mn_element001]
  conduct = 2
  density = 1
  expand = 3
  formula = Mn
  name = G4_Mn
  specific = 4
FEATURE [App::DocumentObjectGroupPython] Fe_element007  label="Fe_element : 004"  # scripted group (container) (typed FeaturePython)
  n = 1
  ref = Fe_element
FEATURE [App::DocumentObjectGroupPython] G4_Fe  # scripted group (container) (typed FeaturePython)
  Dunit = g/cm3
  Dvalue = 7.874
  Group = -> [Fe_element007]
  conduct = 2
  density = 1
  expand = 3
  formula = Fe
  name = G4_Fe
  specific = 4
FEATURE [App::DocumentObjectGroupPython] Co_element001  label="Co_element : 1"  # scripted group (container) (typed FeaturePython)
  n = 1
  ref = Co_element
FEATURE [App::DocumentObjectGroupPython] G4_Co  # scripted group (container) (typed FeaturePython)
  Dunit = g/cm3
  Dvalue = 8.9
  Group = -> [Co_element001]
  conduct = 2
  density = 1
  expand = 3
  formula = Co
  name = G4_Co
  specific = 4
FEATURE [App::DocumentObjectGroupPython] Ni_element001  label="Ni_element : 1"  # scripted group (container) (typed FeaturePython)
  n = 1
  ref = Ni_element
FEATURE [App::DocumentObjectGroupPython] G4_Ni  # scripted group (container) (typed FeaturePython)
  Dunit = g/cm3
  Dvalue = 8.902
  Group = -> [Ni_element001]
  conduct = 2
  density = 1
  expand = 3
  formula = Ni
  name = G4_Ni
  specific = 4
FEATURE [App::DocumentObjectGroupPython] Cu_element001  label="Cu_element : 1"  # scripted group (container) (typed FeaturePython)
  n = 1
  ref = Cu_element
FEATURE [App::DocumentObjectGroupPython] G4_Cu  # scripted group (container) (typed FeaturePython)
  Dunit = g/cm3
  Dvalue = 8.96
  Group = -> [Cu_element001]
  conduct = 2
  density = 1
  expand = 3
  formula = Cu
  name = G4_Cu
  specific = 4
FEATURE [App::DocumentObjectGroupPython] Zn_element001  label="Zn_element : 1"  # scripted group (container) (typed FeaturePython)
  n = 1
  ref = Zn_element
FEATURE [App::DocumentObjectGroupPython] G4_Zn  # scripted group (container) (typed FeaturePython)
  Dunit = g/cm3
  Dvalue = 7.133
  Group = -> [Zn_element001]
  conduct = 2
  density = 1
  expand = 3
  formula = Zn
  name = G4_Zn
  specific = 4
FEATURE [App::DocumentObjectGroupPython] Ga_element002  label="Ga_element : 002"  # scripted group (container) (typed FeaturePython)
  n = 1
  ref = Ga_element
FEATURE [App::DocumentObjectGroupPython] G4_Ga  # scripted group (container) (typed FeaturePython)
  Dunit = g/cm3
  Dvalue = 5.904
  Group = -> [Ga_element002]
  conduct = 2
  density = 1
  expand = 3
  formula = Ga
  name = G4_Ga
  specific = 4
FEATURE [App::DocumentObjectGroupPython] Ge_element002  label="Ge_element : 1"  # scripted group (container) (typed FeaturePython)
  n = 1
  ref = Ge_element
FEATURE [App::DocumentObjectGroupPython] G4_Ge  # scripted group (container) (typed FeaturePython)
  Dunit = g/cm3
  Dvalue = 5.323
  Group = -> [Ge_element002]
  conduct = 2
  density = 1
  expand = 3
  formula = Ge
  name = G4_Ge
  specific = 4
FEATURE [App::DocumentObjectGroupPython] As_element003  label="As_element : 002"  # scripted group (container) (typed FeaturePython)
  n = 1
  ref = As_element
FEATURE [App::DocumentObjectGroupPython] G4_As  # scripted group (container) (typed FeaturePython)
  Dunit = g/cm3
  Dvalue = 5.73
  Group = -> [As_element003]
  conduct = 2
  density = 1
  expand = 3
  formula = As
  name = G4_As
  specific = 4
FEATURE [App::DocumentObjectGroupPython] Se_element001  label="Se_element : 1"  # scripted group (container) (typed FeaturePython)
  n = 1
  ref = Se_element
FEATURE [App::DocumentObjectGroupPython] G4_Se  # scripted group (container) (typed FeaturePython)
  Dunit = g/cm3
  Dvalue = 4.5
  Group = -> [Se_element001]
  conduct = 2
  density = 1
  expand = 3
  formula = Se
  name = G4_Se
  specific = 4
FEATURE [App::DocumentObjectGroupPython] Br_element007  label="Br_element : 004"  # scripted group (container) (typed FeaturePython)
  n = 1
  ref = Br_element
FEATURE [App::DocumentObjectGroupPython] G4_Br  # scripted group (container) (typed FeaturePython)
  Dunit = g/cm3
  Dvalue = 0.0070721
  Group = -> [Br_element007]
  conduct = 2
  density = 1
  expand = 3
  formula = Br
  name = G4_Br
  specific = 4
FEATURE [App::DocumentObjectGroupPython] Kr_element001  label="Kr_element : 1"  # scripted group (container) (typed FeaturePython)
  n = 1
  ref = Kr_element
FEATURE [App::DocumentObjectGroupPython] G4_Kr  # scripted group (container) (typed FeaturePython)
  Dunit = g/cm3
  Dvalue = 0.00347832
  Group = -> [Kr_element001]
  conduct = 2
  density = 1
  expand = 3
  formula = Kr
  name = G4_Kr
  specific = 4
FEATURE [App::DocumentObjectGroupPython] Rb_element001  label="Rb_element : 1"  # scripted group (container) (typed FeaturePython)
  n = 1
  ref = Rb_element
FEATURE [App::DocumentObjectGroupPython] G4_Rb  # scripted group (container) (typed FeaturePython)
  Dunit = g/cm3
  Dvalue = 1.532
  Group = -> [Rb_element001]
  conduct = 2
  density = 1
  expand = 3
  formula = Rb
  name = G4_Rb
  specific = 4
FEATURE [App::DocumentObjectGroupPython] Sr_element001  label="Sr_element : 1"  # scripted group (container) (typed FeaturePython)
  n = 1
  ref = Sr_element
FEATURE [App::DocumentObjectGroupPython] G4_Sr  # scripted group (container) (typed FeaturePython)
  Dunit = g/cm3
  Dvalue = 2.54
  Group = -> [Sr_element001]
  conduct = 2
  density = 1
  expand = 3
  formula = Sr
  name = G4_Sr
  specific = 4
FEATURE [App::DocumentObjectGroupPython] Y_element001  label="Y_element : 1"  # scripted group (container) (typed FeaturePython)
  n = 1
  ref = Y_element
FEATURE [App::DocumentObjectGroupPython] G4_Y  # scripted group (container) (typed FeaturePython)
  Dunit = g/cm3
  Dvalue = 4.469
  Group = -> [Y_element001]
  conduct = 2
  density = 1
  expand = 3
  formula = Y
  name = G4_Y
  specific = 4
FEATURE [App::DocumentObjectGroupPython] Zr_element001  label="Zr_element : 1"  # scripted group (container) (typed FeaturePython)
  n = 1
  ref = Zr_element
FEATURE [App::DocumentObjectGroupPython] G4_Zr  # scripted group (container) (typed FeaturePython)
  Dunit = g/cm3
  Dvalue = 6.506
  Group = -> [Zr_element001]
  conduct = 2
  density = 1
  expand = 3
  formula = Zr
  name = G4_Zr
  specific = 4
FEATURE [App::DocumentObjectGroupPython] Nb_element001  label="Nb_element : 1"  # scripted group (container) (typed FeaturePython)
  n = 1
  ref = Nb_element
FEATURE [App::DocumentObjectGroupPython] G4_Nb  # scripted group (container) (typed FeaturePython)
  Dunit = g/cm3
  Dvalue = 8.57
  Group = -> [Nb_element001]
  conduct = 2
  density = 1
  expand = 3
  formula = Nb
  name = G4_Nb
  specific = 4
FEATURE [App::DocumentObjectGroupPython] Mo_element001  label="Mo_element : 1"  # scripted group (container) (typed FeaturePython)
  n = 1
  ref = Mo_element
FEATURE [App::DocumentObjectGroupPython] G4_Mo  # scripted group (container) (typed FeaturePython)
  Dunit = g/cm3
  Dvalue = 10.22
  Group = -> [Mo_element001]
  conduct = 2
  density = 1
  expand = 3
  formula = Mo
  name = G4_Mo
  specific = 4
FEATURE [App::DocumentObjectGroupPython] Tc_element001  label="Tc_element : 1"  # scripted group (container) (typed FeaturePython)
  n = 1
  ref = Tc_element
FEATURE [App::DocumentObjectGroupPython] G4_Tc  # scripted group (container) (typed FeaturePython)
  Dunit = g/cm3
  Dvalue = 11.5
  Group = -> [Tc_element001]
  conduct = 2
  density = 1
  expand = 3
  formula = Tc
  name = G4_Tc
  specific = 4
FEATURE [App::DocumentObjectGroupPython] Ru_element001  label="Ru_element : 1"  # scripted group (container) (typed FeaturePython)
  n = 1
  ref = Ru_element
FEATURE [App::DocumentObjectGroupPython] G4_Ru  # scripted group (container) (typed FeaturePython)
  Dunit = g/cm3
  Dvalue = 12.41
  Group = -> [Ru_element001]
  conduct = 2
  density = 1
  expand = 3
  formula = Ru
  name = G4_Ru
  specific = 4
FEATURE [App::DocumentObjectGroupPython] Rh_element001  label="Rh_element : 1"  # scripted group (container) (typed FeaturePython)
  n = 1
  ref = Rh_element
FEATURE [App::DocumentObjectGroupPython] G4_Rh  # scripted group (container) (typed FeaturePython)
  Dunit = g/cm3
  Dvalue = 12.41
  Group = -> [Rh_element001]
  conduct = 2
  density = 1
  expand = 3
  formula = Rh
  name = G4_Rh
  specific = 4
FEATURE [App::DocumentObjectGroupPython] Pd_element001  label="Pd_element : 1"  # scripted group (container) (typed FeaturePython)
  n = 1
  ref = Pd_element
FEATURE [App::DocumentObjectGroupPython] G4_Pd  # scripted group (container) (typed FeaturePython)
  Dunit = g/cm3
  Dvalue = 12.02
  Group = -> [Pd_element001]
  conduct = 2
  density = 1
  expand = 3
  formula = Pd
  name = G4_Pd
  specific = 4
FEATURE [App::DocumentObjectGroupPython] Ag_element006  label="Ag_element : 004"  # scripted group (container) (typed FeaturePython)
  n = 1
  ref = Ag_element
FEATURE [App::DocumentObjectGroupPython] G4_Ag  # scripted group (container) (typed FeaturePython)
  Dunit = g/cm3
  Dvalue = 10.5
  Group = -> [Ag_element006]
  conduct = 2
  density = 1
  expand = 3
  formula = Ag
  name = G4_Ag
  specific = 4
FEATURE [App::DocumentObjectGroupPython] Cd_element003  label="Cd_element : 003"  # scripted group (container) (typed FeaturePython)
  n = 1
  ref = Cd_element
FEATURE [App::DocumentObjectGroupPython] G4_Cd  # scripted group (container) (typed FeaturePython)
  Dunit = g/cm3
  Dvalue = 8.65
  Group = -> [Cd_element003]
  conduct = 2
  density = 1
  expand = 3
  formula = Cd
  name = G4_Cd
  specific = 4
FEATURE [App::DocumentObjectGroupPython] In_element001  label="In_element : 1"  # scripted group (container) (typed FeaturePython)
  n = 1
  ref = In_element
FEATURE [App::DocumentObjectGroupPython] G4_In  # scripted group (container) (typed FeaturePython)
  Dunit = g/cm3
  Dvalue = 7.31
  Group = -> [In_element001]
  conduct = 2
  density = 1
  expand = 3
  formula = In
  name = G4_In
  specific = 4
FEATURE [App::DocumentObjectGroupPython] Sn_element001  label="Sn_element : 1"  # scripted group (container) (typed FeaturePython)
  n = 1
  ref = Sn_element
FEATURE [App::DocumentObjectGroupPython] G4_Sn  # scripted group (container) (typed FeaturePython)
  Dunit = g/cm3
  Dvalue = 7.31
  Group = -> [Sn_element001]
  conduct = 2
  density = 1
  expand = 3
  formula = Sn
  name = G4_Sn
  specific = 4
FEATURE [App::DocumentObjectGroupPython] Sb_element001  label="Sb_element : 1"  # scripted group (container) (typed FeaturePython)
  n = 1
  ref = Sb_element
FEATURE [App::DocumentObjectGroupPython] G4_Sb  # scripted group (container) (typed FeaturePython)
  Dunit = g/cm3
  Dvalue = 6.691
  Group = -> [Sb_element001]
  conduct = 2
  density = 1
  expand = 3
  formula = Sb
  name = G4_Sb
  specific = 4
FEATURE [App::DocumentObjectGroupPython] Te_element002  label="Te_element : 002"  # scripted group (container) (typed FeaturePython)
  n = 1
  ref = Te_element
FEATURE [App::DocumentObjectGroupPython] G4_Te  # scripted group (container) (typed FeaturePython)
  Dunit = g/cm3
  Dvalue = 6.24
  Group = -> [Te_element002]
  conduct = 2
  density = 1
  expand = 3
  formula = Te
  name = G4_Te
  specific = 4
FEATURE [App::DocumentObjectGroupPython] I_element010  label="I_element : 006"  # scripted group (container) (typed FeaturePython)
  n = 1
  ref = I_element
FEATURE [App::DocumentObjectGroupPython] G4_I  # scripted group (container) (typed FeaturePython)
  Dunit = g/cm3
  Dvalue = 4.93
  Group = -> [I_element010]
  conduct = 2
  density = 1
  expand = 3
  formula = I
  name = G4_I
  specific = 4
FEATURE [App::DocumentObjectGroupPython] Xe_element001  label="Xe_element : 1"  # scripted group (container) (typed FeaturePython)
  n = 1
  ref = Xe_element
FEATURE [App::DocumentObjectGroupPython] G4_Xe  # scripted group (container) (typed FeaturePython)
  Dunit = g/cm3
  Dvalue = 0.00548536
  Group = -> [Xe_element001]
  conduct = 2
  density = 1
  expand = 3
  formula = Xe
  name = G4_Xe
  specific = 4
FEATURE [App::DocumentObjectGroupPython] Cs_element003  label="Cs_element : 003"  # scripted group (container) (typed FeaturePython)
  n = 1
  ref = Cs_element
FEATURE [App::DocumentObjectGroupPython] G4_Cs  # scripted group (container) (typed FeaturePython)
  Dunit = g/cm3
  Dvalue = 1.873
  Group = -> [Cs_element003]
  conduct = 2
  density = 1
  expand = 3
  formula = Cs
  name = G4_Cs
  specific = 4
FEATURE [App::DocumentObjectGroupPython] Ba_element003  label="Ba_element : 003"  # scripted group (container) (typed FeaturePython)
  n = 1
  ref = Ba_element
FEATURE [App::DocumentObjectGroupPython] G4_Ba  # scripted group (container) (typed FeaturePython)
  Dunit = g/cm3
  Dvalue = 3.5
  Group = -> [Ba_element003]
  conduct = 2
  density = 1
  expand = 3
  formula = Ba
  name = G4_Ba
  specific = 4
FEATURE [App::DocumentObjectGroupPython] La_element003  label="La_element : 003"  # scripted group (container) (typed FeaturePython)
  n = 1
  ref = La_element
FEATURE [App::DocumentObjectGroupPython] G4_La  # scripted group (container) (typed FeaturePython)
  Dunit = g/cm3
  Dvalue = 6.154
  Group = -> [La_element003]
  conduct = 2
  density = 1
  expand = 3
  formula = La
  name = G4_La
  specific = 4
FEATURE [App::DocumentObjectGroupPython] Ce_element002  label="Ce_element : 1"  # scripted group (container) (typed FeaturePython)
  n = 1
  ref = Ce_element
FEATURE [App::DocumentObjectGroupPython] G4_Ce  # scripted group (container) (typed FeaturePython)
  Dunit = g/cm3
  Dvalue = 6.657
  Group = -> [Ce_element002]
  conduct = 2
  density = 1
  expand = 3
  formula = Ce
  name = G4_Ce
  specific = 4
FEATURE [App::DocumentObjectGroupPython] Pr_element001  label="Pr_element : 1"  # scripted group (container) (typed FeaturePython)
  n = 1
  ref = Pr_element
FEATURE [App::DocumentObjectGroupPython] G4_Pr  # scripted group (container) (typed FeaturePython)
  Dunit = g/cm3
  Dvalue = 6.71
  Group = -> [Pr_element001]
  conduct = 2
  density = 1
  expand = 3
  formula = Pr
  name = G4_Pr
  specific = 4
FEATURE [App::DocumentObjectGroupPython] Nd_element001  label="Nd_element : 1"  # scripted group (container) (typed FeaturePython)
  n = 1
  ref = Nd_element
FEATURE [App::DocumentObjectGroupPython] G4_Nd  # scripted group (container) (typed FeaturePython)
  Dunit = g/cm3
  Dvalue = 6.9
  Group = -> [Nd_element001]
  conduct = 2
  density = 1
  expand = 3
  formula = Nd
  name = G4_Nd
  specific = 4
FEATURE [App::DocumentObjectGroupPython] Pm_element001  label="Pm_element : 1"  # scripted group (container) (typed FeaturePython)
  n = 1
  ref = Pm_element
FEATURE [App::DocumentObjectGroupPython] G4_Pm  # scripted group (container) (typed FeaturePython)
  Dunit = g/cm3
  Dvalue = 7.22
  Group = -> [Pm_element001]
  conduct = 2
  density = 1
  expand = 3
  formula = Pm
  name = G4_Pm
  specific = 4
FEATURE [App::DocumentObjectGroupPython] Sm_element001  label="Sm_element : 1"  # scripted group (container) (typed FeaturePython)
  n = 1
  ref = Sm_element
FEATURE [App::DocumentObjectGroupPython] G4_Sm  # scripted group (container) (typed FeaturePython)
  Dunit = g/cm3
  Dvalue = 7.46
  Group = -> [Sm_element001]
  conduct = 2
  density = 1
  expand = 3
  formula = Sm
  name = G4_Sm
  specific = 4
FEATURE [App::DocumentObjectGroupPython] Eu_element001  label="Eu_element : 1"  # scripted group (container) (typed FeaturePython)
  n = 1
  ref = Eu_element
FEATURE [App::DocumentObjectGroupPython] G4_Eu  # scripted group (container) (typed FeaturePython)
  Dunit = g/cm3
  Dvalue = 5.243
  Group = -> [Eu_element001]
  conduct = 2
  density = 1
  expand = 3
  formula = Eu
  name = G4_Eu
  specific = 4
FEATURE [App::DocumentObjectGroupPython] Gd_element002  label="Gd_element : 1"  # scripted group (container) (typed FeaturePython)
  n = 1
  ref = Gd_element
FEATURE [App::DocumentObjectGroupPython] G4_Gd  # scripted group (container) (typed FeaturePython)
  Dunit = g/cm3
  Dvalue = 7.9004
  Group = -> [Gd_element002]
  conduct = 2
  density = 1
  expand = 3
  formula = Gd
  name = G4_Gd
  specific = 4
FEATURE [App::DocumentObjectGroupPython] Tb_element001  label="Tb_element : 1"  # scripted group (container) (typed FeaturePython)
  n = 1
  ref = Tb_element
FEATURE [App::DocumentObjectGroupPython] G4_Tb  # scripted group (container) (typed FeaturePython)
  Dunit = g/cm3
  Dvalue = 8.229
  Group = -> [Tb_element001]
  conduct = 2
  density = 1
  expand = 3
  formula = Tb
  name = G4_Tb
  specific = 4
FEATURE [App::DocumentObjectGroupPython] Dy_element001  label="Dy_element : 1"  # scripted group (container) (typed FeaturePython)
  n = 1
  ref = Dy_element
FEATURE [App::DocumentObjectGroupPython] G4_Dy  # scripted group (container) (typed FeaturePython)
  Dunit = g/cm3
  Dvalue = 8.55
  Group = -> [Dy_element001]
  conduct = 2
  density = 1
  expand = 3
  formula = Dy
  name = G4_Dy
  specific = 4
FEATURE [App::DocumentObjectGroupPython] Ho_element001  label="Ho_element : 1"  # scripted group (container) (typed FeaturePython)
  n = 1
  ref = Ho_element
FEATURE [App::DocumentObjectGroupPython] G4_Ho  # scripted group (container) (typed FeaturePython)
  Dunit = g/cm3
  Dvalue = 8.795
  Group = -> [Ho_element001]
  conduct = 2
  density = 1
  expand = 3
  formula = Ho
  name = G4_Ho
  specific = 4
FEATURE [App::DocumentObjectGroupPython] Er_element001  label="Er_element : 1"  # scripted group (container) (typed FeaturePython)
  n = 1
  ref = Er_element
FEATURE [App::DocumentObjectGroupPython] G4_Er  # scripted group (container) (typed FeaturePython)
  Dunit = g/cm3
  Dvalue = 9.066
  Group = -> [Er_element001]
  conduct = 2
  density = 1
  expand = 3
  formula = Er
  name = G4_Er
  specific = 4
FEATURE [App::DocumentObjectGroupPython] Tm_element001  label="Tm_element : 1"  # scripted group (container) (typed FeaturePython)
  n = 1
  ref = Tm_element
FEATURE [App::DocumentObjectGroupPython] G4_Tm  # scripted group (container) (typed FeaturePython)
  Dunit = g/cm3
  Dvalue = 9.321
  Group = -> [Tm_element001]
  conduct = 2
  density = 1
  expand = 3
  formula = Tm
  name = G4_Tm
  specific = 4
FEATURE [App::DocumentObjectGroupPython] Yb_element001  label="Yb_element : 1"  # scripted group (container) (typed FeaturePython)
  n = 1
  ref = Yb_element
FEATURE [App::DocumentObjectGroupPython] G4_Yb  # scripted group (container) (typed FeaturePython)
  Dunit = g/cm3
  Dvalue = 6.73
  Group = -> [Yb_element001]
  conduct = 2
  density = 1
  expand = 3
  formula = Yb
  name = G4_Yb
  specific = 4
FEATURE [App::DocumentObjectGroupPython] Lu_element001  label="Lu_element : 1"  # scripted group (container) (typed FeaturePython)
  n = 1
  ref = Lu_element
FEATURE [App::DocumentObjectGroupPython] G4_Lu  # scripted group (container) (typed FeaturePython)
  Dunit = g/cm3
  Dvalue = 9.84
  Group = -> [Lu_element001]
  conduct = 2
  density = 1
  expand = 3
  formula = Lu
  name = G4_Lu
  specific = 4
FEATURE [App::DocumentObjectGroupPython] Hf_element001  label="Hf_element : 1"  # scripted group (container) (typed FeaturePython)
  n = 1
  ref = Hf_element
FEATURE [App::DocumentObjectGroupPython] G4_Hf  # scripted group (container) (typed FeaturePython)
  Dunit = g/cm3
  Dvalue = 13.31
  Group = -> [Hf_element001]
  conduct = 2
  density = 1
  expand = 3
  formula = Hf
  name = G4_Hf
  specific = 4
FEATURE [App::DocumentObjectGroupPython] Ta_element001  label="Ta_element : 1"  # scripted group (container) (typed FeaturePython)
  n = 1
  ref = Ta_element
FEATURE [App::DocumentObjectGroupPython] G4_Ta  # scripted group (container) (typed FeaturePython)
  Dunit = g/cm3
  Dvalue = 16.654
  Group = -> [Ta_element001]
  conduct = 2
  density = 1
  expand = 3
  formula = Ta
  name = G4_Ta
  specific = 4
FEATURE [App::DocumentObjectGroupPython] W_element004  label="W_element : 004"  # scripted group (container) (typed FeaturePython)
  n = 1
  ref = W_element
FEATURE [App::DocumentObjectGroupPython] G4_W  # scripted group (container) (typed FeaturePython)
  Dunit = g/cm3
  Dvalue = 19.3
  Group = -> [W_element004]
  conduct = 2
  density = 1
  expand = 3
  formula = W
  name = G4_W
  specific = 4
FEATURE [App::DocumentObjectGroupPython] Re_element001  label="Re_element : 1"  # scripted group (container) (typed FeaturePython)
  n = 1
  ref = Re_element
FEATURE [App::DocumentObjectGroupPython] G4_Re  # scripted group (container) (typed FeaturePython)
  Dunit = g/cm3
  Dvalue = 21.02
  Group = -> [Re_element001]
  conduct = 2
  density = 1
  expand = 3
  formula = Re
  name = G4_Re
  specific = 4
FEATURE [App::DocumentObjectGroupPython] Os_element001  label="Os_element : 1"  # scripted group (container) (typed FeaturePython)
  n = 1
  ref = Os_element
FEATURE [App::DocumentObjectGroupPython] G4_Os  # scripted group (container) (typed FeaturePython)
  Dunit = g/cm3
  Dvalue = 22.57
  Group = -> [Os_element001]
  conduct = 2
  density = 1
  expand = 3
  formula = Os
  name = G4_Os
  specific = 4
FEATURE [App::DocumentObjectGroupPython] Ir_element001  label="Ir_element : 1"  # scripted group (container) (typed FeaturePython)
  n = 1
  ref = Ir_element
FEATURE [App::DocumentObjectGroupPython] G4_Ir  # scripted group (container) (typed FeaturePython)
  Dunit = g/cm3
  Dvalue = 22.42
  Group = -> [Ir_element001]
  conduct = 2
  density = 1
  expand = 3
  formula = Ir
  name = G4_Ir
  specific = 4
FEATURE [App::DocumentObjectGroupPython] Pt_element001  label="Pt_element : 1"  # scripted group (container) (typed FeaturePython)
  n = 1
  ref = Pt_element
FEATURE [App::DocumentObjectGroupPython] G4_Pt  # scripted group (container) (typed FeaturePython)
  Dunit = g/cm3
  Dvalue = 21.45
  Group = -> [Pt_element001]
  conduct = 2
  density = 1
  expand = 3
  formula = Pt
  name = G4_Pt
  specific = 4
FEATURE [App::DocumentObjectGroupPython] Au_element001  label="Au_element : 1"  # scripted group (container) (typed FeaturePython)
  n = 1
  ref = Au_element
FEATURE [App::DocumentObjectGroupPython] G4_Au  # scripted group (container) (typed FeaturePython)
  Dunit = g/cm3
  Dvalue = 19.32
  Group = -> [Au_element001]
  conduct = 2
  density = 1
  expand = 3
  formula = Au
  name = G4_Au
  specific = 4
FEATURE [App::DocumentObjectGroupPython] Hg_element002  label="Hg_element : 002"  # scripted group (container) (typed FeaturePython)
  n = 1
  ref = Hg_element
FEATURE [App::DocumentObjectGroupPython] G4_Hg  # scripted group (container) (typed FeaturePython)
  Dunit = g/cm3
  Dvalue = 13.546
  Group = -> [Hg_element002]
  conduct = 2
  density = 1
  expand = 3
  formula = Hg
  name = G4_Hg
  specific = 4
FEATURE [App::DocumentObjectGroupPython] Tl_element002  label="Tl_element : 002"  # scripted group (container) (typed FeaturePython)
  n = 1
  ref = Tl_element
FEATURE [App::DocumentObjectGroupPython] G4_Tl  # scripted group (container) (typed FeaturePython)
  Dunit = g/cm3
  Dvalue = 11.72
  Group = -> [Tl_element002]
  conduct = 2
  density = 1
  expand = 3
  formula = Tl
  name = G4_Tl
  specific = 4
FEATURE [App::DocumentObjectGroupPython] Pb_element003  label="Pb_element : 1"  # scripted group (container) (typed FeaturePython)
  n = 1
  ref = Pb_element
FEATURE [App::DocumentObjectGroupPython] G4_Pb  # scripted group (container) (typed FeaturePython)
  Dunit = g/cm3
  Dvalue = 11.35
  Group = -> [Pb_element003]
  conduct = 2
  density = 1
  expand = 3
  formula = Pb
  name = G4_Pb
  specific = 4
FEATURE [App::DocumentObjectGroupPython] Bi_element002  label="Bi_element : 1"  # scripted group (container) (typed FeaturePython)
  n = 1
  ref = Bi_element
FEATURE [App::DocumentObjectGroupPython] G4_Bi  # scripted group (container) (typed FeaturePython)
  Dunit = g/cm3
  Dvalue = 9.747
  Group = -> [Bi_element002]
  conduct = 2
  density = 1
  expand = 3
  formula = Bi
  name = G4_Bi
  specific = 4
FEATURE [App::DocumentObjectGroupPython] Po_element001  label="Po_element : 1"  # scripted group (container) (typed FeaturePython)
  n = 1
  ref = Po_element
FEATURE [App::DocumentObjectGroupPython] G4_Po  # scripted group (container) (typed FeaturePython)
  Dunit = g/cm3
  Dvalue = 9.32
  Group = -> [Po_element001]
  conduct = 2
  density = 1
  expand = 3
  formula = Po
  name = G4_Po
  specific = 4
FEATURE [App::DocumentObjectGroupPython] At_element001  label="At_element : 1"  # scripted group (container) (typed FeaturePython)
  n = 1
  ref = At_element
FEATURE [App::DocumentObjectGroupPython] G4_At  # scripted group (container) (typed FeaturePython)
  Dunit = g/cm3
  Dvalue = 9.32
  Group = -> [At_element001]
  conduct = 2
  density = 1
  expand = 3
  formula = At
  name = G4_At
  specific = 4
FEATURE [App::DocumentObjectGroupPython] Rn_element001  label="Rn_element : 1"  # scripted group (container) (typed FeaturePython)
  n = 1
  ref = Rn_element
FEATURE [App::DocumentObjectGroupPython] G4_Rn  # scripted group (container) (typed FeaturePython)
  Dunit = g/cm3
  Dvalue = 0.00900662
  Group = -> [Rn_element001]
  conduct = 2
  density = 1
  expand = 3
  formula = Rn
  name = G4_Rn
  specific = 4
FEATURE [App::DocumentObjectGroupPython] Fr_element001  label="Fr_element : 1"  # scripted group (container) (typed FeaturePython)
  n = 1
  ref = Fr_element
FEATURE [App::DocumentObjectGroupPython] G4_Fr  # scripted group (container) (typed FeaturePython)
  Dunit = g/cm3
  Dvalue = 1
  Group = -> [Fr_element001]
  conduct = 2
  density = 1
  expand = 3
  formula = Fr
  name = G4_Fr
  specific = 4
FEATURE [App::DocumentObjectGroupPython] Ra_element001  label="Ra_element : 1"  # scripted group (container) (typed FeaturePython)
  n = 1
  ref = Ra_element
FEATURE [App::DocumentObjectGroupPython] G4_Ra  # scripted group (container) (typed FeaturePython)
  Dunit = g/cm3
  Dvalue = 5
  Group = -> [Ra_element001]
  conduct = 2
  density = 1
  expand = 3
  formula = Ra
  name = G4_Ra
  specific = 4
FEATURE [App::DocumentObjectGroupPython] Ac_element001  label="Ac_element : 1"  # scripted group (container) (typed FeaturePython)
  n = 1
  ref = Ac_element
FEATURE [App::DocumentObjectGroupPython] G4_Ac  # scripted group (container) (typed FeaturePython)
  Dunit = g/cm3
  Dvalue = 10.07
  Group = -> [Ac_element001]
  conduct = 2
  density = 1
  expand = 3
  formula = Ac
  name = G4_Ac
  specific = 4
FEATURE [App::DocumentObjectGroupPython] Th_element001  label="Th_element : 1"  # scripted group (container) (typed FeaturePython)
  n = 1
  ref = Th_element
FEATURE [App::DocumentObjectGroupPython] G4_Th  # scripted group (container) (typed FeaturePython)
  Dunit = g/cm3
  Dvalue = 11.72
  Group = -> [Th_element001]
  conduct = 2
  density = 1
  expand = 3
  formula = Th
  name = G4_Th
  specific = 4
FEATURE [App::DocumentObjectGroupPython] Pa_element001  label="Pa_element : 1"  # scripted group (container) (typed FeaturePython)
  n = 1
  ref = Pa_element
FEATURE [App::DocumentObjectGroupPython] G4_Pa  # scripted group (container) (typed FeaturePython)
  Dunit = g/cm3
  Dvalue = 15.37
  Group = -> [Pa_element001]
  conduct = 2
  density = 1
  expand = 3
  formula = Pa
  name = G4_Pa
  specific = 4
FEATURE [App::DocumentObjectGroupPython] U_element004  label="U_element : 004"  # scripted group (container) (typed FeaturePython)
  n = 1
  ref = U_element
FEATURE [App::DocumentObjectGroupPython] G4_U  # scripted group (container) (typed FeaturePython)
  Dunit = g/cm3
  Dvalue = 18.95
  Group = -> [U_element004]
  conduct = 2
  density = 1
  expand = 3
  formula = U
  name = G4_U
  specific = 4
FEATURE [App::DocumentObjectGroupPython] Np_element001  label="Np_element : 1"  # scripted group (container) (typed FeaturePython)
  n = 1
  ref = Np_element
FEATURE [App::DocumentObjectGroupPython] G4_Np  # scripted group (container) (typed FeaturePython)
  Dunit = g/cm3
  Dvalue = 20.25
  Group = -> [Np_element001]
  conduct = 2
  density = 1
  expand = 3
  formula = Np
  name = G4_Np
  specific = 4
FEATURE [App::DocumentObjectGroupPython] Pu_element002  label="Pu_element : 002"  # scripted group (container) (typed FeaturePython)
  n = 1
  ref = Pu_element
FEATURE [App::DocumentObjectGroupPython] G4_Pu  # scripted group (container) (typed FeaturePython)
  Dunit = g/cm3
  Dvalue = 19.84
  Group = -> [Pu_element002]
  conduct = 2
  density = 1
  expand = 3
  formula = Pu
  name = G4_Pu
  specific = 4
FEATURE [App::DocumentObjectGroupPython] Am_element001  label="Am_element : 1"  # scripted group (container) (typed FeaturePython)
  n = 1
  ref = Am_element
FEATURE [App::DocumentObjectGroupPython] G4_Am  # scripted group (container) (typed FeaturePython)
  Dunit = g/cm3
  Dvalue = 13.67
  Group = -> [Am_element001]
  conduct = 2
  density = 1
  expand = 3
  formula = Am
  name = G4_Am
  specific = 4
FEATURE [App::DocumentObjectGroupPython] Cm_element001  label="Cm_element : 1"  # scripted group (container) (typed FeaturePython)
  n = 1
  ref = Cm_element
FEATURE [App::DocumentObjectGroupPython] G4_Cm  # scripted group (container) (typed FeaturePython)
  Dunit = g/cm3
  Dvalue = 13.51
  Group = -> [Cm_element001]
  conduct = 2
  density = 1
  expand = 3
  formula = Cm
  name = G4_Cm
  specific = 4
FEATURE [App::DocumentObjectGroupPython] Bk_element001  label="Bk_element : 1"  # scripted group (container) (typed FeaturePython)
  n = 1
  ref = Bk_element
FEATURE [App::DocumentObjectGroupPython] G4_Bk  # scripted group (container) (typed FeaturePython)
  Dunit = g/cm3
  Dvalue = 14
  Group = -> [Bk_element001]
  conduct = 2
  density = 1
  expand = 3
  formula = Bk
  name = G4_Bk
  specific = 4
FEATURE [App::DocumentObjectGroupPython] Cf_element001  label="Cf_element : 1"  # scripted group (container) (typed FeaturePython)
  n = 1
  ref = Cf_element
FEATURE [App::DocumentObjectGroupPython] G4_Cf  # scripted group (container) (typed FeaturePython)
  Dunit = g/cm3
  Dvalue = 10
  Group = -> [Cf_element001]
  conduct = 2
  density = 1
  expand = 3
  formula = Cf
  name = G4_Cf
  specific = 4
FEATURE [App::DocumentObjectGroupPython] Element  # scripted group (container) (typed FeaturePython)
  Group = -> [G4_H,G4_He,G4_Li,G4_Be,G4_B,G4_C,G4_N,G4_O,G4_F,G4_Ne,G4_Na,G4_Mg,G4_Al,G4_Si,G4_P,G4_S,G4_Cl,G4_Ar,G4_K,G4_Ca,G4_Sc,G4_Ti,G4_V,G4_Cr,G4_Mn,G4_Fe,G4_Co,G4_Ni,G4_Cu,G4_Zn,G4_Ga,G4_Ge,G4_As,G4_Se,G4_Br,G4_Kr,G4_Rb,G4_Sr,G4_Y,G4_Zr,G4_Nb,G4_Mo,G4_Tc,G4_Ru,G4_Rh,G4_Pd,G4_Ag,G4_Cd,G4_In,G4_Sn,G4_Sb,G4_Te,G4_I,G4_Xe,G4_Cs,G4_Ba,G4_La,G4_Ce,G4_Pr,G4_Nd,G4_Pm,G4_Sm,G4_Eu,G4_Gd,G4_Tb,G4_Dy,G4_Ho,G4_Er,+30 more]
FEATURE [App::DocumentObjectGroupPython] H_element114  label="H_element : 063"  # scripted group (container) (typed FeaturePython)
  n = 2
  ref = H_element
FEATURE [App::DocumentObjectGroupPython] G4_lH2  # scripted group (container) (typed FeaturePython)
  Dunit = g/cm3
  Dvalue = 0.0708
  Group = -> [H_element114]
  conduct = 2
  density = 1
  expand = 3
  formula = G4_lH2
  name = G4_lH2
  specific = 4
FEATURE [App::DocumentObjectGroupPython] N_element049  label="N_element : 022"  # scripted group (container) (typed FeaturePython)
  n = 2
  ref = N_element
FEATURE [App::DocumentObjectGroupPython] G4_lN2  # scripted group (container) (typed FeaturePython)
  Dunit = g/cm3
  Dvalue = 0.807
  Group = -> [N_element049]
  conduct = 2
  density = 1
  expand = 3
  formula = G4_lN2
  name = G4_lN2
  specific = 4
FEATURE [App::DocumentObjectGroupPython] O_element106  label="O_element : 060"  # scripted group (container) (typed FeaturePython)
  n = 2
  ref = O_element
FEATURE [App::DocumentObjectGroupPython] G4_lO2  # scripted group (container) (typed FeaturePython)
  Dunit = g/cm3
  Dvalue = 1.141
  Group = -> [O_element106]
  conduct = 2
  density = 1
  expand = 3
  formula = G4_lO2
  name = G4_lO2
  specific = 4
FEATURE [App::DocumentObjectGroupPython] Ar  label="Ar : 1"  # scripted group (container) (typed FeaturePython)
  n = 1
  ref = Ar
FEATURE [App::DocumentObjectGroupPython] G4_lAr  # scripted group (container) (typed FeaturePython)
  Dunit = g/cm3
  Dvalue = 1.396
  Group = -> [Ar]
  conduct = 2
  density = 1
  expand = 3
  formula = G4_lAr
  name = G4_lAr
  specific = 4
FEATURE [App::DocumentObjectGroupPython] Br  label="Br : 1"  # scripted group (container) (typed FeaturePython)
  n = 1
  ref = Br
FEATURE [App::DocumentObjectGroupPython] G4_lBr  # scripted group (container) (typed FeaturePython)
  Dunit = g/cm3
  Dvalue = 3.1028
  Group = -> [Br]
  conduct = 2
  density = 1
  expand = 3
  formula = G4_lBr
  name = G4_lBr
  specific = 4
FEATURE [App::DocumentObjectGroupPython] Kr  label="Kr : 1"  # scripted group (container) (typed FeaturePython)
  n = 1
  ref = Kr
FEATURE [App::DocumentObjectGroupPython] G4_lKr  # scripted group (container) (typed FeaturePython)
  Dunit = g/cm3
  Dvalue = 2.418
  Group = -> [Kr]
  conduct = 2
  density = 1
  expand = 3
  formula = G4_lKr
  name = G4_lKr
  specific = 4
FEATURE [App::DocumentObjectGroupPython] Xe  label="Xe : 1"  # scripted group (container) (typed FeaturePython)
  n = 1
  ref = Xe
FEATURE [App::DocumentObjectGroupPython] G4_lXe  # scripted group (container) (typed FeaturePython)
  Dunit = g/cm3
  Dvalue = 2.953
  Group = -> [Xe]
  conduct = 2
  density = 1
  expand = 3
  formula = G4_lXe
  name = G4_lXe
  specific = 4
FEATURE [App::DocumentObjectGroupPython] O_element107  label="O_element : 061"  # scripted group (container) (typed FeaturePython)
  n = 4
  ref = O_element
FEATURE [App::DocumentObjectGroupPython] Pb_element004  label="Pb_element : 002"  # scripted group (container) (typed FeaturePython)
  n = 1
  ref = Pb_element
FEATURE [App::DocumentObjectGroupPython] W_element005  label="W_element : 005"  # scripted group (container) (typed FeaturePython)
  n = 1
  ref = W_element
FEATURE [App::DocumentObjectGroupPython] G4_PbWO4  # scripted group (container) (typed FeaturePython)
  Dunit = g/cm3
  Dvalue = 8.28
  Group = -> [O_element107,Pb_element004,W_element005]
  conduct = 2
  density = 1
  expand = 3
  formula = G4_PbWO4
  name = G4_PbWO4
  specific = 4
FEATURE [App::DocumentObjectGroupPython] alactic  label="alactic : 1"  # scripted group (container) (typed FeaturePython)
  n = 1
  ref = alactic
FEATURE [App::DocumentObjectGroupPython] G4_Galactic  # scripted group (container) (typed FeaturePython)
  Dunit = g/cm3
  Dvalue = 0
  Group = -> [alactic]
  conduct = 2
  density = 1
  expand = 3
  formula = G4_Galactic
  name = G4_Galactic
  specific = 4
FEATURE [App::DocumentObjectGroupPython] RAPHITE_POROUS  label="RAPHITE_POROUS : 1"  # scripted group (container) (typed FeaturePython)
  n = 1
  ref = RAPHITE_POROUS
FEATURE [App::DocumentObjectGroupPython] G4_GRAPHITE_POROUS  # scripted group (container) (typed FeaturePython)
  Dunit = g/cm3
  Dvalue = 1.7
  Group = -> [RAPHITE_POROUS]
  conduct = 2
  density = 1
  expand = 3
  formula = G4_GRAPHITE_POROUS
  name = G4_GRAPHITE_POROUS
  specific = 4
FEATURE [App::DocumentObjectGroupPython] H_element115  label="H_element : 0.150"  # scripted group (container) (typed FeaturePython)
  n = 0.080538
FEATURE [App::DocumentObjectGroupPython] C_element125  label="C_element : 0.600"  # scripted group (container) (typed FeaturePython)
  n = 0.599848
FEATURE [App::DocumentObjectGroupPython] O_element108  label="O_element : 0.320"  # scripted group (container) (typed FeaturePython)
  n = 0.319614
FEATURE [App::DocumentObjectGroupPython] G4_LUCITE  # scripted group (container) (typed FeaturePython)
  Dunit = g/cm3
  Dvalue = 1.19
  Group = -> [H_element115,C_element125,O_element108]
  conduct = 2
  density = 1
  expand = 3
  formula = G4_LUCITE
  name = G4_LUCITE
  specific = 4
FEATURE [App::DocumentObjectGroupPython] Cu_element002  label="Cu_element : 62"  # scripted group (container) (typed FeaturePython)
  n = 62
  ref = Cu_element
FEATURE [App::DocumentObjectGroupPython] Zn_element002  label="Zn_element : 35"  # scripted group (container) (typed FeaturePython)
  n = 35
  ref = Zn_element
FEATURE [App::DocumentObjectGroupPython] Pb_element005  label="Pb_element : 3"  # scripted group (container) (typed FeaturePython)
  n = 3
  ref = Pb_element
FEATURE [App::DocumentObjectGroupPython] G4_BRASS  # scripted group (container) (typed FeaturePython)
  Dunit = g/cm3
  Dvalue = 8.52
  Group = -> [Cu_element002,Zn_element002,Pb_element005]
  conduct = 2
  density = 1
  expand = 3
  formula = G4_BRASS
  name = G4_BRASS
  specific = 4
FEATURE [App::DocumentObjectGroupPython] Cu_element003  label="Cu_element : 89"  # scripted group (container) (typed FeaturePython)
  n = 89
  ref = Cu_element
FEATURE [App::DocumentObjectGroupPython] Zn_element003  label="Zn_element : 9"  # scripted group (container) (typed FeaturePython)
  n = 9
  ref = Zn_element
FEATURE [App::DocumentObjectGroupPython] Pb_element006  label="Pb_element : 2"  # scripted group (container) (typed FeaturePython)
  n = 2
  ref = Pb_element
FEATURE [App::DocumentObjectGroupPython] G4_BRONZE  # scripted group (container) (typed FeaturePython)
  Dunit = g/cm3
  Dvalue = 8.82
  Group = -> [Cu_element003,Zn_element003,Pb_element006]
  conduct = 2
  density = 1
  expand = 3
  formula = G4_BRONZE
  name = G4_BRONZE
  specific = 4
FEATURE [App::DocumentObjectGroupPython] Fe_element008  label="Fe_element : 74"  # scripted group (container) (typed FeaturePython)
  n = 74
  ref = Fe_element
FEATURE [App::DocumentObjectGroupPython] Cr_element002  label="Cr_element : 18"  # scripted group (container) (typed FeaturePython)
  n = 18
  ref = Cr_element
FEATURE [App::DocumentObjectGroupPython] Ni_element002  label="Ni_element : 8"  # scripted group (container) (typed FeaturePython)
  n = 8
  ref = Ni_element
FEATURE [App::DocumentObjectGroupPython] G4_STAINLESS_STEEL  label="G4_STAINLESS-STEEL"  # scripted group (container) (typed FeaturePython)
  Dunit = g/cm3
  Dvalue = 8
  Group = -> [Fe_element008,Cr_element002,Ni_element002]
  conduct = 2
  density = 1
  expand = 3
  formula = G4_STAINLESS-STEEL
  name = G4_STAINLESS-STEEL
  specific = 4
FEATURE [App::DocumentObjectGroupPython] H_element116  label="H_element : 064"  # scripted group (container) (typed FeaturePython)
  n = 18
  ref = H_element
FEATURE [App::DocumentObjectGroupPython] C_element126  label="C_element : 071"  # scripted group (container) (typed FeaturePython)
  n = 12
  ref = C_element
FEATURE [App::DocumentObjectGroupPython] O_element109  label="O_element : 062"  # scripted group (container) (typed FeaturePython)
  n = 7
  ref = O_element
FEATURE [App::DocumentObjectGroupPython] G4_CR39  # scripted group (container) (typed FeaturePython)
  Dunit = g/cm3
  Dvalue = 1.32
  Group = -> [H_element116,C_element126,O_element109]
  conduct = 2
  density = 1
  expand = 3
  formula = G4_CR39
  name = G4_CR39
  specific = 4
FEATURE [App::DocumentObjectGroupPython] H_element117  label="H_element : 38"  # scripted group (container) (typed FeaturePython)
  n = 38
  ref = H_element
FEATURE [App::DocumentObjectGroupPython] C_element127  label="C_element : 072"  # scripted group (container) (typed FeaturePython)
  n = 18
  ref = C_element
FEATURE [App::DocumentObjectGroupPython] O_element110  label="O_element : 063"  # scripted group (container) (typed FeaturePython)
  n = 1
  ref = O_element
FEATURE [App::DocumentObjectGroupPython] G4_OCTADECANOL  # scripted group (container) (typed FeaturePython)
  Dunit = g/cm3
  Dvalue = 0.812
  Group = -> [H_element117,C_element127,O_element110]
  conduct = 2
  density = 1
  expand = 3
  formula = G4_OCTADECANOL
  name = G4_OCTADECANOL
  specific = 4
FEATURE [App::DocumentObjectGroupPython] HEP  # scripted group (container) (typed FeaturePython)
  Group = -> [G4_lH2,G4_lN2,G4_lO2,G4_lAr,G4_lBr,G4_lKr,G4_lXe,G4_PbWO4,G4_Galactic,G4_GRAPHITE_POROUS,G4_LUCITE,G4_BRASS,G4_BRONZE,G4_STAINLESS_STEEL,G4_CR39,G4_OCTADECANOL]
FEATURE [App::DocumentObjectGroupPython] C_element128  label="C_element : 073"  # scripted group (container) (typed FeaturePython)
  n = 14
  ref = C_element
FEATURE [App::DocumentObjectGroupPython] H_element118  label="H_element : 065"  # scripted group (container) (typed FeaturePython)
  n = 10
  ref = H_element
FEATURE [App::DocumentObjectGroupPython] O_element111  label="O_element : 064"  # scripted group (container) (typed FeaturePython)
  n = 2
  ref = O_element
FEATURE [App::DocumentObjectGroupPython] N_element050  label="N_element : 023"  # scripted group (container) (typed FeaturePython)
  n = 2
  ref = N_element
FEATURE [App::DocumentObjectGroupPython] G4_KEVLAR  # scripted group (container) (typed FeaturePython)
  Dunit = g/cm3
  Dvalue = 1.44
  Group = -> [C_element128,H_element118,O_element111,N_element050]
  conduct = 2
  density = 1
  expand = 3
  formula = G4_KEVLAR
  name = G4_KEVLAR
  specific = 4
FEATURE [App::DocumentObjectGroupPython] C_element129  label="C_element : 074"  # scripted group (container) (typed FeaturePython)
  n = 10
  ref = C_element
FEATURE [App::DocumentObjectGroupPython] H_element119  label="H_element : 066"  # scripted group (container) (typed FeaturePython)
  n = 8
  ref = H_element
FEATURE [App::DocumentObjectGroupPython] O_element112  label="O_element : 065"  # scripted group (container) (typed FeaturePython)
  n = 4
  ref = O_element
FEATURE [App::DocumentObjectGroupPython] G4_DACRON  # scripted group (container) (typed FeaturePython)
  Dunit = g/cm3
  Dvalue = 1.4
  Group = -> [C_element129,H_element119,O_element112]
  conduct = 2
  density = 1
  expand = 3
  formula = G4_DACRON
  name = G4_DACRON
  specific = 4
FEATURE [App::DocumentObjectGroupPython] C_element130  label="C_element : 075"  # scripted group (container) (typed FeaturePython)
  n = 4
  ref = C_element
FEATURE [App::DocumentObjectGroupPython] H_element120  label="H_element : 067"  # scripted group (container) (typed FeaturePython)
  n = 5
  ref = H_element
FEATURE [App::DocumentObjectGroupPython] Cl_element030  label="Cl_element : 016"  # scripted group (container) (typed FeaturePython)
  n = 1
  ref = Cl_element
FEATURE [App::DocumentObjectGroupPython] G4_NEOPRENE  # scripted group (container) (typed FeaturePython)
  Dunit = g/cm3
  Dvalue = 1.23
  Group = -> [C_element130,H_element120,Cl_element030]
  conduct = 2
  density = 1
  expand = 3
  formula = G4_NEOPRENE
  name = G4_NEOPRENE
  specific = 4
FEATURE [App::DocumentObjectGroupPython] Space  # scripted group (container) (typed FeaturePython)
  Group = -> [G4_KEVLAR,G4_DACRON,G4_NEOPRENE]
FEATURE [App::DocumentObjectGroupPython] H_element121  label="H_element : 068"  # scripted group (container) (typed FeaturePython)
  n = 5
  ref = H_element
FEATURE [App::DocumentObjectGroupPython] C_element131  label="C_element : 076"  # scripted group (container) (typed FeaturePython)
  n = 4
  ref = C_element
FEATURE [App::DocumentObjectGroupPython] N_element051  label="N_element : 3"  # scripted group (container) (typed FeaturePython)
  n = 3
  ref = N_element
FEATURE [App::DocumentObjectGroupPython] O_element113  label="O_element : 066"  # scripted group (container) (typed FeaturePython)
  n = 1
  ref = O_element
FEATURE [App::DocumentObjectGroupPython] G4_CYTOSINE  # scripted group (container) (typed FeaturePython)
  Dunit = g/cm3
  Dvalue = 1.55
  Group = -> [H_element121,C_element131,N_element051,O_element113]
  conduct = 2
  density = 1
  expand = 3
  formula = G4_CYTOSINE
  name = G4_CYTOSINE
  specific = 4
FEATURE [App::DocumentObjectGroupPython] H_element122  label="H_element : 069"  # scripted group (container) (typed FeaturePython)
  n = 6
  ref = H_element
FEATURE [App::DocumentObjectGroupPython] C_element132  label="C_element : 077"  # scripted group (container) (typed FeaturePython)
  n = 5
  ref = C_element
FEATURE [App::DocumentObjectGroupPython] N_element052  label="N_element : 024"  # scripted group (container) (typed FeaturePython)
  n = 2
  ref = N_element
FEATURE [App::DocumentObjectGroupPython] O_element114  label="O_element : 067"  # scripted group (container) (typed FeaturePython)
  n = 2
  ref = O_element
FEATURE [App::DocumentObjectGroupPython] G4_THYMINE  # scripted group (container) (typed FeaturePython)
  Dunit = g/cm3
  Dvalue = 1.23
  Group = -> [H_element122,C_element132,N_element052,O_element114]
  conduct = 2
  density = 1
  expand = 3
  formula = G4_THYMINE
  name = G4_THYMINE
  specific = 4
FEATURE [App::DocumentObjectGroupPython] H_element123  label="H_element : 070"  # scripted group (container) (typed FeaturePython)
  n = 4
  ref = H_element
FEATURE [App::DocumentObjectGroupPython] C_element133  label="C_element : 078"  # scripted group (container) (typed FeaturePython)
  n = 4
  ref = C_element
FEATURE [App::DocumentObjectGroupPython] N_element053  label="N_element : 025"  # scripted group (container) (typed FeaturePython)
  n = 2
  ref = N_element
FEATURE [App::DocumentObjectGroupPython] O_element115  label="O_element : 068"  # scripted group (container) (typed FeaturePython)
  n = 2
  ref = O_element
FEATURE [App::DocumentObjectGroupPython] G4_URACIL  # scripted group (container) (typed FeaturePython)
  Dunit = g/cm3
  Dvalue = 1.32
  Group = -> [H_element123,C_element133,N_element053,O_element115]
  conduct = 2
  density = 1
  expand = 3
  formula = G4_URACIL
  name = G4_URACIL
  specific = 4
FEATURE [App::DocumentObjectGroupPython] H_element124  label="H_element : 071"  # scripted group (container) (typed FeaturePython)
  n = 4
  ref = H_element
FEATURE [App::DocumentObjectGroupPython] C_element134  label="C_element : 079"  # scripted group (container) (typed FeaturePython)
  n = 5
  ref = C_element
FEATURE [App::DocumentObjectGroupPython] N_element054  label="N_element : 026"  # scripted group (container) (typed FeaturePython)
  n = 5
  ref = N_element
FEATURE [App::DocumentObjectGroupPython] G4_DNA_ADENINE  # scripted group (container) (typed FeaturePython)
  Dunit = g/cm3
  Dvalue = 1
  Group = -> [H_element124,C_element134,N_element054]
  conduct = 2
  density = 1
  expand = 3
  formula = G4_DNA_ADENINE
  name = G4_DNA_ADENINE
  specific = 4
FEATURE [App::DocumentObjectGroupPython] H_element125  label="H_element : 072"  # scripted group (container) (typed FeaturePython)
  n = 4
  ref = H_element
FEATURE [App::DocumentObjectGroupPython] C_element135  label="C_element : 080"  # scripted group (container) (typed FeaturePython)
  n = 5
  ref = C_element
FEATURE [App::DocumentObjectGroupPython] N_element055  label="N_element : 027"  # scripted group (container) (typed FeaturePython)
  n = 5
  ref = N_element
FEATURE [App::DocumentObjectGroupPython] O_element116  label="O_element : 069"  # scripted group (container) (typed FeaturePython)
  n = 1
  ref = O_element
FEATURE [App::DocumentObjectGroupPython] G4_DNA_GUANINE  # scripted group (container) (typed FeaturePython)
  Dunit = g/cm3
  Dvalue = 1
  Group = -> [H_element125,C_element135,N_element055,O_element116]
  conduct = 2
  density = 1
  expand = 3
  formula = G4_DNA_GUANINE
  name = G4_DNA_GUANINE
  specific = 4
FEATURE [App::DocumentObjectGroupPython] H_element126  label="H_element : 073"  # scripted group (container) (typed FeaturePython)
  n = 4
  ref = H_element
FEATURE [App::DocumentObjectGroupPython] C_element136  label="C_element : 081"  # scripted group (container) (typed FeaturePython)
  n = 4
  ref = C_element
FEATURE [App::DocumentObjectGroupPython] N_element056  label="N_element : 028"  # scripted group (container) (typed FeaturePython)
  n = 3
  ref = N_element
FEATURE [App::DocumentObjectGroupPython] O_element117  label="O_element : 070"  # scripted group (container) (typed FeaturePython)
  n = 1
  ref = O_element
FEATURE [App::DocumentObjectGroupPython] G4_DNA_CYTOSINE  # scripted group (container) (typed FeaturePython)
  Dunit = g/cm3
  Dvalue = 1
  Group = -> [H_element126,C_element136,N_element056,O_element117]
  conduct = 2
  density = 1
  expand = 3
  formula = G4_DNA_CYTOSINE
  name = G4_DNA_CYTOSINE
  specific = 4
FEATURE [App::DocumentObjectGroupPython] H_element127  label="H_element : 074"  # scripted group (container) (typed FeaturePython)
  n = 5
  ref = H_element
FEATURE [App::DocumentObjectGroupPython] C_element137  label="C_element : 082"  # scripted group (container) (typed FeaturePython)
  n = 5
  ref = C_element
FEATURE [App::DocumentObjectGroupPython] N_element057  label="N_element : 029"  # scripted group (container) (typed FeaturePython)
  n = 2
  ref = N_element
FEATURE [App::DocumentObjectGroupPython] O_element118  label="O_element : 071"  # scripted group (container) (typed FeaturePython)
  n = 2
  ref = O_element
FEATURE [App::DocumentObjectGroupPython] G4_DNA_THYMINE  # scripted group (container) (typed FeaturePython)
  Dunit = g/cm3
  Dvalue = 1
  Group = -> [H_element127,C_element137,N_element057,O_element118]
  conduct = 2
  density = 1
  expand = 3
  formula = G4_DNA_THYMINE
  name = G4_DNA_THYMINE
  specific = 4
FEATURE [App::DocumentObjectGroupPython] H_element128  label="H_element : 075"  # scripted group (container) (typed FeaturePython)
  n = 3
  ref = H_element
FEATURE [App::DocumentObjectGroupPython] C_element138  label="C_element : 083"  # scripted group (container) (typed FeaturePython)
  n = 4
  ref = C_element
FEATURE [App::DocumentObjectGroupPython] N_element058  label="N_element : 030"  # scripted group (container) (typed FeaturePython)
  n = 2
  ref = N_element
FEATURE [App::DocumentObjectGroupPython] O_element119  label="O_element : 072"  # scripted group (container) (typed FeaturePython)
  n = 2
  ref = O_element
FEATURE [App::DocumentObjectGroupPython] G4_DNA_URACIL  # scripted group (container) (typed FeaturePython)
  Dunit = g/cm3
  Dvalue = 1
  Group = -> [H_element128,C_element138,N_element058,O_element119]
  conduct = 2
  density = 1
  expand = 3
  formula = G4_DNA_URACIL
  name = G4_DNA_URACIL
  specific = 4
FEATURE [App::DocumentObjectGroupPython] H_element129  label="H_element : 076"  # scripted group (container) (typed FeaturePython)
  n = 10
  ref = H_element
FEATURE [App::DocumentObjectGroupPython] C_element139  label="C_element : 084"  # scripted group (container) (typed FeaturePython)
  n = 10
  ref = C_element
FEATURE [App::DocumentObjectGroupPython] N_element059  label="N_element : 031"  # scripted group (container) (typed FeaturePython)
  n = 5
  ref = N_element
FEATURE [App::DocumentObjectGroupPython] O_element120  label="O_element : 073"  # scripted group (container) (typed FeaturePython)
  n = 4
  ref = O_element
FEATURE [App::DocumentObjectGroupPython] G4_DNA_ADENOSINE  # scripted group (container) (typed FeaturePython)
  Dunit = g/cm3
  Dvalue = 1
  Group = -> [H_element129,C_element139,N_element059,O_element120]
  conduct = 2
  density = 1
  expand = 3
  formula = G4_DNA_ADENOSINE
  name = G4_DNA_ADENOSINE
  specific = 4
FEATURE [App::DocumentObjectGroupPython] H_element130  label="H_element : 077"  # scripted group (container) (typed FeaturePython)
  n = 10
  ref = H_element
FEATURE [App::DocumentObjectGroupPython] C_element140  label="C_element : 085"  # scripted group (container) (typed FeaturePython)
  n = 10
  ref = C_element
FEATURE [App::DocumentObjectGroupPython] N_element060  label="N_element : 032"  # scripted group (container) (typed FeaturePython)
  n = 5
  ref = N_element
FEATURE [App::DocumentObjectGroupPython] O_element121  label="O_element : 074"  # scripted group (container) (typed FeaturePython)
  n = 5
  ref = O_element
FEATURE [App::DocumentObjectGroupPython] G4_DNA_GUANOSINE  # scripted group (container) (typed FeaturePython)
  Dunit = g/cm3
  Dvalue = 1
  Group = -> [H_element130,C_element140,N_element060,O_element121]
  conduct = 2
  density = 1
  expand = 3
  formula = G4_DNA_GUANOSINE
  name = G4_DNA_GUANOSINE
  specific = 4
FEATURE [App::DocumentObjectGroupPython] H_element131  label="H_element : 078"  # scripted group (container) (typed FeaturePython)
  n = 10
  ref = H_element
FEATURE [App::DocumentObjectGroupPython] C_element141  label="C_element : 086"  # scripted group (container) (typed FeaturePython)
  n = 9
  ref = C_element
FEATURE [App::DocumentObjectGroupPython] N_element061  label="N_element : 033"  # scripted group (container) (typed FeaturePython)
  n = 3
  ref = N_element
FEATURE [App::DocumentObjectGroupPython] O_element122  label="O_element : 075"  # scripted group (container) (typed FeaturePython)
  n = 5
  ref = O_element
FEATURE [App::DocumentObjectGroupPython] G4_DNA_CYTIDINE  # scripted group (container) (typed FeaturePython)
  Dunit = g/cm3
  Dvalue = 1
  Group = -> [H_element131,C_element141,N_element061,O_element122]
  conduct = 2
  density = 1
  expand = 3
  formula = G4_DNA_CYTIDINE
  name = G4_DNA_CYTIDINE
  specific = 4
FEATURE [App::DocumentObjectGroupPython] H_element132  label="H_element : 079"  # scripted group (container) (typed FeaturePython)
  n = 9
  ref = H_element
FEATURE [App::DocumentObjectGroupPython] C_element142  label="C_element : 087"  # scripted group (container) (typed FeaturePython)
  n = 9
  ref = C_element
FEATURE [App::DocumentObjectGroupPython] N_element062  label="N_element : 034"  # scripted group (container) (typed FeaturePython)
  n = 2
  ref = N_element
FEATURE [App::DocumentObjectGroupPython] O_element123  label="O_element : 076"  # scripted group (container) (typed FeaturePython)
  n = 6
  ref = O_element
FEATURE [App::DocumentObjectGroupPython] G4_DNA_URIDINE  # scripted group (container) (typed FeaturePython)
  Dunit = g/cm3
  Dvalue = 1
  Group = -> [H_element132,C_element142,N_element062,O_element123]
  conduct = 2
  density = 1
  expand = 3
  formula = G4_DNA_URIDINE
  name = G4_DNA_URIDINE
  specific = 4
FEATURE [App::DocumentObjectGroupPython] H_element133  label="H_element : 080"  # scripted group (container) (typed FeaturePython)
  n = 11
  ref = H_element
FEATURE [App::DocumentObjectGroupPython] C_element143  label="C_element : 088"  # scripted group (container) (typed FeaturePython)
  n = 10
  ref = C_element
FEATURE [App::DocumentObjectGroupPython] N_element063  label="N_element : 035"  # scripted group (container) (typed FeaturePython)
  n = 2
  ref = N_element
FEATURE [App::DocumentObjectGroupPython] O_element124  label="O_element : 077"  # scripted group (container) (typed FeaturePython)
  n = 6
  ref = O_element
FEATURE [App::DocumentObjectGroupPython] G4_DNA_METHYLURIDINE  # scripted group (container) (typed FeaturePython)
  Dunit = g/cm3
  Dvalue = 1
  Group = -> [H_element133,C_element143,N_element063,O_element124]
  conduct = 2
  density = 1
  expand = 3
  formula = G4_DNA_METHYLURIDINE
  name = G4_DNA_METHYLURIDINE
  specific = 4
FEATURE [App::DocumentObjectGroupPython] P_element014  label="P_element : 003"  # scripted group (container) (typed FeaturePython)
  n = 1
  ref = P_element
FEATURE [App::DocumentObjectGroupPython] O_element125  label="O_element : 078"  # scripted group (container) (typed FeaturePython)
  n = 3
  ref = O_element
FEATURE [App::DocumentObjectGroupPython] G4_DNA_MONOPHOSPHATE  # scripted group (container) (typed FeaturePython)
  Dunit = g/cm3
  Dvalue = 1
  Group = -> [P_element014,O_element125]
  conduct = 2
  density = 1
  expand = 3
  formula = G4_DNA_MONOPHOSPHATE
  name = G4_DNA_MONOPHOSPHATE
  specific = 4
FEATURE [App::DocumentObjectGroupPython] H_element134  label="H_element : 081"  # scripted group (container) (typed FeaturePython)
  n = 10
  ref = H_element
FEATURE [App::DocumentObjectGroupPython] C_element144  label="C_element : 089"  # scripted group (container) (typed FeaturePython)
  n = 10
  ref = C_element
FEATURE [App::DocumentObjectGroupPython] N_element064  label="N_element : 036"  # scripted group (container) (typed FeaturePython)
  n = 5
  ref = N_element
FEATURE [App::DocumentObjectGroupPython] O_element126  label="O_element : 079"  # scripted group (container) (typed FeaturePython)
  n = 7
  ref = O_element
FEATURE [App::DocumentObjectGroupPython] P_element015  label="P_element : 004"  # scripted group (container) (typed FeaturePython)
  n = 1
  ref = P_element
FEATURE [App::DocumentObjectGroupPython] G4_DNA_A  # scripted group (container) (typed FeaturePython)
  Dunit = g/cm3
  Dvalue = 1
  Group = -> [H_element134,C_element144,N_element064,O_element126,P_element015]
  conduct = 2
  density = 1
  expand = 3
  formula = G4_DNA_A
  name = G4_DNA_A
  specific = 4
FEATURE [App::DocumentObjectGroupPython] H_element135  label="H_element : 082"  # scripted group (container) (typed FeaturePython)
  n = 10
  ref = H_element
FEATURE [App::DocumentObjectGroupPython] C_element145  label="C_element : 090"  # scripted group (container) (typed FeaturePython)
  n = 10
  ref = C_element
FEATURE [App::DocumentObjectGroupPython] N_element065  label="N_element : 037"  # scripted group (container) (typed FeaturePython)
  n = 5
  ref = N_element
FEATURE [App::DocumentObjectGroupPython] O_element127  label="O_element : 8"  # scripted group (container) (typed FeaturePython)
  n = 8
  ref = O_element
FEATURE [App::DocumentObjectGroupPython] P_element016  label="P_element : 005"  # scripted group (container) (typed FeaturePython)
  n = 1
  ref = P_element
FEATURE [App::DocumentObjectGroupPython] G4_DNA_G  # scripted group (container) (typed FeaturePython)
  Dunit = g/cm3
  Dvalue = 1
  Group = -> [H_element135,C_element145,N_element065,O_element127,P_element016]
  conduct = 2
  density = 1
  expand = 3
  formula = G4_DNA_G
  name = G4_DNA_G
  specific = 4
FEATURE [App::DocumentObjectGroupPython] H_element136  label="H_element : 083"  # scripted group (container) (typed FeaturePython)
  n = 10
  ref = H_element
FEATURE [App::DocumentObjectGroupPython] C_element146  label="C_element : 091"  # scripted group (container) (typed FeaturePython)
  n = 9
  ref = C_element
FEATURE [App::DocumentObjectGroupPython] N_element066  label="N_element : 038"  # scripted group (container) (typed FeaturePython)
  n = 3
  ref = N_element
FEATURE [App::DocumentObjectGroupPython] O_element128  label="O_element : 080"  # scripted group (container) (typed FeaturePython)
  n = 8
  ref = O_element
FEATURE [App::DocumentObjectGroupPython] P_element017  label="P_element : 006"  # scripted group (container) (typed FeaturePython)
  n = 1
  ref = P_element
FEATURE [App::DocumentObjectGroupPython] G4_DNA_C  # scripted group (container) (typed FeaturePython)
  Dunit = g/cm3
  Dvalue = 1
  Group = -> [H_element136,C_element146,N_element066,O_element128,P_element017]
  conduct = 2
  density = 1
  expand = 3
  formula = G4_DNA_C
  name = G4_DNA_C
  specific = 4
FEATURE [App::DocumentObjectGroupPython] H_element137  label="H_element : 084"  # scripted group (container) (typed FeaturePython)
  n = 9
  ref = H_element
FEATURE [App::DocumentObjectGroupPython] C_element147  label="C_element : 092"  # scripted group (container) (typed FeaturePython)
  n = 9
  ref = C_element
FEATURE [App::DocumentObjectGroupPython] N_element067  label="N_element : 039"  # scripted group (container) (typed FeaturePython)
  n = 2
  ref = N_element
FEATURE [App::DocumentObjectGroupPython] O_element129  label="O_element : 9"  # scripted group (container) (typed FeaturePython)
  n = 9
  ref = O_element
FEATURE [App::DocumentObjectGroupPython] P_element018  label="P_element : 007"  # scripted group (container) (typed FeaturePython)
  n = 1
  ref = P_element
FEATURE [App::DocumentObjectGroupPython] G4_DNA_U  # scripted group (container) (typed FeaturePython)
  Dunit = g/cm3
  Dvalue = 1
  Group = -> [H_element137,C_element147,N_element067,O_element129,P_element018]
  conduct = 2
  density = 1
  expand = 3
  formula = G4_DNA_U
  name = G4_DNA_U
  specific = 4
FEATURE [App::DocumentObjectGroupPython] H_element138  label="H_element : 085"  # scripted group (container) (typed FeaturePython)
  n = 11
  ref = H_element
FEATURE [App::DocumentObjectGroupPython] C_element148  label="C_element : 093"  # scripted group (container) (typed FeaturePython)
  n = 10
  ref = C_element
FEATURE [App::DocumentObjectGroupPython] N_element068  label="N_element : 040"  # scripted group (container) (typed FeaturePython)
  n = 2
  ref = N_element
FEATURE [App::DocumentObjectGroupPython] O_element130  label="O_element : 081"  # scripted group (container) (typed FeaturePython)
  n = 9
  ref = O_element
FEATURE [App::DocumentObjectGroupPython] P_element019  label="P_element : 008"  # scripted group (container) (typed FeaturePython)
  n = 1
  ref = P_element
FEATURE [App::DocumentObjectGroupPython] G4_DNA_MU  # scripted group (container) (typed FeaturePython)
  Dunit = g/cm3
  Dvalue = 1
  Group = -> [H_element138,C_element148,N_element068,O_element130,P_element019]
  conduct = 2
  density = 1
  expand = 3
  formula = G4_DNA_MU
  name = G4_DNA_MU
  specific = 4
FEATURE [App::DocumentObjectGroupPython] BioChemical  # scripted group (container) (typed FeaturePython)
  Group = -> [G4_CYTOSINE,G4_THYMINE,G4_URACIL,G4_DNA_ADENINE,G4_DNA_GUANINE,G4_DNA_CYTOSINE,G4_DNA_THYMINE,G4_DNA_URACIL,G4_DNA_ADENOSINE,G4_DNA_GUANOSINE,G4_DNA_CYTIDINE,G4_DNA_URIDINE,G4_DNA_METHYLURIDINE,G4_DNA_MONOPHOSPHATE,G4_DNA_A,G4_DNA_G,G4_DNA_C,G4_DNA_U,G4_DNA_MU]
FEATURE [App::DocumentObjectGroupPython] G4Materials  # scripted group (container) (typed FeaturePython)
  Group = -> [NIST,Element,HEP,Space,BioChemical]
  version = 1
FEATURE [App::DocumentObjectGroupPython] Geant4  # scripted group (container) (typed FeaturePython)
  Group = -> [G4Isotopes,G4Elements,G4Materials]
FEATURE [App::DocumentObjectGroupPython] Materials  # scripted group (container) (typed FeaturePython)
  Group = -> [Geant4]
FEATURE [Part::FeaturePython] GDMLBox_WorldBox  # WARN: FeaturePython — macro-defined, semantics opaque (R4)
  lunit = 2
  material = 5
  x = 273
  y = 273
  z = 130
FEATURE [Part::FeaturePython] GDMLBox_Box  # WARN: FeaturePython — macro-defined, semantics opaque (R4)
  lunit = 2
  material = 0
  x = 10
  y = 10
  z = 10
FEATURE [Part::FeaturePython] GDMLTube  # WARN: FeaturePython — macro-defined, semantics opaque (R4)
  aunit = 1
  deltaphi = 90
  lunit = 2
  material = 0
  rmax = 7
  rmin = 5
  startphi = 0
  z = 7
FEATURE [App::Part] LV_Tube
  Group = -> [GDMLTube]
  Origin = -> Origin003
  Placement = pos=(-3,-4,0) rot=(0,0,1;0rad)
  SkinSurface = 0
FEATURE [App::Part] LV_Box
  Group = -> [GDMLBox_Box,LV_Tube]
  Origin = -> Origin002
  Placement = pos=(20,0,0) rot=(0,0,1;0rad)
FEATURE [Part::FeaturePython] Array  # Draft array (typed FeaturePython)
  AlwaysSyncPlacement = false
  Angle = 180
  ArrayType = 1
  Axis = (0,0,1)
  Base = -> LV_Box
  Center = (0,0,0)
  Count = 5
  ExpandArray = false
  Fuse = false
  IntervalAxis = (0,0,0)
  IntervalX = (100,0,0)
  IntervalY = (0,100,0)
  IntervalZ = (0,0,100)
  NumberCircles = 3
  NumberPolar = 5
  NumberX = 2
  NumberY = 2
  NumberZ = 1
  PlacementList = 5 placements: [(20,0,0),(14.1421,14.1421,0),(3.55271e-15,20,0),(-14.1421,14.1421,0),(-20,2.44929e-15,0)]
  RadialDistance = 50
  ScaleList = (5) [(1,1,1),(1,1,1),(1,1,1),(1,1,1),(1,1,1)]
  Symmetry = 1
  TangentialDistance = 25
FEATURE [App::Part] Part  label="experiment"
  Group = -> [LV_Box,Array]
  Origin = -> Origin001
FEATURE [App::Part] worldVOL
  Group = -> [GDMLBox_WorldBox,Part]
  Origin = -> Origin
